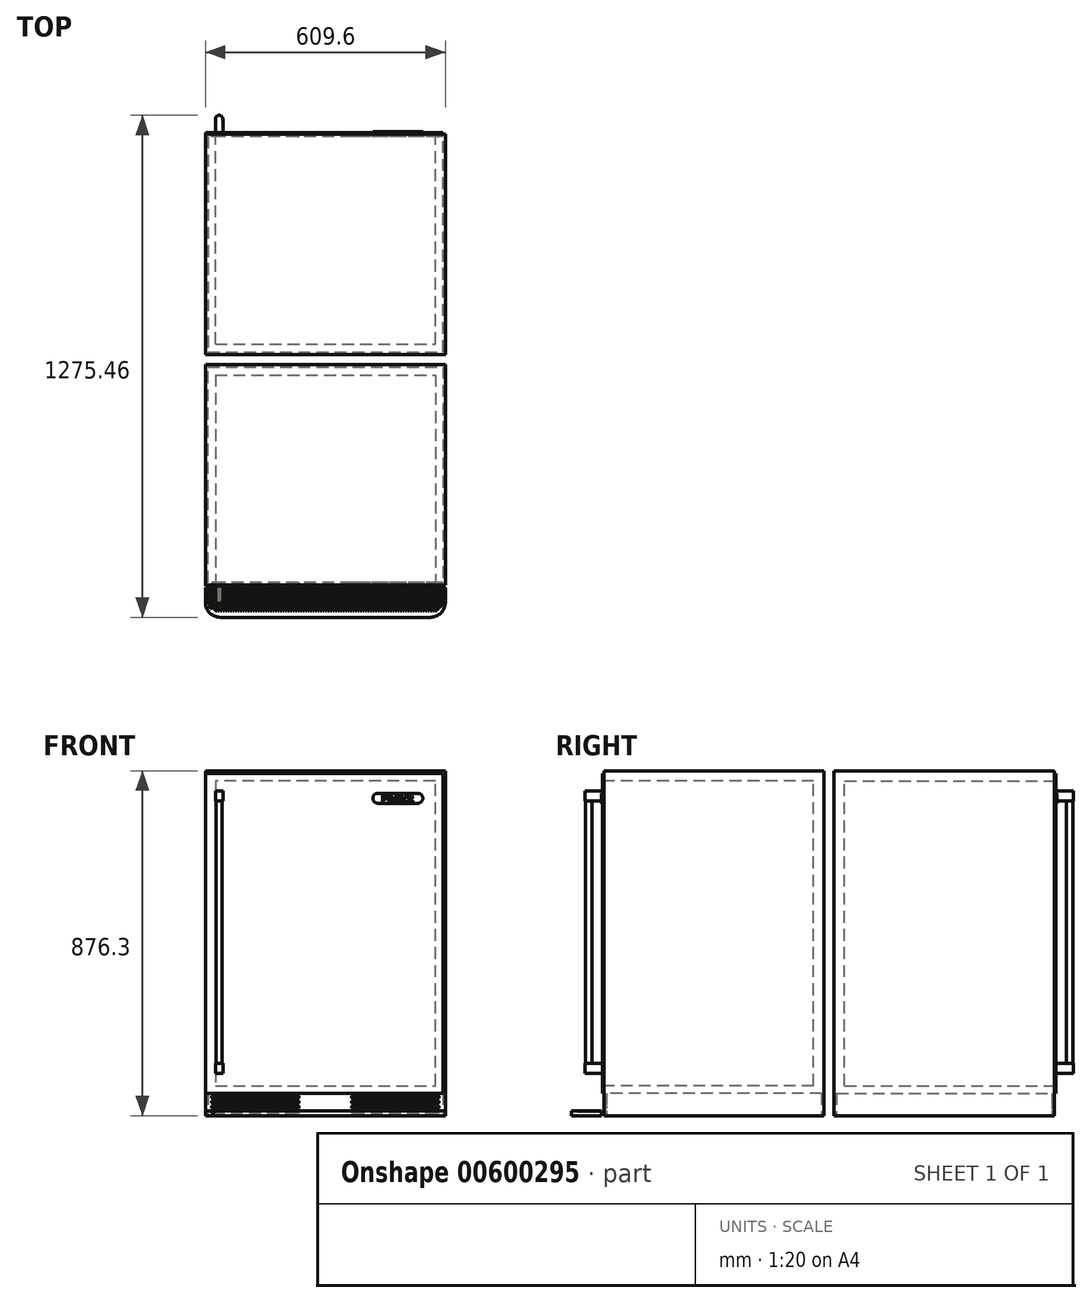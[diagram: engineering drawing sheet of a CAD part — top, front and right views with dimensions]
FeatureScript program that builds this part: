
annotation { "Feature Type Name" : "Feature", "Feature Type Description" : "" }
export const myFeature = defineFeature(function(context is Context, id is Id, definition is map)
    precondition{}
    {
        {
            var Q0;
            Q0=qCreatedBy(makeId("Front.planeOp"),FACE);
            var sketch = newSketch(context, id + "F0", { "sketchPlane" : qUnion([Q0])});
            skLineSegment(sketch, "E0.bottom", {"start": v(304.8, 438.15) * mm, "end": v(-304.8, 438.15) * mm});
            skLineSegment(sketch, "E0.top", {"start": v(304.8, -438.15) * mm, "end": v(-304.8, -438.15) * mm});
            skLineSegment(sketch, "E0.left", {"start": v(304.8, 438.15) * mm, "end": v(304.8, -438.15) * mm});
            skLineSegment(sketch, "E0.right", {"start": v(-304.8, 438.15) * mm, "end": v(-304.8, -438.15) * mm});
            skPoint(sketch, "E0.middle", {"position": v(0, 0) * mm});
            skSolve(sketch);
        }
        {
            var Q0;
            Q0 = qSketchRegion(id + "F0", true);
            extrude(context, id + "F1", {"entities" : qUnion([Q0]), "oppositeDirection" : true, "depth" : 559.94 * mm, "offsetDistance" : 25.4 * mm});
        }
        {
            var Q0;
            Q0=makeQuery(id+"F1.opExtrude","CAP_FACE",FACE,{"disambiguationData":[OSD([sQuery(id+"F0.wireOp",EDGE,"E0.bottom"),sQuery(id+"F0.wireOp",EDGE,"E0.top"),sQuery(id+"F0.wireOp",EDGE,"E0.left"),sQuery(id+"F0.wireOp",EDGE,"E0.right")])],"isStart":true});
            var sketch = newSketch(context, id + "F2", { "sketchPlane" : qUnion([Q0])});
            skLineSegment(sketch, "E1.0", {"start": v(-279.4, -412.75) * mm, "end": v(279.4, -412.75) * mm, "construction": true});
            skLineSegment(sketch, "E1.1", {"start": v(-279.4, 412.75) * mm, "end": v(-279.4, -412.75) * mm});
            skLineSegment(sketch, "E1.2", {"start": v(279.4, 412.75) * mm, "end": v(-279.4, 412.75) * mm});
            skLineSegment(sketch, "E1.3", {"start": v(279.4, -412.75) * mm, "end": v(279.4, 412.75) * mm});
            skLineSegment(sketch, "E2", {"start": v(-279.4, -361.95) * mm, "end": v(279.4, -361.95) * mm});
            skSolve(sketch);
        }
        {
            var Q0;
            Q0 = qSketchRegion(id + "F2", true);
            extrude(context, id + "F3", {"entities" : qUnion([Q0]), "operationType" : NewBodyOperationType.REMOVE, "oppositeDirection" : true, "depth" : 533.4 * mm, "offsetDistance" : 25.4 * mm});
        }
        {
            var Q0;
            Q0=makeQuery(id+"F1.opExtrude","CAP_FACE",FACE,{"disambiguationData":[OSD([sQuery(id+"F0.wireOp",EDGE,"E0.bottom"),sQuery(id+"F0.wireOp",EDGE,"E0.top"),sQuery(id+"F0.wireOp",EDGE,"E0.left"),sQuery(id+"F0.wireOp",EDGE,"E0.right")])],"isStart":true});
            var sketch = newSketch(context, id + "F4", { "sketchPlane" : qUnion([Q0])});
            skLineSegment(sketch, "E3.1", {"start": v(-304.8, 438.15) * mm, "end": v(-304.8, -438.15) * mm});
            skLineSegment(sketch, "E4.0", {"start": v(298.45, -431.8) * mm, "end": v(-304.8, -431.8) * mm, "construction": true});
            skLineSegment(sketch, "E4.1", {"start": v(298.45, 431.8) * mm, "end": v(298.45, -431.8) * mm});
            skLineSegment(sketch, "E4.2", {"start": v(298.45, 431.8) * mm, "end": v(-304.8, 431.8) * mm});
            skLineSegment(sketch, "E5", {"start": v(298.45, -381) * mm, "end": v(-304.8, -381) * mm});
            skSolve(sketch);
        }
        {
            var Q0;
            Q0 = qSketchRegion(id + "F4", true);
            extrude(context, id + "F5", {"entities" : qUnion([Q0]), "depth" : 3.17 * mm, "offsetDistance" : 25.4 * mm});
        }
        {
            var Q0;
            Q0=makeQuery(id+"F1.opExtrude","CAP_FACE",FACE,{"disambiguationData":[OSD([sQuery(id+"F0.wireOp",EDGE,"E0.bottom"),sQuery(id+"F0.wireOp",EDGE,"E0.top"),sQuery(id+"F0.wireOp",EDGE,"E0.left"),sQuery(id+"F0.wireOp",EDGE,"E0.right")])],"isStart":false});
            cPlane(context, id + "F6", {"entities" : qUnion([Q0]), "cplaneType" : CPlaneType.OFFSET, "offset" : 12.7 * mm, "width" : 152.4 * mm, "height" : 152.4 * mm});
        }
        {
            var Q0;
            Q0=makeQuery(id+"F1.opExtrude","CAP_FACE",FACE,{"disambiguationData":[OSD([sQuery(id+"F0.wireOp",EDGE,"E0.bottom"),sQuery(id+"F0.wireOp",EDGE,"E0.top"),sQuery(id+"F0.wireOp",EDGE,"E0.left"),sQuery(id+"F0.wireOp",EDGE,"E0.right")])],"isStart":true});
            var sketch = newSketch(context, id + "F7", { "sketchPlane" : qUnion([Q0])});
            skLineSegment(sketch, "E6", {"start": v(-285.75, -390.53) * mm, "end": v(-69.85, -390.53) * mm});
            skLineSegment(sketch, "E7", {"start": v(69.85, -390.53) * mm, "end": v(285.75, -390.53) * mm});
            skLineSegment(sketch, "E8", {"start": v(0, -484.65) * mm, "end": v(0, -438.15) * mm, "construction": true});
            skPoint(sketch, "E8.endSnap0", {"position": v(0, -438.15) * mm});
            skLineSegment(sketch, "E9.0.1.0", {"start": v(-285.75, -403.23) * mm, "end": v(-69.85, -403.23) * mm});
            skLineSegment(sketch, "E9.0.1.1", {"start": v(69.85, -403.22) * mm, "end": v(285.75, -403.22) * mm});
            skLineSegment(sketch, "E9.0.2.0", {"start": v(-285.75, -415.93) * mm, "end": v(-69.85, -415.93) * mm});
            skLineSegment(sketch, "E9.0.2.1", {"start": v(69.85, -415.93) * mm, "end": v(285.75, -415.93) * mm});
            skLineSegment(sketch, "E9.0.3.0", {"start": v(-285.75, -428.63) * mm, "end": v(-69.85, -428.63) * mm});
            skLineSegment(sketch, "E9.0.3.1", {"start": v(69.85, -428.62) * mm, "end": v(285.75, -428.62) * mm});
            skLineSegment(sketch, "E9.direction1", {"start": v(-285.75, -390.53) * mm, "end": v(-266.7, -390.53) * mm, "construction": true});
            skLineSegment(sketch, "E9.direction2", {"start": v(-285.75, -390.53) * mm, "end": v(-285.75, -403.23) * mm, "construction": true});
            skArc(sketch, "E10.0.startCap", {"start": v(-285.75, -393.7) * mm, "mid": v(-288.92, -390.53) * mm, "end": v(-285.75, -387.35) * mm});
            skArc(sketch, "E10.0.endCap", {"start": v(-69.85, -387.35) * mm, "mid": v(-66.67, -390.53) * mm, "end": v(-69.85, -393.7) * mm});
            skLineSegment(sketch, "E10.0.left", {"start": v(-285.75, -387.35) * mm, "end": v(-69.85, -387.35) * mm});
            skLineSegment(sketch, "E10.0.right", {"start": v(-285.75, -393.7) * mm, "end": v(-69.85, -393.7) * mm});
            skArc(sketch, "E10.1.startCap", {"start": v(-285.75, -406.4) * mm, "mid": v(-288.92, -403.23) * mm, "end": v(-285.75, -400.05) * mm});
            skArc(sketch, "E10.1.endCap", {"start": v(-69.85, -400.05) * mm, "mid": v(-66.67, -403.23) * mm, "end": v(-69.85, -406.4) * mm});
            skLineSegment(sketch, "E10.1.left", {"start": v(-285.75, -400.05) * mm, "end": v(-69.85, -400.05) * mm});
            skLineSegment(sketch, "E10.1.right", {"start": v(-285.75, -406.4) * mm, "end": v(-69.85, -406.4) * mm});
            skArc(sketch, "E10.2.startCap", {"start": v(-285.75, -419.1) * mm, "mid": v(-288.92, -415.93) * mm, "end": v(-285.75, -412.75) * mm});
            skArc(sketch, "E10.2.endCap", {"start": v(-69.85, -412.75) * mm, "mid": v(-66.67, -415.93) * mm, "end": v(-69.85, -419.1) * mm});
            skLineSegment(sketch, "E10.2.left", {"start": v(-285.75, -412.75) * mm, "end": v(-69.85, -412.75) * mm});
            skLineSegment(sketch, "E10.2.right", {"start": v(-285.75, -419.1) * mm, "end": v(-69.85, -419.1) * mm});
            skArc(sketch, "E10.3.startCap", {"start": v(-285.75, -431.8) * mm, "mid": v(-288.92, -428.63) * mm, "end": v(-285.75, -425.45) * mm});
            skArc(sketch, "E10.3.endCap", {"start": v(-69.85, -425.45) * mm, "mid": v(-66.67, -428.63) * mm, "end": v(-69.85, -431.8) * mm});
            skLineSegment(sketch, "E10.3.left", {"start": v(-285.75, -425.45) * mm, "end": v(-69.85, -425.45) * mm});
            skLineSegment(sketch, "E10.3.right", {"start": v(-285.75, -431.8) * mm, "end": v(-69.85, -431.8) * mm});
            skArc(sketch, "E10.4.startCap", {"start": v(69.85, -431.8) * mm, "mid": v(66.67, -428.63) * mm, "end": v(69.85, -425.45) * mm});
            skArc(sketch, "E10.4.endCap", {"start": v(285.75, -425.45) * mm, "mid": v(288.92, -428.63) * mm, "end": v(285.75, -431.8) * mm});
            skLineSegment(sketch, "E10.4.left", {"start": v(69.85, -425.45) * mm, "end": v(285.75, -425.45) * mm});
            skLineSegment(sketch, "E10.4.right", {"start": v(69.85, -431.8) * mm, "end": v(285.75, -431.8) * mm});
            skArc(sketch, "E10.5.startCap", {"start": v(69.85, -419.1) * mm, "mid": v(66.67, -415.93) * mm, "end": v(69.85, -412.75) * mm});
            skArc(sketch, "E10.5.endCap", {"start": v(285.75, -412.75) * mm, "mid": v(288.92, -415.93) * mm, "end": v(285.75, -419.1) * mm});
            skLineSegment(sketch, "E10.5.left", {"start": v(69.85, -412.75) * mm, "end": v(285.75, -412.75) * mm});
            skLineSegment(sketch, "E10.5.right", {"start": v(69.85, -419.1) * mm, "end": v(285.75, -419.1) * mm});
            skArc(sketch, "E10.6.startCap", {"start": v(69.85, -406.4) * mm, "mid": v(66.67, -403.23) * mm, "end": v(69.85, -400.05) * mm});
            skArc(sketch, "E10.6.endCap", {"start": v(285.75, -400.05) * mm, "mid": v(288.92, -403.23) * mm, "end": v(285.75, -406.4) * mm});
            skLineSegment(sketch, "E10.6.left", {"start": v(69.85, -400.05) * mm, "end": v(285.75, -400.05) * mm});
            skLineSegment(sketch, "E10.6.right", {"start": v(69.85, -406.4) * mm, "end": v(285.75, -406.4) * mm});
            skArc(sketch, "E10.7.startCap", {"start": v(69.85, -393.7) * mm, "mid": v(66.67, -390.53) * mm, "end": v(69.85, -387.35) * mm});
            skArc(sketch, "E10.7.endCap", {"start": v(285.75, -387.35) * mm, "mid": v(288.92, -390.53) * mm, "end": v(285.75, -393.7) * mm});
            skLineSegment(sketch, "E10.7.left", {"start": v(69.85, -387.35) * mm, "end": v(285.75, -387.35) * mm});
            skLineSegment(sketch, "E10.7.right", {"start": v(69.85, -393.7) * mm, "end": v(285.75, -393.7) * mm});
            skSolve(sketch);
        }
        {
            var Q0;
            Q0 = qSketchRegion(id + "F7", true);
            extrude(context, id + "F8", {"entities" : qUnion([Q0]), "operationType" : NewBodyOperationType.REMOVE, "oppositeDirection" : true, "depth" : 25.4 * mm, "offsetDistance" : 25.4 * mm});
        }
        {
            var Q0;
            Q0=makeQuery(id+"F1.opExtrude","SWEPT_FACE",FACE,{"disambiguationData":[OSD([sQuery(id+"F0.wireOp",EDGE,"E0.top")])]});
            var sketch = newSketch(context, id + "F9", { "sketchPlane" : qUnion([Q0])});
            skLineSegment(sketch, "E11.0", {"start": v(298.45, -6.35) * mm, "end": v(-298.45, -6.35) * mm});
            skLineSegment(sketch, "E11.1", {"start": v(298.45, -553.6) * mm, "end": v(298.45, -6.35) * mm});
            skLineSegment(sketch, "E11.2", {"start": v(-298.45, -553.6) * mm, "end": v(298.45, -553.6) * mm});
            skLineSegment(sketch, "E11.3", {"start": v(-298.45, -6.35) * mm, "end": v(-298.45, -553.6) * mm});
            skSolve(sketch);
        }
        {
            var Q0;
            Q0=makeQuery(id+"F9.imprint","IMPRINT",FACE,{"disambiguationData":[TD([[makeQuery(id+"F9.imprint","IMPRINT",EDGE,{"derivedFrom":sQuery(id+"F9.wireOp",EDGE,"E11.0")}),1.0]])]});
            extrude(context, id + "F10", {"entities" : qUnion([Q0]), "operationType" : NewBodyOperationType.REMOVE, "oppositeDirection" : true, "depth" : 57.15 * mm, "offsetDistance" : 25.4 * mm});
        }
        {
            var Q0;
            Q0=makeQuery(id+"F1.opExtrude","SWEPT_FACE",FACE,{"disambiguationData":[OSD([sQuery(id+"F0.wireOp",EDGE,"E0.bottom")])]});
            cPlane(context, id + "F11", {"entities" : qUnion([Q0]), "cplaneType" : CPlaneType.OFFSET, "offset" : 50.8 * mm, "oppositeDirection" : true, "width" : 152.4 * mm, "height" : 152.4 * mm});
        }
        {
            var Q0;
            Q0=qCreatedBy(id+"F11.planeOp",FACE);
            var sketch = newSketch(context, id + "F12", { "sketchPlane" : qUnion([Q0])});
            skCircle(sketch, "E12", {"center": v(-269.88, -38.1) * mm, "radius": 9.53 * mm});
            skLineSegment(sketch, "E13.0", {"start": v(298.45, -3.18) * mm, "end": v(-304.8, -3.18) * mm});
            skLineSegment(sketch, "E14", {"start": v(-279.4, -38.1) * mm, "end": v(-279.4, -3.18) * mm});
            skLineSegment(sketch, "E15", {"start": v(-279.4, -3.18) * mm, "end": v(-260.35, -3.18) * mm});
            skLineSegment(sketch, "E16", {"start": v(-260.35, -3.18) * mm, "end": v(-260.35, -38.1) * mm});
            skSolve(sketch);
        }
        {
            var Q0;
            Q0 = qSketchRegion(id + "F12", true);
            extrude(context, id + "F13", {"entities" : qUnion([Q0]), "operationType" : NewBodyOperationType.ADD, "oppositeDirection" : true, "depth" : 25.4 * mm, "offsetDistance" : 25.4 * mm});
        }
        {
            var Q0;
            Q0=makeQuery(id+"F5.opExtrude","SWEPT_FACE",FACE,{"disambiguationData":[OSD([sQuery(id+"F4.wireOp",EDGE,"E5")])]});
            cPlane(context, id + "F14", {"entities" : qUnion([Q0]), "cplaneType" : CPlaneType.OFFSET, "offset" : 50.8 * mm, "oppositeDirection" : true, "width" : 152.4 * mm, "height" : 152.4 * mm});
        }
        {
            var Q0;
            Q0=qCreatedBy(id+"F14.planeOp",FACE);
            var sketch = newSketch(context, id + "F15", { "sketchPlane" : qUnion([Q0])});
            skArc(sketch, "E17.0.0", {"start": v(-279.4, 38.1) * mm, "mid": v(-269.88, 47.62) * mm, "end": v(-260.35, 38.1) * mm});
            skLineSegment(sketch, "E17.0.1", {"start": v(-260.35, 38.1) * mm, "end": v(-260.35, 3.18) * mm});
            skLineSegment(sketch, "E17.0.2", {"start": v(-260.35, 3.18) * mm, "end": v(-279.4, 3.18) * mm});
            skLineSegment(sketch, "E17.0.3", {"start": v(-279.4, 3.18) * mm, "end": v(-279.4, 38.1) * mm});
            skSolve(sketch);
        }
        {
            var Q0;
            Q0 = qSketchRegion(id + "F15", true);
            extrude(context, id + "F16", {"entities" : qUnion([Q0]), "operationType" : NewBodyOperationType.ADD, "oppositeDirection" : true, "depth" : 25.4 * mm, "offsetDistance" : 25.4 * mm});
        }
        {
            var Q0;
            Q0=makeQuery(id+"F16.opExtrude","CAP_FACE",FACE,{"disambiguationData":[OSD([sQuery(id+"F15.wireOp",EDGE,"E17.0.0"),sQuery(id+"F15.wireOp",EDGE,"E17.0.1"),sQuery(id+"F15.wireOp",EDGE,"E17.0.2"),sQuery(id+"F15.wireOp",EDGE,"E17.0.3")])],"isStart":false});
            var sketch = newSketch(context, id + "F17", { "sketchPlane" : qUnion([Q0])});
            skCircle(sketch, "E18", {"center": v(-269.88, -38.1) * mm, "radius": 7.94 * mm});
            skSolve(sketch);
        }
        {
            var Q0;
            Q0 = qSketchRegion(id + "F17", true);
            extrude(context, id + "F18", {"entities" : qUnion([Q0]), "endBound" : BoundingType.UP_TO_NEXT, "depth" : 25.4 * mm, "offsetDistance" : 25.4 * mm});
        }
        {
            var Q0;
            Q0=makeQuery(id+"F5.opExtrude","CAP_FACE",FACE,{"disambiguationData":[OSD([sQuery(id+"F4.wireOp",EDGE,"E3.1"),sQuery(id+"F4.wireOp",EDGE,"E4.1"),sQuery(id+"F4.wireOp",EDGE,"E4.2"),sQuery(id+"F4.wireOp",EDGE,"E5")])],"isStart":false});
            var sketch = newSketch(context, id + "F19", { "sketchPlane" : qUnion([Q0])});
            skLineSegment(sketch, "E19", {"start": v(133.35, 368.3) * mm, "end": v(234.95, 368.3) * mm});
            skArc(sketch, "E20.0.startCap", {"start": v(133.35, 355.6) * mm, "mid": v(120.65, 368.3) * mm, "end": v(133.35, 381) * mm});
            skArc(sketch, "E20.0.endCap", {"start": v(234.95, 381) * mm, "mid": v(247.65, 368.3) * mm, "end": v(234.95, 355.6) * mm});
            skLineSegment(sketch, "E20.0.left", {"start": v(133.35, 381) * mm, "end": v(234.95, 381) * mm});
            skLineSegment(sketch, "E20.0.right", {"start": v(133.35, 355.6) * mm, "end": v(234.95, 355.6) * mm});
            skText(sketch, "E21", { "text": "Perlick", "fontName": "OpenSans-Regular.ttf"});
            skPoint(sketch, "E22", {"position": v(184.15, 381) * mm});
            skPoint(sketch, "E23", {"position": v(184.15, 368.3) * mm});
            const initialGuessF19  = {"E21": [0.1427, 0.35878, 1, 0, 0.01905]};
            skSetInitialGuess(sketch, initialGuessF19);
            skSolve(sketch);
        }
        {
            var Q0;
            Q0 = qSketchRegion(id + "F19", true);
            var Q1;
            {var subQ0=sQuery(id+"F19.wireOp",EDGE,"E21.sketch_text.stroke-10");Q1=makeQuery(id+"F19.imprint","IMPRINT",FACE,{"disambiguationData":[TD([[makeQuery(id+"F19.imprint","IMPRINT",EDGE,{"derivedFrom":subQ0}),1.0]])]});}
            var Q2;
            {var subQ1=sQuery(id+"F19.wireOp",EDGE,"E21.sketch_text.stroke-29");Q2=makeQuery(id+"F19.imprint","IMPRINT",FACE,{"disambiguationData":[TD([[makeQuery(id+"F19.imprint","IMPRINT",EDGE,{"derivedFrom":subQ1}),1.0]])]});}
            extrude(context, id + "F20", {"entities" : qUnion([Q0, Q1, Q2]), "depth" : 3.17 * mm, "offsetDistance" : 25.4 * mm});
        }
        {
            var Q0;
            Q0=makeQuery(id+"F1.opExtrude","SWEPT_BODY",BODY,{"disambiguationData":[OSD([sQuery(id+"F0.wireOp",EDGE,"E0.bottom"),sQuery(id+"F0.wireOp",EDGE,"E0.top"),sQuery(id+"F0.wireOp",EDGE,"E0.left"),sQuery(id+"F0.wireOp",EDGE,"E0.right")])]});
            var Q1;
            Q1=makeQuery(id+"F18.opExtrude","SWEPT_BODY",BODY,{"disambiguationData":[OSD([sQuery(id+"F17.wireOp",EDGE,"E18")])]});
            var Q2;
            Q2=makeQuery(id+"F5.opExtrude","SWEPT_BODY",BODY,{"disambiguationData":[OSD([sQuery(id+"F4.wireOp",EDGE,"E3.1"),sQuery(id+"F4.wireOp",EDGE,"E4.1"),sQuery(id+"F4.wireOp",EDGE,"E4.2"),sQuery(id+"F4.wireOp",EDGE,"E5")])]});
            var Q3;
            Q3=makeQuery(id+"F20.opExtrude","SWEPT_BODY",BODY,{"disambiguationData":[OSD([sQuery(id+"F19.wireOp",EDGE,"E19"),sQuery(id+"F19.wireOp",EDGE,"E20.0.startCap"),sQuery(id+"F19.wireOp",EDGE,"E20.0.endCap"),sQuery(id+"F19.wireOp",EDGE,"E20.0.left"),sQuery(id+"F19.wireOp",EDGE,"E20.0.right"),sQuery(id+"F19.wireOp",EDGE,"E21.sketch_text.stroke-0"),sQuery(id+"F19.wireOp",EDGE,"E21.sketch_text.stroke-1"),sQuery(id+"F19.wireOp",EDGE,"E21.sketch_text.stroke-2"),sQuery(id+"F19.wireOp",EDGE,"E21.sketch_text.stroke-3"),sQuery(id+"F19.wireOp",EDGE,"E21.sketch_text.stroke-4"),sQuery(id+"F19.wireOp",EDGE,"E21.sketch_text.stroke-5"),sQuery(id+"F19.wireOp",EDGE,"E21.sketch_text.stroke-6"),sQuery(id+"F19.wireOp",EDGE,"E21.sketch_text.stroke-7"),sQuery(id+"F19.wireOp",EDGE,"E21.sketch_text.stroke-15"),sQuery(id+"F19.wireOp",EDGE,"E21.sketch_text.stroke-16"),sQuery(id+"F19.wireOp",EDGE,"E21.sketch_text.stroke-17"),sQuery(id+"F19.wireOp",EDGE,"E21.sketch_text.stroke-18"),sQuery(id+"F19.wireOp",EDGE,"E21.sketch_text.stroke-19"),sQuery(id+"F19.wireOp",EDGE,"E21.sketch_text.stroke-20"),sQuery(id+"F19.wireOp",EDGE,"E21.sketch_text.stroke-21"),sQuery(id+"F19.wireOp",EDGE,"E21.sketch_text.stroke-22"),sQuery(id+"F19.wireOp",EDGE,"E21.sketch_text.stroke-23"),sQuery(id+"F19.wireOp",EDGE,"E21.sketch_text.stroke-24"),sQuery(id+"F19.wireOp",EDGE,"E21.sketch_text.stroke-25"),sQuery(id+"F19.wireOp",EDGE,"E21.sketch_text.stroke-26"),sQuery(id+"F19.wireOp",EDGE,"E21.sketch_text.stroke-27"),sQuery(id+"F19.wireOp",EDGE,"E21.sketch_text.stroke-28"),sQuery(id+"F19.wireOp",EDGE,"E21.sketch_text.stroke-34"),sQuery(id+"F19.wireOp",EDGE,"E21.sketch_text.stroke-35"),sQuery(id+"F19.wireOp",EDGE,"E21.sketch_text.stroke-36"),sQuery(id+"F19.wireOp",EDGE,"E21.sketch_text.stroke-37"),sQuery(id+"F19.wireOp",EDGE,"E21.sketch_text.stroke-38"),sQuery(id+"F19.wireOp",EDGE,"E21.sketch_text.stroke-39"),sQuery(id+"F19.wireOp",EDGE,"E21.sketch_text.stroke-40"),sQuery(id+"F19.wireOp",EDGE,"E21.sketch_text.stroke-41"),sQuery(id+"F19.wireOp",EDGE,"E21.sketch_text.stroke-42"),sQuery(id+"F19.wireOp",EDGE,"E21.sketch_text.stroke-43"),sQuery(id+"F19.wireOp",EDGE,"E21.sketch_text.stroke-44"),sQuery(id+"F19.wireOp",EDGE,"E21.sketch_text.stroke-45"),sQuery(id+"F19.wireOp",EDGE,"E21.sketch_text.stroke-46"),sQuery(id+"F19.wireOp",EDGE,"E21.sketch_text.stroke-47"),sQuery(id+"F19.wireOp",EDGE,"E21.sketch_text.stroke-48"),sQuery(id+"F19.wireOp",EDGE,"E21.sketch_text.stroke-49"),sQuery(id+"F19.wireOp",EDGE,"E21.sketch_text.stroke-50"),sQuery(id+"F19.wireOp",EDGE,"E21.sketch_text.stroke-51"),sQuery(id+"F19.wireOp",EDGE,"E21.sketch_text.stroke-52"),sQuery(id+"F19.wireOp",EDGE,"E21.sketch_text.stroke-53"),sQuery(id+"F19.wireOp",EDGE,"E21.sketch_text.stroke-54"),sQuery(id+"F19.wireOp",EDGE,"E21.sketch_text.stroke-55"),sQuery(id+"F19.wireOp",EDGE,"E21.sketch_text.stroke-56"),sQuery(id+"F19.wireOp",EDGE,"E21.sketch_text.stroke-57"),sQuery(id+"F19.wireOp",EDGE,"E21.sketch_text.stroke-58"),sQuery(id+"F19.wireOp",EDGE,"E21.sketch_text.stroke-59"),sQuery(id+"F19.wireOp",EDGE,"E21.sketch_text.stroke-60"),sQuery(id+"F19.wireOp",EDGE,"E21.sketch_text.stroke-61"),sQuery(id+"F19.wireOp",EDGE,"E21.sketch_text.stroke-62"),sQuery(id+"F19.wireOp",EDGE,"E21.sketch_text.stroke-63"),sQuery(id+"F19.wireOp",EDGE,"E21.sketch_text.stroke-64"),sQuery(id+"F19.wireOp",EDGE,"E21.sketch_text.stroke-65"),sQuery(id+"F19.wireOp",EDGE,"E21.sketch_text.stroke-66"),sQuery(id+"F19.wireOp",EDGE,"E21.sketch_text.stroke-67"),sQuery(id+"F19.wireOp",EDGE,"E21.sketch_text.stroke-68"),sQuery(id+"F19.wireOp",EDGE,"E21.sketch_text.stroke-69"),sQuery(id+"F19.wireOp",EDGE,"E21.sketch_text.stroke-70"),sQuery(id+"F19.wireOp",EDGE,"E21.sketch_text.stroke-71"),sQuery(id+"F19.wireOp",EDGE,"E21.sketch_text.stroke-72"),sQuery(id+"F19.wireOp",EDGE,"E21.sketch_text.stroke-73"),sQuery(id+"F19.wireOp",EDGE,"E21.sketch_text.stroke-74"),sQuery(id+"F19.wireOp",EDGE,"E21.sketch_text.stroke-75"),sQuery(id+"F19.wireOp",EDGE,"E21.sketch_text.stroke-76"),sQuery(id+"F19.wireOp",EDGE,"E21.sketch_text.stroke-77"),sQuery(id+"F19.wireOp",EDGE,"E21.sketch_text.stroke-79"),sQuery(id+"F19.wireOp",EDGE,"E21.sketch_text.stroke-80"),sQuery(id+"F19.wireOp",EDGE,"E21.sketch_text.stroke-81"),sQuery(id+"F19.wireOp",EDGE,"E21.sketch_text.stroke-82"),sQuery(id+"F19.wireOp",EDGE,"E21.sketch_text.stroke-83"),sQuery(id+"F19.wireOp",EDGE,"E21.sketch_text.stroke-84"),sQuery(id+"F19.wireOp",EDGE,"E21.sketch_text.stroke-85"),sQuery(id+"F19.wireOp",EDGE,"E21.sketch_text.stroke-86"),sQuery(id+"F19.wireOp",EDGE,"E21.sketch_text.stroke-87"),sQuery(id+"F19.wireOp",EDGE,"E21.sketch_text.stroke-88"),sQuery(id+"F19.wireOp",EDGE,"E21.sketch_text.stroke-89"),sQuery(id+"F19.wireOp",EDGE,"E21.sketch_text.stroke-90")])]});
            var Q4;
            Q4=qCreatedBy(id+"F6.planeOp",FACE);
            mirror(context, id + "F21", {"entities" : qUnion([Q0, Q1, Q2, Q3]), "mirrorPlane" : qUnion([Q4])});
        }
        {
            var Q0;
            Q0=makeQuery(id+"F21.opPattern","COPY",FACE,{"derivedFrom":makeQuery(id+"F1.opExtrude","SWEPT_FACE",FACE,{"disambiguationData":[OSD([sQuery(id+"F0.wireOp",EDGE,"E0.top")])]}),"instanceName":"1"});
            var sketch = newSketch(context, id + "F22", { "sketchPlane" : qUnion([Q0])});
            skLineSegment(sketch, "E24.bottom", {"start": v(-266.7, 82.55) * mm, "end": v(266.7, 82.55) * mm});
            skLineSegment(sketch, "E24.top", {"start": v(-304.8, 6.35) * mm, "end": v(304.8, 6.35) * mm});
            skLineSegment(sketch, "E24.left", {"start": v(-304.8, 44.45) * mm, "end": v(-304.8, 6.35) * mm});
            skLineSegment(sketch, "E24.right", {"start": v(304.8, 44.45) * mm, "end": v(304.8, 6.35) * mm});
            skPoint(sketch, "E25.visualSharp", {"position": v(-304.8, 82.55) * mm});
            skArc(sketch, "E25.filletArc", {"start": v(-266.7, 82.55) * mm, "mid": v(-293.64, 71.4) * mm, "end": v(-304.8, 44.45) * mm});
            skPoint(sketch, "E26.visualSharp", {"position": v(304.8, 82.55) * mm});
            skArc(sketch, "E26.filletArc", {"start": v(304.8, 44.45) * mm, "mid": v(293.64, 71.4) * mm, "end": v(266.7, 82.55) * mm});
            skSolve(sketch);
        }
        {
            var Q0;
            Q0 = qSketchRegion(id + "F22", true);
            extrude(context, id + "F23", {"entities" : qUnion([Q0]), "oppositeDirection" : true, "depth" : 12.7 * mm, "offsetDistance" : 25.4 * mm});
        }
        {
            var Q0;
            Q0=makeQuery(id+"F23.opExtrude","CAP_FACE",FACE,{"disambiguationData":[OSD([sQuery(id+"F22.wireOp",EDGE,"E24.bottom"),sQuery(id+"F22.wireOp",EDGE,"E24.top"),sQuery(id+"F22.wireOp",EDGE,"E24.left"),sQuery(id+"F22.wireOp",EDGE,"E24.right"),sQuery(id+"F22.wireOp",EDGE,"E25.filletArc"),sQuery(id+"F22.wireOp",EDGE,"E26.filletArc")])],"isStart":false});
            var sketch = newSketch(context, id + "F24", { "sketchPlane" : qUnion([Q0])});
            skCircle(sketch, "E27", {"center": v(-300.02, -11.11) * mm, "radius": 1.59 * mm});
            skCircle(sketch, "E28", {"center": v(-296.85, -14.29) * mm, "radius": 1.59 * mm});
            skCircle(sketch, "E29", {"center": v(-293.67, -11.11) * mm, "radius": 1.59 * mm});
            skLineSegment(sketch, "E30", {"start": v(-300.02, -11.11) * mm, "end": v(-293.67, -11.11) * mm, "construction": true});
            skLineSegment(sketch, "E31", {"start": v(-296.85, -11.11) * mm, "end": v(-296.85, -14.29) * mm, "construction": true});
            skCircle(sketch, "E32", {"center": v(-290.5, -14.29) * mm, "radius": 1.59 * mm});
            skLineSegment(sketch, "E33", {"start": v(-296.85, -14.29) * mm, "end": v(-290.5, -14.29) * mm, "construction": true});
            skCircle(sketch, "E34.1.0.0", {"center": v(-280.97, -11.11) * mm, "radius": 1.59 * mm});
            skCircle(sketch, "E34.1.0.1", {"center": v(-287.32, -11.11) * mm, "radius": 1.59 * mm});
            skCircle(sketch, "E34.1.0.2", {"center": v(-284.15, -14.29) * mm, "radius": 1.59 * mm});
            skCircle(sketch, "E34.1.0.3", {"center": v(-277.8, -14.29) * mm, "radius": 1.59 * mm});
            skCircle(sketch, "E34.2.0.0", {"center": v(-268.27, -11.11) * mm, "radius": 1.59 * mm});
            skCircle(sketch, "E34.2.0.1", {"center": v(-274.62, -11.11) * mm, "radius": 1.59 * mm});
            skCircle(sketch, "E34.2.0.2", {"center": v(-271.45, -14.29) * mm, "radius": 1.59 * mm});
            skCircle(sketch, "E34.2.0.3", {"center": v(-265.1, -14.29) * mm, "radius": 1.59 * mm});
            skCircle(sketch, "E34.3.0.0", {"center": v(-255.57, -11.11) * mm, "radius": 1.59 * mm});
            skCircle(sketch, "E34.3.0.1", {"center": v(-261.92, -11.11) * mm, "radius": 1.59 * mm});
            skCircle(sketch, "E34.3.0.2", {"center": v(-258.75, -14.29) * mm, "radius": 1.59 * mm});
            skCircle(sketch, "E34.3.0.3", {"center": v(-252.4, -14.29) * mm, "radius": 1.59 * mm});
            skCircle(sketch, "E34.4.0.0", {"center": v(-242.87, -11.11) * mm, "radius": 1.59 * mm});
            skCircle(sketch, "E34.4.0.1", {"center": v(-249.22, -11.11) * mm, "radius": 1.59 * mm});
            skCircle(sketch, "E34.4.0.2", {"center": v(-246.05, -14.29) * mm, "radius": 1.59 * mm});
            skCircle(sketch, "E34.4.0.3", {"center": v(-239.7, -14.29) * mm, "radius": 1.59 * mm});
            skCircle(sketch, "E34.5.0.0", {"center": v(-230.17, -11.11) * mm, "radius": 1.59 * mm});
            skCircle(sketch, "E34.5.0.1", {"center": v(-236.52, -11.11) * mm, "radius": 1.59 * mm});
            skCircle(sketch, "E34.5.0.2", {"center": v(-233.35, -14.29) * mm, "radius": 1.59 * mm});
            skCircle(sketch, "E34.5.0.3", {"center": v(-227, -14.29) * mm, "radius": 1.59 * mm});
            skCircle(sketch, "E34.6.0.0", {"center": v(-217.47, -11.11) * mm, "radius": 1.59 * mm});
            skCircle(sketch, "E34.6.0.1", {"center": v(-223.82, -11.11) * mm, "radius": 1.59 * mm});
            skCircle(sketch, "E34.6.0.2", {"center": v(-220.65, -14.29) * mm, "radius": 1.59 * mm});
            skCircle(sketch, "E34.6.0.3", {"center": v(-214.3, -14.29) * mm, "radius": 1.59 * mm});
            skCircle(sketch, "E34.7.0.0", {"center": v(-204.77, -11.11) * mm, "radius": 1.59 * mm});
            skCircle(sketch, "E34.7.0.1", {"center": v(-211.12, -11.11) * mm, "radius": 1.59 * mm});
            skCircle(sketch, "E34.7.0.2", {"center": v(-207.95, -14.29) * mm, "radius": 1.59 * mm});
            skCircle(sketch, "E34.7.0.3", {"center": v(-201.6, -14.29) * mm, "radius": 1.59 * mm});
            skCircle(sketch, "E34.8.0.0", {"center": v(-192.07, -11.11) * mm, "radius": 1.59 * mm});
            skCircle(sketch, "E34.8.0.1", {"center": v(-198.42, -11.11) * mm, "radius": 1.59 * mm});
            skCircle(sketch, "E34.8.0.2", {"center": v(-195.25, -14.29) * mm, "radius": 1.59 * mm});
            skCircle(sketch, "E34.8.0.3", {"center": v(-188.9, -14.29) * mm, "radius": 1.59 * mm});
            skCircle(sketch, "E34.9.0.0", {"center": v(-179.37, -11.11) * mm, "radius": 1.59 * mm});
            skCircle(sketch, "E34.9.0.1", {"center": v(-185.72, -11.11) * mm, "radius": 1.59 * mm});
            skCircle(sketch, "E34.9.0.2", {"center": v(-182.55, -14.29) * mm, "radius": 1.59 * mm});
            skCircle(sketch, "E34.9.0.3", {"center": v(-176.2, -14.29) * mm, "radius": 1.59 * mm});
            skCircle(sketch, "E34.10.0.0", {"center": v(-166.67, -11.11) * mm, "radius": 1.59 * mm});
            skCircle(sketch, "E34.10.0.1", {"center": v(-173.02, -11.11) * mm, "radius": 1.59 * mm});
            skCircle(sketch, "E34.10.0.2", {"center": v(-169.85, -14.29) * mm, "radius": 1.59 * mm});
            skCircle(sketch, "E34.10.0.3", {"center": v(-163.5, -14.29) * mm, "radius": 1.59 * mm});
            skCircle(sketch, "E34.11.0.0", {"center": v(-153.97, -11.11) * mm, "radius": 1.59 * mm});
            skCircle(sketch, "E34.11.0.1", {"center": v(-160.32, -11.11) * mm, "radius": 1.59 * mm});
            skCircle(sketch, "E34.11.0.2", {"center": v(-157.15, -14.29) * mm, "radius": 1.59 * mm});
            skCircle(sketch, "E34.11.0.3", {"center": v(-150.8, -14.29) * mm, "radius": 1.59 * mm});
            skCircle(sketch, "E34.12.0.0", {"center": v(-141.27, -11.11) * mm, "radius": 1.59 * mm});
            skCircle(sketch, "E34.12.0.1", {"center": v(-147.62, -11.11) * mm, "radius": 1.59 * mm});
            skCircle(sketch, "E34.12.0.2", {"center": v(-144.45, -14.29) * mm, "radius": 1.59 * mm});
            skCircle(sketch, "E34.12.0.3", {"center": v(-138.1, -14.29) * mm, "radius": 1.59 * mm});
            skCircle(sketch, "E34.13.0.0", {"center": v(-128.57, -11.11) * mm, "radius": 1.59 * mm});
            skCircle(sketch, "E34.13.0.1", {"center": v(-134.92, -11.11) * mm, "radius": 1.59 * mm});
            skCircle(sketch, "E34.13.0.2", {"center": v(-131.75, -14.29) * mm, "radius": 1.59 * mm});
            skCircle(sketch, "E34.13.0.3", {"center": v(-125.4, -14.29) * mm, "radius": 1.59 * mm});
            skCircle(sketch, "E34.14.0.0", {"center": v(-115.87, -11.11) * mm, "radius": 1.59 * mm});
            skCircle(sketch, "E34.14.0.1", {"center": v(-122.22, -11.11) * mm, "radius": 1.59 * mm});
            skCircle(sketch, "E34.14.0.2", {"center": v(-119.05, -14.29) * mm, "radius": 1.59 * mm});
            skCircle(sketch, "E34.14.0.3", {"center": v(-112.7, -14.29) * mm, "radius": 1.59 * mm});
            skCircle(sketch, "E34.15.0.0", {"center": v(-103.17, -11.11) * mm, "radius": 1.59 * mm});
            skCircle(sketch, "E34.15.0.1", {"center": v(-109.52, -11.11) * mm, "radius": 1.59 * mm});
            skCircle(sketch, "E34.15.0.2", {"center": v(-106.35, -14.29) * mm, "radius": 1.59 * mm});
            skCircle(sketch, "E34.15.0.3", {"center": v(-100, -14.29) * mm, "radius": 1.59 * mm});
            skCircle(sketch, "E34.16.0.0", {"center": v(-90.47, -11.11) * mm, "radius": 1.59 * mm});
            skCircle(sketch, "E34.16.0.1", {"center": v(-96.82, -11.11) * mm, "radius": 1.59 * mm});
            skCircle(sketch, "E34.16.0.2", {"center": v(-93.65, -14.29) * mm, "radius": 1.59 * mm});
            skCircle(sketch, "E34.16.0.3", {"center": v(-87.3, -14.29) * mm, "radius": 1.59 * mm});
            skCircle(sketch, "E34.17.0.0", {"center": v(-77.77, -11.11) * mm, "radius": 1.59 * mm});
            skCircle(sketch, "E34.17.0.1", {"center": v(-84.12, -11.11) * mm, "radius": 1.59 * mm});
            skCircle(sketch, "E34.17.0.2", {"center": v(-80.95, -14.29) * mm, "radius": 1.59 * mm});
            skCircle(sketch, "E34.17.0.3", {"center": v(-74.6, -14.29) * mm, "radius": 1.59 * mm});
            skCircle(sketch, "E34.18.0.0", {"center": v(-65.07, -11.11) * mm, "radius": 1.59 * mm});
            skCircle(sketch, "E34.18.0.1", {"center": v(-71.42, -11.11) * mm, "radius": 1.59 * mm});
            skCircle(sketch, "E34.18.0.2", {"center": v(-68.25, -14.29) * mm, "radius": 1.59 * mm});
            skCircle(sketch, "E34.18.0.3", {"center": v(-61.9, -14.29) * mm, "radius": 1.59 * mm});
            skCircle(sketch, "E34.19.0.0", {"center": v(-52.37, -11.11) * mm, "radius": 1.59 * mm});
            skCircle(sketch, "E34.19.0.1", {"center": v(-58.72, -11.11) * mm, "radius": 1.59 * mm});
            skCircle(sketch, "E34.19.0.2", {"center": v(-55.55, -14.29) * mm, "radius": 1.59 * mm});
            skCircle(sketch, "E34.19.0.3", {"center": v(-49.2, -14.29) * mm, "radius": 1.59 * mm});
            skCircle(sketch, "E34.20.0.0", {"center": v(-39.67, -11.11) * mm, "radius": 1.59 * mm});
            skCircle(sketch, "E34.20.0.1", {"center": v(-46.02, -11.11) * mm, "radius": 1.59 * mm});
            skCircle(sketch, "E34.20.0.2", {"center": v(-42.85, -14.29) * mm, "radius": 1.59 * mm});
            skCircle(sketch, "E34.20.0.3", {"center": v(-36.5, -14.29) * mm, "radius": 1.59 * mm});
            skCircle(sketch, "E34.21.0.0", {"center": v(-26.97, -11.11) * mm, "radius": 1.59 * mm});
            skCircle(sketch, "E34.21.0.1", {"center": v(-33.32, -11.11) * mm, "radius": 1.59 * mm});
            skCircle(sketch, "E34.21.0.2", {"center": v(-30.15, -14.29) * mm, "radius": 1.59 * mm});
            skCircle(sketch, "E34.21.0.3", {"center": v(-23.8, -14.29) * mm, "radius": 1.59 * mm});
            skCircle(sketch, "E34.22.0.0", {"center": v(-14.27, -11.11) * mm, "radius": 1.59 * mm});
            skCircle(sketch, "E34.22.0.1", {"center": v(-20.62, -11.11) * mm, "radius": 1.59 * mm});
            skCircle(sketch, "E34.22.0.2", {"center": v(-17.45, -14.29) * mm, "radius": 1.59 * mm});
            skCircle(sketch, "E34.22.0.3", {"center": v(-11.1, -14.29) * mm, "radius": 1.59 * mm});
            skCircle(sketch, "E34.23.0.0", {"center": v(-1.57, -11.11) * mm, "radius": 1.59 * mm});
            skCircle(sketch, "E34.23.0.1", {"center": v(-7.92, -11.11) * mm, "radius": 1.59 * mm});
            skCircle(sketch, "E34.23.0.2", {"center": v(-4.75, -14.29) * mm, "radius": 1.59 * mm});
            skCircle(sketch, "E34.23.0.3", {"center": v(1.6, -14.29) * mm, "radius": 1.59 * mm});
            skCircle(sketch, "E34.24.0.0", {"center": v(11.13, -11.11) * mm, "radius": 1.59 * mm});
            skCircle(sketch, "E34.24.0.1", {"center": v(4.78, -11.11) * mm, "radius": 1.59 * mm});
            skCircle(sketch, "E34.24.0.2", {"center": v(7.95, -14.29) * mm, "radius": 1.59 * mm});
            skCircle(sketch, "E34.24.0.3", {"center": v(14.3, -14.29) * mm, "radius": 1.59 * mm});
            skCircle(sketch, "E34.25.0.0", {"center": v(23.83, -11.11) * mm, "radius": 1.59 * mm});
            skCircle(sketch, "E34.25.0.1", {"center": v(17.48, -11.11) * mm, "radius": 1.59 * mm});
            skCircle(sketch, "E34.25.0.2", {"center": v(20.65, -14.29) * mm, "radius": 1.59 * mm});
            skCircle(sketch, "E34.25.0.3", {"center": v(27, -14.29) * mm, "radius": 1.59 * mm});
            skCircle(sketch, "E34.26.0.0", {"center": v(36.53, -11.11) * mm, "radius": 1.59 * mm});
            skCircle(sketch, "E34.26.0.1", {"center": v(30.18, -11.11) * mm, "radius": 1.59 * mm});
            skCircle(sketch, "E34.26.0.2", {"center": v(33.35, -14.29) * mm, "radius": 1.59 * mm});
            skCircle(sketch, "E34.26.0.3", {"center": v(39.7, -14.29) * mm, "radius": 1.59 * mm});
            skCircle(sketch, "E34.27.0.0", {"center": v(49.23, -11.11) * mm, "radius": 1.59 * mm});
            skCircle(sketch, "E34.27.0.1", {"center": v(42.88, -11.11) * mm, "radius": 1.59 * mm});
            skCircle(sketch, "E34.27.0.2", {"center": v(46.05, -14.29) * mm, "radius": 1.59 * mm});
            skCircle(sketch, "E34.27.0.3", {"center": v(52.4, -14.29) * mm, "radius": 1.59 * mm});
            skCircle(sketch, "E34.28.0.0", {"center": v(61.93, -11.11) * mm, "radius": 1.59 * mm});
            skCircle(sketch, "E34.28.0.1", {"center": v(55.58, -11.11) * mm, "radius": 1.59 * mm});
            skCircle(sketch, "E34.28.0.2", {"center": v(58.75, -14.29) * mm, "radius": 1.59 * mm});
            skCircle(sketch, "E34.28.0.3", {"center": v(65.1, -14.29) * mm, "radius": 1.59 * mm});
            skCircle(sketch, "E34.29.0.0", {"center": v(74.63, -11.11) * mm, "radius": 1.59 * mm});
            skCircle(sketch, "E34.29.0.1", {"center": v(68.28, -11.11) * mm, "radius": 1.59 * mm});
            skCircle(sketch, "E34.29.0.2", {"center": v(71.45, -14.29) * mm, "radius": 1.59 * mm});
            skCircle(sketch, "E34.29.0.3", {"center": v(77.8, -14.29) * mm, "radius": 1.59 * mm});
            skCircle(sketch, "E34.30.0.0", {"center": v(87.33, -11.11) * mm, "radius": 1.59 * mm});
            skCircle(sketch, "E34.30.0.1", {"center": v(80.98, -11.11) * mm, "radius": 1.59 * mm});
            skCircle(sketch, "E34.30.0.2", {"center": v(84.15, -14.29) * mm, "radius": 1.59 * mm});
            skCircle(sketch, "E34.30.0.3", {"center": v(90.5, -14.29) * mm, "radius": 1.59 * mm});
            skCircle(sketch, "E34.31.0.0", {"center": v(100.03, -11.11) * mm, "radius": 1.59 * mm});
            skCircle(sketch, "E34.31.0.1", {"center": v(93.68, -11.11) * mm, "radius": 1.59 * mm});
            skCircle(sketch, "E34.31.0.2", {"center": v(96.85, -14.29) * mm, "radius": 1.59 * mm});
            skCircle(sketch, "E34.31.0.3", {"center": v(103.2, -14.29) * mm, "radius": 1.59 * mm});
            skCircle(sketch, "E34.32.0.0", {"center": v(112.73, -11.11) * mm, "radius": 1.59 * mm});
            skCircle(sketch, "E34.32.0.1", {"center": v(106.38, -11.11) * mm, "radius": 1.59 * mm});
            skCircle(sketch, "E34.32.0.2", {"center": v(109.55, -14.29) * mm, "radius": 1.59 * mm});
            skCircle(sketch, "E34.32.0.3", {"center": v(115.9, -14.29) * mm, "radius": 1.59 * mm});
            skCircle(sketch, "E34.33.0.0", {"center": v(125.43, -11.11) * mm, "radius": 1.59 * mm});
            skCircle(sketch, "E34.33.0.1", {"center": v(119.08, -11.11) * mm, "radius": 1.59 * mm});
            skCircle(sketch, "E34.33.0.2", {"center": v(122.25, -14.29) * mm, "radius": 1.59 * mm});
            skCircle(sketch, "E34.33.0.3", {"center": v(128.6, -14.29) * mm, "radius": 1.59 * mm});
            skCircle(sketch, "E34.34.0.0", {"center": v(138.13, -11.11) * mm, "radius": 1.59 * mm});
            skCircle(sketch, "E34.34.0.1", {"center": v(131.78, -11.11) * mm, "radius": 1.59 * mm});
            skCircle(sketch, "E34.34.0.2", {"center": v(134.95, -14.29) * mm, "radius": 1.59 * mm});
            skCircle(sketch, "E34.34.0.3", {"center": v(141.3, -14.29) * mm, "radius": 1.59 * mm});
            skCircle(sketch, "E34.35.0.0", {"center": v(150.83, -11.11) * mm, "radius": 1.59 * mm});
            skCircle(sketch, "E34.35.0.1", {"center": v(144.48, -11.11) * mm, "radius": 1.59 * mm});
            skCircle(sketch, "E34.35.0.2", {"center": v(147.65, -14.29) * mm, "radius": 1.59 * mm});
            skCircle(sketch, "E34.35.0.3", {"center": v(154, -14.29) * mm, "radius": 1.59 * mm});
            skCircle(sketch, "E34.36.0.0", {"center": v(163.53, -11.11) * mm, "radius": 1.59 * mm});
            skCircle(sketch, "E34.36.0.1", {"center": v(157.18, -11.11) * mm, "radius": 1.59 * mm});
            skCircle(sketch, "E34.36.0.2", {"center": v(160.35, -14.29) * mm, "radius": 1.59 * mm});
            skCircle(sketch, "E34.36.0.3", {"center": v(166.7, -14.29) * mm, "radius": 1.59 * mm});
            skCircle(sketch, "E34.37.0.0", {"center": v(176.23, -11.11) * mm, "radius": 1.59 * mm});
            skCircle(sketch, "E34.37.0.1", {"center": v(169.88, -11.11) * mm, "radius": 1.59 * mm});
            skCircle(sketch, "E34.37.0.2", {"center": v(173.05, -14.29) * mm, "radius": 1.59 * mm});
            skCircle(sketch, "E34.37.0.3", {"center": v(179.4, -14.29) * mm, "radius": 1.59 * mm});
            skCircle(sketch, "E34.38.0.0", {"center": v(188.93, -11.11) * mm, "radius": 1.59 * mm});
            skCircle(sketch, "E34.38.0.1", {"center": v(182.58, -11.11) * mm, "radius": 1.59 * mm});
            skCircle(sketch, "E34.38.0.2", {"center": v(185.75, -14.29) * mm, "radius": 1.59 * mm});
            skCircle(sketch, "E34.38.0.3", {"center": v(192.1, -14.29) * mm, "radius": 1.59 * mm});
            skCircle(sketch, "E34.39.0.0", {"center": v(201.63, -11.11) * mm, "radius": 1.59 * mm});
            skCircle(sketch, "E34.39.0.1", {"center": v(195.28, -11.11) * mm, "radius": 1.59 * mm});
            skCircle(sketch, "E34.39.0.2", {"center": v(198.45, -14.29) * mm, "radius": 1.59 * mm});
            skCircle(sketch, "E34.39.0.3", {"center": v(204.8, -14.29) * mm, "radius": 1.59 * mm});
            skCircle(sketch, "E34.40.0.0", {"center": v(214.33, -11.11) * mm, "radius": 1.59 * mm});
            skCircle(sketch, "E34.40.0.1", {"center": v(207.98, -11.11) * mm, "radius": 1.59 * mm});
            skCircle(sketch, "E34.40.0.2", {"center": v(211.15, -14.29) * mm, "radius": 1.59 * mm});
            skCircle(sketch, "E34.40.0.3", {"center": v(217.5, -14.29) * mm, "radius": 1.59 * mm});
            skCircle(sketch, "E34.41.0.0", {"center": v(227.03, -11.11) * mm, "radius": 1.59 * mm});
            skCircle(sketch, "E34.41.0.1", {"center": v(220.68, -11.11) * mm, "radius": 1.59 * mm});
            skCircle(sketch, "E34.41.0.2", {"center": v(223.85, -14.29) * mm, "radius": 1.59 * mm});
            skCircle(sketch, "E34.41.0.3", {"center": v(230.2, -14.29) * mm, "radius": 1.59 * mm});
            skCircle(sketch, "E34.42.0.0", {"center": v(239.73, -11.11) * mm, "radius": 1.59 * mm});
            skCircle(sketch, "E34.42.0.1", {"center": v(233.38, -11.11) * mm, "radius": 1.59 * mm});
            skCircle(sketch, "E34.42.0.2", {"center": v(236.55, -14.29) * mm, "radius": 1.59 * mm});
            skCircle(sketch, "E34.42.0.3", {"center": v(242.9, -14.29) * mm, "radius": 1.59 * mm});
            skCircle(sketch, "E34.43.0.0", {"center": v(252.43, -11.11) * mm, "radius": 1.59 * mm});
            skCircle(sketch, "E34.43.0.1", {"center": v(246.08, -11.11) * mm, "radius": 1.59 * mm});
            skCircle(sketch, "E34.43.0.2", {"center": v(249.25, -14.29) * mm, "radius": 1.59 * mm});
            skCircle(sketch, "E34.43.0.3", {"center": v(255.6, -14.29) * mm, "radius": 1.59 * mm});
            skCircle(sketch, "E34.44.0.0", {"center": v(265.13, -11.11) * mm, "radius": 1.59 * mm});
            skCircle(sketch, "E34.44.0.1", {"center": v(258.78, -11.11) * mm, "radius": 1.59 * mm});
            skCircle(sketch, "E34.44.0.2", {"center": v(261.95, -14.29) * mm, "radius": 1.59 * mm});
            skCircle(sketch, "E34.44.0.3", {"center": v(268.3, -14.29) * mm, "radius": 1.59 * mm});
            skCircle(sketch, "E34.45.0.0", {"center": v(277.83, -11.11) * mm, "radius": 1.59 * mm});
            skCircle(sketch, "E34.45.0.1", {"center": v(271.48, -11.11) * mm, "radius": 1.59 * mm});
            skCircle(sketch, "E34.45.0.2", {"center": v(274.65, -14.29) * mm, "radius": 1.59 * mm});
            skCircle(sketch, "E34.45.0.3", {"center": v(281, -14.29) * mm, "radius": 1.59 * mm});
            skCircle(sketch, "E34.46.0.0", {"center": v(290.53, -11.11) * mm, "radius": 1.59 * mm});
            skCircle(sketch, "E34.46.0.1", {"center": v(284.18, -11.11) * mm, "radius": 1.59 * mm});
            skCircle(sketch, "E34.46.0.2", {"center": v(287.35, -14.29) * mm, "radius": 1.59 * mm});
            skCircle(sketch, "E34.46.0.3", {"center": v(293.7, -14.29) * mm, "radius": 1.59 * mm});
            skLineSegment(sketch, "E34.direction1", {"start": v(-293.67, -11.11) * mm, "end": v(-280.97, -11.11) * mm, "construction": true});
            skCircle(sketch, "E35.1.0.0", {"center": v(296.88, -11.11) * mm, "radius": 1.59 * mm});
            skCircle(sketch, "E35.1.0.1", {"center": v(300.05, -14.29) * mm, "radius": 1.59 * mm});
            skLineSegment(sketch, "E35.direction1", {"start": v(290.53, -11.11) * mm, "end": v(296.88, -11.11) * mm, "construction": true});
            skCircle(sketch, "E36.0.1.0", {"center": v(-227, -20.64) * mm, "radius": 1.59 * mm});
            skCircle(sketch, "E36.0.1.1", {"center": v(-176.2, -20.64) * mm, "radius": 1.59 * mm});
            skCircle(sketch, "E36.0.1.2", {"center": v(-125.4, -20.64) * mm, "radius": 1.59 * mm});
            skCircle(sketch, "E36.0.1.3", {"center": v(-230.17, -17.46) * mm, "radius": 1.59 * mm});
            skCircle(sketch, "E36.0.1.4", {"center": v(-179.37, -17.46) * mm, "radius": 1.59 * mm});
            skCircle(sketch, "E36.0.1.5", {"center": v(-128.57, -17.46) * mm, "radius": 1.59 * mm});
            skCircle(sketch, "E36.0.1.6", {"center": v(-157.15, -20.64) * mm, "radius": 1.59 * mm});
            skCircle(sketch, "E36.0.1.7", {"center": v(-106.35, -20.64) * mm, "radius": 1.59 * mm});
            skCircle(sketch, "E36.0.1.8", {"center": v(-55.55, -20.64) * mm, "radius": 1.59 * mm});
            skCircle(sketch, "E36.0.1.9", {"center": v(-4.75, -20.64) * mm, "radius": 1.59 * mm});
            skCircle(sketch, "E36.0.1.10", {"center": v(-207.95, -20.64) * mm, "radius": 1.59 * mm});
            skCircle(sketch, "E36.0.1.11", {"center": v(-258.75, -20.64) * mm, "radius": 1.59 * mm});
            skCircle(sketch, "E36.0.1.12", {"center": v(246.08, -17.46) * mm, "radius": 1.59 * mm});
            skCircle(sketch, "E36.0.1.13", {"center": v(144.48, -17.46) * mm, "radius": 1.59 * mm});
            skCircle(sketch, "E36.0.1.14", {"center": v(195.28, -17.46) * mm, "radius": 1.59 * mm});
            skCircle(sketch, "E36.0.1.15", {"center": v(-160.32, -17.46) * mm, "radius": 1.59 * mm});
            skCircle(sketch, "E36.0.1.16", {"center": v(-109.52, -17.46) * mm, "radius": 1.59 * mm});
            skCircle(sketch, "E36.0.1.17", {"center": v(-261.92, -17.46) * mm, "radius": 1.59 * mm});
            skCircle(sketch, "E36.0.1.18", {"center": v(-211.12, -17.46) * mm, "radius": 1.59 * mm});
            skCircle(sketch, "E36.0.1.19", {"center": v(252.43, -17.46) * mm, "radius": 1.59 * mm});
            skLineSegment(sketch, "E36.0.1.20", {"start": v(-293.67, -17.46) * mm, "end": v(-280.97, -17.46) * mm, "construction": true});
            skCircle(sketch, "E36.0.1.21", {"center": v(49.23, -17.46) * mm, "radius": 1.59 * mm});
            skCircle(sketch, "E36.0.1.22", {"center": v(100.03, -17.46) * mm, "radius": 1.59 * mm});
            skCircle(sketch, "E36.0.1.23", {"center": v(150.83, -17.46) * mm, "radius": 1.59 * mm});
            skCircle(sketch, "E36.0.1.24", {"center": v(201.63, -17.46) * mm, "radius": 1.59 * mm});
            skCircle(sketch, "E36.0.1.25", {"center": v(-153.97, -17.46) * mm, "radius": 1.59 * mm});
            skCircle(sketch, "E36.0.1.26", {"center": v(-103.17, -17.46) * mm, "radius": 1.59 * mm});
            skCircle(sketch, "E36.0.1.27", {"center": v(-52.37, -17.46) * mm, "radius": 1.59 * mm});
            skCircle(sketch, "E36.0.1.28", {"center": v(-1.57, -17.46) * mm, "radius": 1.59 * mm});
            skCircle(sketch, "E36.0.1.29", {"center": v(-204.77, -17.46) * mm, "radius": 1.59 * mm});
            skCircle(sketch, "E36.0.1.30", {"center": v(182.58, -17.46) * mm, "radius": 1.59 * mm});
            skCircle(sketch, "E36.0.1.31", {"center": v(233.38, -17.46) * mm, "radius": 1.59 * mm});
            skCircle(sketch, "E36.0.1.32", {"center": v(284.18, -17.46) * mm, "radius": 1.59 * mm});
            skCircle(sketch, "E36.0.1.33", {"center": v(131.78, -17.46) * mm, "radius": 1.59 * mm});
            skCircle(sketch, "E36.0.1.34", {"center": v(-223.82, -17.46) * mm, "radius": 1.59 * mm});
            skCircle(sketch, "E36.0.1.35", {"center": v(-173.02, -17.46) * mm, "radius": 1.59 * mm});
            skCircle(sketch, "E36.0.1.36", {"center": v(-122.22, -17.46) * mm, "radius": 1.59 * mm});
            skCircle(sketch, "E36.0.1.37", {"center": v(242.9, -20.64) * mm, "radius": 1.59 * mm});
            skCircle(sketch, "E36.0.1.38", {"center": v(141.3, -20.64) * mm, "radius": 1.59 * mm});
            skCircle(sketch, "E36.0.1.39", {"center": v(192.1, -20.64) * mm, "radius": 1.59 * mm});
            skCircle(sketch, "E36.0.1.40", {"center": v(-163.5, -20.64) * mm, "radius": 1.59 * mm});
            skCircle(sketch, "E36.0.1.41", {"center": v(-112.7, -20.64) * mm, "radius": 1.59 * mm});
            skCircle(sketch, "E36.0.1.42", {"center": v(-214.3, -20.64) * mm, "radius": 1.59 * mm});
            skCircle(sketch, "E36.0.1.43", {"center": v(138.13, -17.46) * mm, "radius": 1.59 * mm});
            skCircle(sketch, "E36.0.1.44", {"center": v(-217.47, -17.46) * mm, "radius": 1.59 * mm});
            skCircle(sketch, "E36.0.1.45", {"center": v(-166.67, -17.46) * mm, "radius": 1.59 * mm});
            skCircle(sketch, "E36.0.1.46", {"center": v(-115.87, -17.46) * mm, "radius": 1.59 * mm});
            skCircle(sketch, "E36.0.1.47", {"center": v(236.55, -20.64) * mm, "radius": 1.59 * mm});
            skCircle(sketch, "E36.0.1.48", {"center": v(134.95, -20.64) * mm, "radius": 1.59 * mm});
            skCircle(sketch, "E36.0.1.49", {"center": v(185.75, -20.64) * mm, "radius": 1.59 * mm});
            skCircle(sketch, "E36.0.1.50", {"center": v(188.93, -17.46) * mm, "radius": 1.59 * mm});
            skCircle(sketch, "E36.0.1.51", {"center": v(239.73, -17.46) * mm, "radius": 1.59 * mm});
            skCircle(sketch, "E36.0.1.52", {"center": v(-169.85, -20.64) * mm, "radius": 1.59 * mm});
            skCircle(sketch, "E36.0.1.53", {"center": v(-119.05, -20.64) * mm, "radius": 1.59 * mm});
            skCircle(sketch, "E36.0.1.54", {"center": v(-220.65, -20.64) * mm, "radius": 1.59 * mm});
            skCircle(sketch, "E36.0.1.55", {"center": v(-74.6, -20.64) * mm, "radius": 1.59 * mm});
            skCircle(sketch, "E36.0.1.56", {"center": v(179.4, -20.64) * mm, "radius": 1.59 * mm});
            skCircle(sketch, "E36.0.1.57", {"center": v(230.2, -20.64) * mm, "radius": 1.59 * mm});
            skCircle(sketch, "E36.0.1.58", {"center": v(281, -20.64) * mm, "radius": 1.59 * mm});
            skCircle(sketch, "E36.0.1.59", {"center": v(-23.8, -20.64) * mm, "radius": 1.59 * mm});
            skCircle(sketch, "E36.0.1.60", {"center": v(27, -20.64) * mm, "radius": 1.59 * mm});
            skCircle(sketch, "E36.0.1.61", {"center": v(77.8, -20.64) * mm, "radius": 1.59 * mm});
            skCircle(sketch, "E36.0.1.62", {"center": v(128.6, -20.64) * mm, "radius": 1.59 * mm});
            skCircle(sketch, "E36.0.1.63", {"center": v(-274.62, -17.46) * mm, "radius": 1.59 * mm});
            skCircle(sketch, "E36.0.1.64", {"center": v(-268.27, -17.46) * mm, "radius": 1.59 * mm});
            skCircle(sketch, "E36.0.1.65", {"center": v(-277.8, -20.64) * mm, "radius": 1.59 * mm});
            skCircle(sketch, "E36.0.1.66", {"center": v(173.05, -20.64) * mm, "radius": 1.59 * mm});
            skCircle(sketch, "E36.0.1.67", {"center": v(223.85, -20.64) * mm, "radius": 1.59 * mm});
            skCircle(sketch, "E36.0.1.68", {"center": v(274.65, -20.64) * mm, "radius": 1.59 * mm});
            skCircle(sketch, "E36.0.1.69", {"center": v(-30.15, -20.64) * mm, "radius": 1.59 * mm});
            skCircle(sketch, "E36.0.1.70", {"center": v(20.65, -20.64) * mm, "radius": 1.59 * mm});
            skCircle(sketch, "E36.0.1.71", {"center": v(71.45, -20.64) * mm, "radius": 1.59 * mm});
            skCircle(sketch, "E36.0.1.72", {"center": v(122.25, -20.64) * mm, "radius": 1.59 * mm});
            skCircle(sketch, "E36.0.1.73", {"center": v(-233.35, -20.64) * mm, "radius": 1.59 * mm});
            skCircle(sketch, "E36.0.1.74", {"center": v(-182.55, -20.64) * mm, "radius": 1.59 * mm});
            skCircle(sketch, "E36.0.1.75", {"center": v(-131.75, -20.64) * mm, "radius": 1.59 * mm});
            skCircle(sketch, "E36.0.1.76", {"center": v(-80.95, -20.64) * mm, "radius": 1.59 * mm});
            skCircle(sketch, "E36.0.1.77", {"center": v(-255.57, -17.46) * mm, "radius": 1.59 * mm});
            skCircle(sketch, "E36.0.1.78", {"center": v(-265.1, -20.64) * mm, "radius": 1.59 * mm});
            skCircle(sketch, "E36.0.1.79", {"center": v(-271.45, -20.64) * mm, "radius": 1.59 * mm});
            skCircle(sketch, "E36.0.1.80", {"center": v(169.88, -17.46) * mm, "radius": 1.59 * mm});
            skCircle(sketch, "E36.0.1.81", {"center": v(220.68, -17.46) * mm, "radius": 1.59 * mm});
            skCircle(sketch, "E36.0.1.82", {"center": v(271.48, -17.46) * mm, "radius": 1.59 * mm});
            skCircle(sketch, "E36.0.1.83", {"center": v(-33.32, -17.46) * mm, "radius": 1.59 * mm});
            skCircle(sketch, "E36.0.1.84", {"center": v(17.48, -17.46) * mm, "radius": 1.59 * mm});
            skCircle(sketch, "E36.0.1.85", {"center": v(68.28, -17.46) * mm, "radius": 1.59 * mm});
            skCircle(sketch, "E36.0.1.86", {"center": v(-236.52, -17.46) * mm, "radius": 1.59 * mm});
            skCircle(sketch, "E36.0.1.87", {"center": v(119.08, -17.46) * mm, "radius": 1.59 * mm});
            skCircle(sketch, "E36.0.1.88", {"center": v(-185.72, -17.46) * mm, "radius": 1.59 * mm});
            skCircle(sketch, "E36.0.1.89", {"center": v(-134.92, -17.46) * mm, "radius": 1.59 * mm});
            skCircle(sketch, "E36.0.1.90", {"center": v(-84.12, -17.46) * mm, "radius": 1.59 * mm});
            skCircle(sketch, "E36.0.1.91", {"center": v(176.23, -17.46) * mm, "radius": 1.59 * mm});
            skCircle(sketch, "E36.0.1.92", {"center": v(227.03, -17.46) * mm, "radius": 1.59 * mm});
            skCircle(sketch, "E36.0.1.93", {"center": v(277.83, -17.46) * mm, "radius": 1.59 * mm});
            skCircle(sketch, "E36.0.1.94", {"center": v(-26.97, -17.46) * mm, "radius": 1.59 * mm});
            skCircle(sketch, "E36.0.1.95", {"center": v(23.83, -17.46) * mm, "radius": 1.59 * mm});
            skCircle(sketch, "E36.0.1.96", {"center": v(74.63, -17.46) * mm, "radius": 1.59 * mm});
            skCircle(sketch, "E36.0.1.97", {"center": v(125.43, -17.46) * mm, "radius": 1.59 * mm});
            skCircle(sketch, "E36.0.1.98", {"center": v(-77.77, -17.46) * mm, "radius": 1.59 * mm});
            skCircle(sketch, "E36.0.1.99", {"center": v(268.3, -20.64) * mm, "radius": 1.59 * mm});
            skCircle(sketch, "E36.0.1.100", {"center": v(65.1, -20.64) * mm, "radius": 1.59 * mm});
            skCircle(sketch, "E36.0.1.101", {"center": v(115.9, -20.64) * mm, "radius": 1.59 * mm});
            skCircle(sketch, "E36.0.1.102", {"center": v(166.7, -20.64) * mm, "radius": 1.59 * mm});
            skCircle(sketch, "E36.0.1.103", {"center": v(217.5, -20.64) * mm, "radius": 1.59 * mm});
            skCircle(sketch, "E36.0.1.104", {"center": v(-138.1, -20.64) * mm, "radius": 1.59 * mm});
            skCircle(sketch, "E36.0.1.105", {"center": v(-87.3, -20.64) * mm, "radius": 1.59 * mm});
            skCircle(sketch, "E36.0.1.106", {"center": v(-36.5, -20.64) * mm, "radius": 1.59 * mm});
            skCircle(sketch, "E36.0.1.107", {"center": v(14.3, -20.64) * mm, "radius": 1.59 * mm});
            skCircle(sketch, "E36.0.1.108", {"center": v(-239.7, -20.64) * mm, "radius": 1.59 * mm});
            skCircle(sketch, "E36.0.1.109", {"center": v(-188.9, -20.64) * mm, "radius": 1.59 * mm});
            skCircle(sketch, "E36.0.1.110", {"center": v(261.95, -20.64) * mm, "radius": 1.59 * mm});
            skCircle(sketch, "E36.0.1.111", {"center": v(58.75, -20.64) * mm, "radius": 1.59 * mm});
            skCircle(sketch, "E36.0.1.112", {"center": v(109.55, -20.64) * mm, "radius": 1.59 * mm});
            skCircle(sketch, "E36.0.1.113", {"center": v(160.35, -20.64) * mm, "radius": 1.59 * mm});
            skCircle(sketch, "E36.0.1.114", {"center": v(211.15, -20.64) * mm, "radius": 1.59 * mm});
            skCircle(sketch, "E36.0.1.115", {"center": v(-144.45, -20.64) * mm, "radius": 1.59 * mm});
            skCircle(sketch, "E36.0.1.116", {"center": v(-93.65, -20.64) * mm, "radius": 1.59 * mm});
            skCircle(sketch, "E36.0.1.117", {"center": v(-42.85, -20.64) * mm, "radius": 1.59 * mm});
            skCircle(sketch, "E36.0.1.118", {"center": v(7.95, -20.64) * mm, "radius": 1.59 * mm});
            skCircle(sketch, "E36.0.1.119", {"center": v(-246.05, -20.64) * mm, "radius": 1.59 * mm});
            skCircle(sketch, "E36.0.1.120", {"center": v(-195.25, -20.64) * mm, "radius": 1.59 * mm});
            skCircle(sketch, "E36.0.1.121", {"center": v(258.78, -17.46) * mm, "radius": 1.59 * mm});
            skCircle(sketch, "E36.0.1.122", {"center": v(55.58, -17.46) * mm, "radius": 1.59 * mm});
            skCircle(sketch, "E36.0.1.123", {"center": v(106.38, -17.46) * mm, "radius": 1.59 * mm});
            skCircle(sketch, "E36.0.1.124", {"center": v(157.18, -17.46) * mm, "radius": 1.59 * mm});
            skCircle(sketch, "E36.0.1.125", {"center": v(207.98, -17.46) * mm, "radius": 1.59 * mm});
            skCircle(sketch, "E36.0.1.126", {"center": v(-147.62, -17.46) * mm, "radius": 1.59 * mm});
            skCircle(sketch, "E36.0.1.127", {"center": v(-96.82, -17.46) * mm, "radius": 1.59 * mm});
            skCircle(sketch, "E36.0.1.128", {"center": v(-46.02, -17.46) * mm, "radius": 1.59 * mm});
            skCircle(sketch, "E36.0.1.129", {"center": v(4.78, -17.46) * mm, "radius": 1.59 * mm});
            skCircle(sketch, "E36.0.1.130", {"center": v(-249.22, -17.46) * mm, "radius": 1.59 * mm});
            skCircle(sketch, "E36.0.1.131", {"center": v(-198.42, -17.46) * mm, "radius": 1.59 * mm});
            skCircle(sketch, "E36.0.1.132", {"center": v(265.13, -17.46) * mm, "radius": 1.59 * mm});
            skCircle(sketch, "E36.0.1.133", {"center": v(61.93, -17.46) * mm, "radius": 1.59 * mm});
            skCircle(sketch, "E36.0.1.134", {"center": v(112.73, -17.46) * mm, "radius": 1.59 * mm});
            skCircle(sketch, "E36.0.1.135", {"center": v(163.53, -17.46) * mm, "radius": 1.59 * mm});
            skCircle(sketch, "E36.0.1.136", {"center": v(214.33, -17.46) * mm, "radius": 1.59 * mm});
            skCircle(sketch, "E36.0.1.137", {"center": v(-141.27, -17.46) * mm, "radius": 1.59 * mm});
            skCircle(sketch, "E36.0.1.138", {"center": v(-90.47, -17.46) * mm, "radius": 1.59 * mm});
            skCircle(sketch, "E36.0.1.139", {"center": v(-39.67, -17.46) * mm, "radius": 1.59 * mm});
            skCircle(sketch, "E36.0.1.140", {"center": v(11.13, -17.46) * mm, "radius": 1.59 * mm});
            skCircle(sketch, "E36.0.1.141", {"center": v(-242.87, -17.46) * mm, "radius": 1.59 * mm});
            skCircle(sketch, "E36.0.1.142", {"center": v(-192.07, -17.46) * mm, "radius": 1.59 * mm});
            skCircle(sketch, "E36.0.1.143", {"center": v(255.6, -20.64) * mm, "radius": 1.59 * mm});
            skCircle(sketch, "E36.0.1.144", {"center": v(52.4, -20.64) * mm, "radius": 1.59 * mm});
            skCircle(sketch, "E36.0.1.145", {"center": v(103.2, -20.64) * mm, "radius": 1.59 * mm});
            skCircle(sketch, "E36.0.1.146", {"center": v(154, -20.64) * mm, "radius": 1.59 * mm});
            skCircle(sketch, "E36.0.1.147", {"center": v(204.8, -20.64) * mm, "radius": 1.59 * mm});
            skCircle(sketch, "E36.0.1.148", {"center": v(-150.8, -20.64) * mm, "radius": 1.59 * mm});
            skCircle(sketch, "E36.0.1.149", {"center": v(-100, -20.64) * mm, "radius": 1.59 * mm});
            skCircle(sketch, "E36.0.1.150", {"center": v(-49.2, -20.64) * mm, "radius": 1.59 * mm});
            skCircle(sketch, "E36.0.1.151", {"center": v(1.6, -20.64) * mm, "radius": 1.59 * mm});
            skCircle(sketch, "E36.0.1.152", {"center": v(-252.4, -20.64) * mm, "radius": 1.59 * mm});
            skCircle(sketch, "E36.0.1.153", {"center": v(-201.6, -20.64) * mm, "radius": 1.59 * mm});
            skCircle(sketch, "E36.0.1.154", {"center": v(198.45, -20.64) * mm, "radius": 1.59 * mm});
            skCircle(sketch, "E36.0.1.155", {"center": v(147.65, -20.64) * mm, "radius": 1.59 * mm});
            skCircle(sketch, "E36.0.1.156", {"center": v(96.85, -20.64) * mm, "radius": 1.59 * mm});
            skCircle(sketch, "E36.0.1.157", {"center": v(46.05, -20.64) * mm, "radius": 1.59 * mm});
            skCircle(sketch, "E36.0.1.158", {"center": v(300.05, -20.64) * mm, "radius": 1.59 * mm});
            skCircle(sketch, "E36.0.1.159", {"center": v(249.25, -20.64) * mm, "radius": 1.59 * mm});
            skCircle(sketch, "E36.0.1.160", {"center": v(296.88, -17.46) * mm, "radius": 1.59 * mm});
            skCircle(sketch, "E36.0.1.161", {"center": v(42.88, -17.46) * mm, "radius": 1.59 * mm});
            skCircle(sketch, "E36.0.1.162", {"center": v(93.68, -17.46) * mm, "radius": 1.59 * mm});
            skCircle(sketch, "E36.0.1.163", {"center": v(-58.72, -17.46) * mm, "radius": 1.59 * mm});
            skCircle(sketch, "E36.0.1.164", {"center": v(-7.92, -17.46) * mm, "radius": 1.59 * mm});
            skCircle(sketch, "E36.0.1.165", {"center": v(-20.62, -17.46) * mm, "radius": 1.59 * mm});
            skCircle(sketch, "E36.0.1.166", {"center": v(30.18, -17.46) * mm, "radius": 1.59 * mm});
            skCircle(sketch, "E36.0.1.167", {"center": v(80.98, -17.46) * mm, "radius": 1.59 * mm});
            skCircle(sketch, "E36.0.1.168", {"center": v(-71.42, -17.46) * mm, "radius": 1.59 * mm});
            skCircle(sketch, "E36.0.1.169", {"center": v(293.7, -20.64) * mm, "radius": 1.59 * mm});
            skCircle(sketch, "E36.0.1.170", {"center": v(39.7, -20.64) * mm, "radius": 1.59 * mm});
            skCircle(sketch, "E36.0.1.171", {"center": v(90.5, -20.64) * mm, "radius": 1.59 * mm});
            skCircle(sketch, "E36.0.1.172", {"center": v(-61.9, -20.64) * mm, "radius": 1.59 * mm});
            skCircle(sketch, "E36.0.1.173", {"center": v(-11.1, -20.64) * mm, "radius": 1.59 * mm});
            skCircle(sketch, "E36.0.1.174", {"center": v(-14.27, -17.46) * mm, "radius": 1.59 * mm});
            skCircle(sketch, "E36.0.1.175", {"center": v(36.53, -17.46) * mm, "radius": 1.59 * mm});
            skCircle(sketch, "E36.0.1.176", {"center": v(87.33, -17.46) * mm, "radius": 1.59 * mm});
            skCircle(sketch, "E36.0.1.177", {"center": v(-65.07, -17.46) * mm, "radius": 1.59 * mm});
            skCircle(sketch, "E36.0.1.178", {"center": v(287.35, -20.64) * mm, "radius": 1.59 * mm});
            skCircle(sketch, "E36.0.1.179", {"center": v(33.35, -20.64) * mm, "radius": 1.59 * mm});
            skCircle(sketch, "E36.0.1.180", {"center": v(84.15, -20.64) * mm, "radius": 1.59 * mm});
            skCircle(sketch, "E36.0.1.181", {"center": v(290.53, -17.46) * mm, "radius": 1.59 * mm});
            skCircle(sketch, "E36.0.1.182", {"center": v(-68.25, -20.64) * mm, "radius": 1.59 * mm});
            skCircle(sketch, "E36.0.1.183", {"center": v(-17.45, -20.64) * mm, "radius": 1.59 * mm});
            skCircle(sketch, "E36.0.1.184", {"center": v(-284.15, -20.64) * mm, "radius": 1.59 * mm});
            skCircle(sketch, "E36.0.1.185", {"center": v(-280.97, -17.46) * mm, "radius": 1.59 * mm});
            skLineSegment(sketch, "E36.0.1.186", {"start": v(290.53, -17.46) * mm, "end": v(296.88, -17.46) * mm, "construction": true});
            skCircle(sketch, "E36.0.1.187", {"center": v(-287.32, -17.46) * mm, "radius": 1.59 * mm});
            skLineSegment(sketch, "E36.0.1.188", {"start": v(-296.85, -20.64) * mm, "end": v(-290.5, -20.64) * mm, "construction": true});
            skCircle(sketch, "E36.0.1.189", {"center": v(-290.5, -20.64) * mm, "radius": 1.59 * mm});
            skLineSegment(sketch, "E36.0.1.190", {"start": v(-296.85, -17.46) * mm, "end": v(-296.85, -20.64) * mm, "construction": true});
            skLineSegment(sketch, "E36.0.1.191", {"start": v(-300.02, -17.46) * mm, "end": v(-293.67, -17.46) * mm, "construction": true});
            skCircle(sketch, "E36.0.1.192", {"center": v(-293.67, -17.46) * mm, "radius": 1.59 * mm});
            skCircle(sketch, "E36.0.1.193", {"center": v(-296.85, -20.64) * mm, "radius": 1.59 * mm});
            skCircle(sketch, "E36.0.1.194", {"center": v(-300.02, -17.46) * mm, "radius": 1.59 * mm});
            skCircle(sketch, "E36.0.2.0", {"center": v(-227, -26.99) * mm, "radius": 1.59 * mm});
            skCircle(sketch, "E36.0.2.1", {"center": v(-176.2, -26.99) * mm, "radius": 1.59 * mm});
            skCircle(sketch, "E36.0.2.2", {"center": v(-125.4, -26.99) * mm, "radius": 1.59 * mm});
            skCircle(sketch, "E36.0.2.3", {"center": v(-230.17, -23.81) * mm, "radius": 1.59 * mm});
            skCircle(sketch, "E36.0.2.4", {"center": v(-179.37, -23.81) * mm, "radius": 1.59 * mm});
            skCircle(sketch, "E36.0.2.5", {"center": v(-128.57, -23.81) * mm, "radius": 1.59 * mm});
            skCircle(sketch, "E36.0.2.6", {"center": v(-157.15, -26.99) * mm, "radius": 1.59 * mm});
            skCircle(sketch, "E36.0.2.7", {"center": v(-106.35, -26.99) * mm, "radius": 1.59 * mm});
            skCircle(sketch, "E36.0.2.8", {"center": v(-55.55, -26.99) * mm, "radius": 1.59 * mm});
            skCircle(sketch, "E36.0.2.9", {"center": v(-4.75, -26.99) * mm, "radius": 1.59 * mm});
            skCircle(sketch, "E36.0.2.10", {"center": v(-207.95, -26.99) * mm, "radius": 1.59 * mm});
            skCircle(sketch, "E36.0.2.11", {"center": v(-258.75, -26.99) * mm, "radius": 1.59 * mm});
            skCircle(sketch, "E36.0.2.12", {"center": v(246.08, -23.81) * mm, "radius": 1.59 * mm});
            skCircle(sketch, "E36.0.2.13", {"center": v(144.48, -23.81) * mm, "radius": 1.59 * mm});
            skCircle(sketch, "E36.0.2.14", {"center": v(195.28, -23.81) * mm, "radius": 1.59 * mm});
            skCircle(sketch, "E36.0.2.15", {"center": v(-160.32, -23.81) * mm, "radius": 1.59 * mm});
            skCircle(sketch, "E36.0.2.16", {"center": v(-109.52, -23.81) * mm, "radius": 1.59 * mm});
            skCircle(sketch, "E36.0.2.17", {"center": v(-261.92, -23.81) * mm, "radius": 1.59 * mm});
            skCircle(sketch, "E36.0.2.18", {"center": v(-211.12, -23.81) * mm, "radius": 1.59 * mm});
            skCircle(sketch, "E36.0.2.19", {"center": v(252.43, -23.81) * mm, "radius": 1.59 * mm});
            skLineSegment(sketch, "E36.0.2.20", {"start": v(-293.67, -23.81) * mm, "end": v(-280.97, -23.81) * mm, "construction": true});
            skCircle(sketch, "E36.0.2.21", {"center": v(49.23, -23.81) * mm, "radius": 1.59 * mm});
            skCircle(sketch, "E36.0.2.22", {"center": v(100.03, -23.81) * mm, "radius": 1.59 * mm});
            skCircle(sketch, "E36.0.2.23", {"center": v(150.83, -23.81) * mm, "radius": 1.59 * mm});
            skCircle(sketch, "E36.0.2.24", {"center": v(201.63, -23.81) * mm, "radius": 1.59 * mm});
            skCircle(sketch, "E36.0.2.25", {"center": v(-153.97, -23.81) * mm, "radius": 1.59 * mm});
            skCircle(sketch, "E36.0.2.26", {"center": v(-103.17, -23.81) * mm, "radius": 1.59 * mm});
            skCircle(sketch, "E36.0.2.27", {"center": v(-52.37, -23.81) * mm, "radius": 1.59 * mm});
            skCircle(sketch, "E36.0.2.28", {"center": v(-1.57, -23.81) * mm, "radius": 1.59 * mm});
            skCircle(sketch, "E36.0.2.29", {"center": v(-204.77, -23.81) * mm, "radius": 1.59 * mm});
            skCircle(sketch, "E36.0.2.30", {"center": v(182.58, -23.81) * mm, "radius": 1.59 * mm});
            skCircle(sketch, "E36.0.2.31", {"center": v(233.38, -23.81) * mm, "radius": 1.59 * mm});
            skCircle(sketch, "E36.0.2.32", {"center": v(284.18, -23.81) * mm, "radius": 1.59 * mm});
            skCircle(sketch, "E36.0.2.33", {"center": v(131.78, -23.81) * mm, "radius": 1.59 * mm});
            skCircle(sketch, "E36.0.2.34", {"center": v(-223.82, -23.81) * mm, "radius": 1.59 * mm});
            skCircle(sketch, "E36.0.2.35", {"center": v(-173.02, -23.81) * mm, "radius": 1.59 * mm});
            skCircle(sketch, "E36.0.2.36", {"center": v(-122.22, -23.81) * mm, "radius": 1.59 * mm});
            skCircle(sketch, "E36.0.2.37", {"center": v(242.9, -26.99) * mm, "radius": 1.59 * mm});
            skCircle(sketch, "E36.0.2.38", {"center": v(141.3, -26.99) * mm, "radius": 1.59 * mm});
            skCircle(sketch, "E36.0.2.39", {"center": v(192.1, -26.99) * mm, "radius": 1.59 * mm});
            skCircle(sketch, "E36.0.2.40", {"center": v(-163.5, -26.99) * mm, "radius": 1.59 * mm});
            skCircle(sketch, "E36.0.2.41", {"center": v(-112.7, -26.99) * mm, "radius": 1.59 * mm});
            skCircle(sketch, "E36.0.2.42", {"center": v(-214.3, -26.99) * mm, "radius": 1.59 * mm});
            skCircle(sketch, "E36.0.2.43", {"center": v(138.13, -23.81) * mm, "radius": 1.59 * mm});
            skCircle(sketch, "E36.0.2.44", {"center": v(-217.47, -23.81) * mm, "radius": 1.59 * mm});
            skCircle(sketch, "E36.0.2.45", {"center": v(-166.67, -23.81) * mm, "radius": 1.59 * mm});
            skCircle(sketch, "E36.0.2.46", {"center": v(-115.87, -23.81) * mm, "radius": 1.59 * mm});
            skCircle(sketch, "E36.0.2.47", {"center": v(236.55, -26.99) * mm, "radius": 1.59 * mm});
            skCircle(sketch, "E36.0.2.48", {"center": v(134.95, -26.99) * mm, "radius": 1.59 * mm});
            skCircle(sketch, "E36.0.2.49", {"center": v(185.75, -26.99) * mm, "radius": 1.59 * mm});
            skCircle(sketch, "E36.0.2.50", {"center": v(188.93, -23.81) * mm, "radius": 1.59 * mm});
            skCircle(sketch, "E36.0.2.51", {"center": v(239.73, -23.81) * mm, "radius": 1.59 * mm});
            skCircle(sketch, "E36.0.2.52", {"center": v(-169.85, -26.99) * mm, "radius": 1.59 * mm});
            skCircle(sketch, "E36.0.2.53", {"center": v(-119.05, -26.99) * mm, "radius": 1.59 * mm});
            skCircle(sketch, "E36.0.2.54", {"center": v(-220.65, -26.99) * mm, "radius": 1.59 * mm});
            skCircle(sketch, "E36.0.2.55", {"center": v(-74.6, -26.99) * mm, "radius": 1.59 * mm});
            skCircle(sketch, "E36.0.2.56", {"center": v(179.4, -26.99) * mm, "radius": 1.59 * mm});
            skCircle(sketch, "E36.0.2.57", {"center": v(230.2, -26.99) * mm, "radius": 1.59 * mm});
            skCircle(sketch, "E36.0.2.58", {"center": v(281, -26.99) * mm, "radius": 1.59 * mm});
            skCircle(sketch, "E36.0.2.59", {"center": v(-23.8, -26.99) * mm, "radius": 1.59 * mm});
            skCircle(sketch, "E36.0.2.60", {"center": v(27, -26.99) * mm, "radius": 1.59 * mm});
            skCircle(sketch, "E36.0.2.61", {"center": v(77.8, -26.99) * mm, "radius": 1.59 * mm});
            skCircle(sketch, "E36.0.2.62", {"center": v(128.6, -26.99) * mm, "radius": 1.59 * mm});
            skCircle(sketch, "E36.0.2.63", {"center": v(-274.62, -23.81) * mm, "radius": 1.59 * mm});
            skCircle(sketch, "E36.0.2.64", {"center": v(-268.27, -23.81) * mm, "radius": 1.59 * mm});
            skCircle(sketch, "E36.0.2.65", {"center": v(-277.8, -26.99) * mm, "radius": 1.59 * mm});
            skCircle(sketch, "E36.0.2.66", {"center": v(173.05, -26.99) * mm, "radius": 1.59 * mm});
            skCircle(sketch, "E36.0.2.67", {"center": v(223.85, -26.99) * mm, "radius": 1.59 * mm});
            skCircle(sketch, "E36.0.2.68", {"center": v(274.65, -26.99) * mm, "radius": 1.59 * mm});
            skCircle(sketch, "E36.0.2.69", {"center": v(-30.15, -26.99) * mm, "radius": 1.59 * mm});
            skCircle(sketch, "E36.0.2.70", {"center": v(20.65, -26.99) * mm, "radius": 1.59 * mm});
            skCircle(sketch, "E36.0.2.71", {"center": v(71.45, -26.99) * mm, "radius": 1.59 * mm});
            skCircle(sketch, "E36.0.2.72", {"center": v(122.25, -26.99) * mm, "radius": 1.59 * mm});
            skCircle(sketch, "E36.0.2.73", {"center": v(-233.35, -26.99) * mm, "radius": 1.59 * mm});
            skCircle(sketch, "E36.0.2.74", {"center": v(-182.55, -26.99) * mm, "radius": 1.59 * mm});
            skCircle(sketch, "E36.0.2.75", {"center": v(-131.75, -26.99) * mm, "radius": 1.59 * mm});
            skCircle(sketch, "E36.0.2.76", {"center": v(-80.95, -26.99) * mm, "radius": 1.59 * mm});
            skCircle(sketch, "E36.0.2.77", {"center": v(-255.57, -23.81) * mm, "radius": 1.59 * mm});
            skCircle(sketch, "E36.0.2.78", {"center": v(-265.1, -26.99) * mm, "radius": 1.59 * mm});
            skCircle(sketch, "E36.0.2.79", {"center": v(-271.45, -26.99) * mm, "radius": 1.59 * mm});
            skCircle(sketch, "E36.0.2.80", {"center": v(169.88, -23.81) * mm, "radius": 1.59 * mm});
            skCircle(sketch, "E36.0.2.81", {"center": v(220.68, -23.81) * mm, "radius": 1.59 * mm});
            skCircle(sketch, "E36.0.2.82", {"center": v(271.48, -23.81) * mm, "radius": 1.59 * mm});
            skCircle(sketch, "E36.0.2.83", {"center": v(-33.32, -23.81) * mm, "radius": 1.59 * mm});
            skCircle(sketch, "E36.0.2.84", {"center": v(17.48, -23.81) * mm, "radius": 1.59 * mm});
            skCircle(sketch, "E36.0.2.85", {"center": v(68.28, -23.81) * mm, "radius": 1.59 * mm});
            skCircle(sketch, "E36.0.2.86", {"center": v(-236.52, -23.81) * mm, "radius": 1.59 * mm});
            skCircle(sketch, "E36.0.2.87", {"center": v(119.08, -23.81) * mm, "radius": 1.59 * mm});
            skCircle(sketch, "E36.0.2.88", {"center": v(-185.72, -23.81) * mm, "radius": 1.59 * mm});
            skCircle(sketch, "E36.0.2.89", {"center": v(-134.92, -23.81) * mm, "radius": 1.59 * mm});
            skCircle(sketch, "E36.0.2.90", {"center": v(-84.12, -23.81) * mm, "radius": 1.59 * mm});
            skCircle(sketch, "E36.0.2.91", {"center": v(176.23, -23.81) * mm, "radius": 1.59 * mm});
            skCircle(sketch, "E36.0.2.92", {"center": v(227.03, -23.81) * mm, "radius": 1.59 * mm});
            skCircle(sketch, "E36.0.2.93", {"center": v(277.83, -23.81) * mm, "radius": 1.59 * mm});
            skCircle(sketch, "E36.0.2.94", {"center": v(-26.97, -23.81) * mm, "radius": 1.59 * mm});
            skCircle(sketch, "E36.0.2.95", {"center": v(23.83, -23.81) * mm, "radius": 1.59 * mm});
            skCircle(sketch, "E36.0.2.96", {"center": v(74.63, -23.81) * mm, "radius": 1.59 * mm});
            skCircle(sketch, "E36.0.2.97", {"center": v(125.43, -23.81) * mm, "radius": 1.59 * mm});
            skCircle(sketch, "E36.0.2.98", {"center": v(-77.77, -23.81) * mm, "radius": 1.59 * mm});
            skCircle(sketch, "E36.0.2.99", {"center": v(268.3, -26.99) * mm, "radius": 1.59 * mm});
            skCircle(sketch, "E36.0.2.100", {"center": v(65.1, -26.99) * mm, "radius": 1.59 * mm});
            skCircle(sketch, "E36.0.2.101", {"center": v(115.9, -26.99) * mm, "radius": 1.59 * mm});
            skCircle(sketch, "E36.0.2.102", {"center": v(166.7, -26.99) * mm, "radius": 1.59 * mm});
            skCircle(sketch, "E36.0.2.103", {"center": v(217.5, -26.99) * mm, "radius": 1.59 * mm});
            skCircle(sketch, "E36.0.2.104", {"center": v(-138.1, -26.99) * mm, "radius": 1.59 * mm});
            skCircle(sketch, "E36.0.2.105", {"center": v(-87.3, -26.99) * mm, "radius": 1.59 * mm});
            skCircle(sketch, "E36.0.2.106", {"center": v(-36.5, -26.99) * mm, "radius": 1.59 * mm});
            skCircle(sketch, "E36.0.2.107", {"center": v(14.3, -26.99) * mm, "radius": 1.59 * mm});
            skCircle(sketch, "E36.0.2.108", {"center": v(-239.7, -26.99) * mm, "radius": 1.59 * mm});
            skCircle(sketch, "E36.0.2.109", {"center": v(-188.9, -26.99) * mm, "radius": 1.59 * mm});
            skCircle(sketch, "E36.0.2.110", {"center": v(261.95, -26.99) * mm, "radius": 1.59 * mm});
            skCircle(sketch, "E36.0.2.111", {"center": v(58.75, -26.99) * mm, "radius": 1.59 * mm});
            skCircle(sketch, "E36.0.2.112", {"center": v(109.55, -26.99) * mm, "radius": 1.59 * mm});
            skCircle(sketch, "E36.0.2.113", {"center": v(160.35, -26.99) * mm, "radius": 1.59 * mm});
            skCircle(sketch, "E36.0.2.114", {"center": v(211.15, -26.99) * mm, "radius": 1.59 * mm});
            skCircle(sketch, "E36.0.2.115", {"center": v(-144.45, -26.99) * mm, "radius": 1.59 * mm});
            skCircle(sketch, "E36.0.2.116", {"center": v(-93.65, -26.99) * mm, "radius": 1.59 * mm});
            skCircle(sketch, "E36.0.2.117", {"center": v(-42.85, -26.99) * mm, "radius": 1.59 * mm});
            skCircle(sketch, "E36.0.2.118", {"center": v(7.95, -26.99) * mm, "radius": 1.59 * mm});
            skCircle(sketch, "E36.0.2.119", {"center": v(-246.05, -26.99) * mm, "radius": 1.59 * mm});
            skCircle(sketch, "E36.0.2.120", {"center": v(-195.25, -26.99) * mm, "radius": 1.59 * mm});
            skCircle(sketch, "E36.0.2.121", {"center": v(258.78, -23.81) * mm, "radius": 1.59 * mm});
            skCircle(sketch, "E36.0.2.122", {"center": v(55.58, -23.81) * mm, "radius": 1.59 * mm});
            skCircle(sketch, "E36.0.2.123", {"center": v(106.38, -23.81) * mm, "radius": 1.59 * mm});
            skCircle(sketch, "E36.0.2.124", {"center": v(157.18, -23.81) * mm, "radius": 1.59 * mm});
            skCircle(sketch, "E36.0.2.125", {"center": v(207.98, -23.81) * mm, "radius": 1.59 * mm});
            skCircle(sketch, "E36.0.2.126", {"center": v(-147.62, -23.81) * mm, "radius": 1.59 * mm});
            skCircle(sketch, "E36.0.2.127", {"center": v(-96.82, -23.81) * mm, "radius": 1.59 * mm});
            skCircle(sketch, "E36.0.2.128", {"center": v(-46.02, -23.81) * mm, "radius": 1.59 * mm});
            skCircle(sketch, "E36.0.2.129", {"center": v(4.78, -23.81) * mm, "radius": 1.59 * mm});
            skCircle(sketch, "E36.0.2.130", {"center": v(-249.22, -23.81) * mm, "radius": 1.59 * mm});
            skCircle(sketch, "E36.0.2.131", {"center": v(-198.42, -23.81) * mm, "radius": 1.59 * mm});
            skCircle(sketch, "E36.0.2.132", {"center": v(265.13, -23.81) * mm, "radius": 1.59 * mm});
            skCircle(sketch, "E36.0.2.133", {"center": v(61.93, -23.81) * mm, "radius": 1.59 * mm});
            skCircle(sketch, "E36.0.2.134", {"center": v(112.73, -23.81) * mm, "radius": 1.59 * mm});
            skCircle(sketch, "E36.0.2.135", {"center": v(163.53, -23.81) * mm, "radius": 1.59 * mm});
            skCircle(sketch, "E36.0.2.136", {"center": v(214.33, -23.81) * mm, "radius": 1.59 * mm});
            skCircle(sketch, "E36.0.2.137", {"center": v(-141.27, -23.81) * mm, "radius": 1.59 * mm});
            skCircle(sketch, "E36.0.2.138", {"center": v(-90.47, -23.81) * mm, "radius": 1.59 * mm});
            skCircle(sketch, "E36.0.2.139", {"center": v(-39.67, -23.81) * mm, "radius": 1.59 * mm});
            skCircle(sketch, "E36.0.2.140", {"center": v(11.13, -23.81) * mm, "radius": 1.59 * mm});
            skCircle(sketch, "E36.0.2.141", {"center": v(-242.87, -23.81) * mm, "radius": 1.59 * mm});
            skCircle(sketch, "E36.0.2.142", {"center": v(-192.07, -23.81) * mm, "radius": 1.59 * mm});
            skCircle(sketch, "E36.0.2.143", {"center": v(255.6, -26.99) * mm, "radius": 1.59 * mm});
            skCircle(sketch, "E36.0.2.144", {"center": v(52.4, -26.99) * mm, "radius": 1.59 * mm});
            skCircle(sketch, "E36.0.2.145", {"center": v(103.2, -26.99) * mm, "radius": 1.59 * mm});
            skCircle(sketch, "E36.0.2.146", {"center": v(154, -26.99) * mm, "radius": 1.59 * mm});
            skCircle(sketch, "E36.0.2.147", {"center": v(204.8, -26.99) * mm, "radius": 1.59 * mm});
            skCircle(sketch, "E36.0.2.148", {"center": v(-150.8, -26.99) * mm, "radius": 1.59 * mm});
            skCircle(sketch, "E36.0.2.149", {"center": v(-100, -26.99) * mm, "radius": 1.59 * mm});
            skCircle(sketch, "E36.0.2.150", {"center": v(-49.2, -26.99) * mm, "radius": 1.59 * mm});
            skCircle(sketch, "E36.0.2.151", {"center": v(1.6, -26.99) * mm, "radius": 1.59 * mm});
            skCircle(sketch, "E36.0.2.152", {"center": v(-252.4, -26.99) * mm, "radius": 1.59 * mm});
            skCircle(sketch, "E36.0.2.153", {"center": v(-201.6, -26.99) * mm, "radius": 1.59 * mm});
            skCircle(sketch, "E36.0.2.154", {"center": v(198.45, -26.99) * mm, "radius": 1.59 * mm});
            skCircle(sketch, "E36.0.2.155", {"center": v(147.65, -26.99) * mm, "radius": 1.59 * mm});
            skCircle(sketch, "E36.0.2.156", {"center": v(96.85, -26.99) * mm, "radius": 1.59 * mm});
            skCircle(sketch, "E36.0.2.157", {"center": v(46.05, -26.99) * mm, "radius": 1.59 * mm});
            skCircle(sketch, "E36.0.2.158", {"center": v(300.05, -26.99) * mm, "radius": 1.59 * mm});
            skCircle(sketch, "E36.0.2.159", {"center": v(249.25, -26.99) * mm, "radius": 1.59 * mm});
            skCircle(sketch, "E36.0.2.160", {"center": v(296.88, -23.81) * mm, "radius": 1.59 * mm});
            skCircle(sketch, "E36.0.2.161", {"center": v(42.88, -23.81) * mm, "radius": 1.59 * mm});
            skCircle(sketch, "E36.0.2.162", {"center": v(93.68, -23.81) * mm, "radius": 1.59 * mm});
            skCircle(sketch, "E36.0.2.163", {"center": v(-58.72, -23.81) * mm, "radius": 1.59 * mm});
            skCircle(sketch, "E36.0.2.164", {"center": v(-7.92, -23.81) * mm, "radius": 1.59 * mm});
            skCircle(sketch, "E36.0.2.165", {"center": v(-20.62, -23.81) * mm, "radius": 1.59 * mm});
            skCircle(sketch, "E36.0.2.166", {"center": v(30.18, -23.81) * mm, "radius": 1.59 * mm});
            skCircle(sketch, "E36.0.2.167", {"center": v(80.98, -23.81) * mm, "radius": 1.59 * mm});
            skCircle(sketch, "E36.0.2.168", {"center": v(-71.42, -23.81) * mm, "radius": 1.59 * mm});
            skCircle(sketch, "E36.0.2.169", {"center": v(293.7, -26.99) * mm, "radius": 1.59 * mm});
            skCircle(sketch, "E36.0.2.170", {"center": v(39.7, -26.99) * mm, "radius": 1.59 * mm});
            skCircle(sketch, "E36.0.2.171", {"center": v(90.5, -26.99) * mm, "radius": 1.59 * mm});
            skCircle(sketch, "E36.0.2.172", {"center": v(-61.9, -26.99) * mm, "radius": 1.59 * mm});
            skCircle(sketch, "E36.0.2.173", {"center": v(-11.1, -26.99) * mm, "radius": 1.59 * mm});
            skCircle(sketch, "E36.0.2.174", {"center": v(-14.27, -23.81) * mm, "radius": 1.59 * mm});
            skCircle(sketch, "E36.0.2.175", {"center": v(36.53, -23.81) * mm, "radius": 1.59 * mm});
            skCircle(sketch, "E36.0.2.176", {"center": v(87.33, -23.81) * mm, "radius": 1.59 * mm});
            skCircle(sketch, "E36.0.2.177", {"center": v(-65.07, -23.81) * mm, "radius": 1.59 * mm});
            skCircle(sketch, "E36.0.2.178", {"center": v(287.35, -26.99) * mm, "radius": 1.59 * mm});
            skCircle(sketch, "E36.0.2.179", {"center": v(33.35, -26.99) * mm, "radius": 1.59 * mm});
            skCircle(sketch, "E36.0.2.180", {"center": v(84.15, -26.99) * mm, "radius": 1.59 * mm});
            skCircle(sketch, "E36.0.2.181", {"center": v(290.53, -23.81) * mm, "radius": 1.59 * mm});
            skCircle(sketch, "E36.0.2.182", {"center": v(-68.25, -26.99) * mm, "radius": 1.59 * mm});
            skCircle(sketch, "E36.0.2.183", {"center": v(-17.45, -26.99) * mm, "radius": 1.59 * mm});
            skCircle(sketch, "E36.0.2.184", {"center": v(-284.15, -26.99) * mm, "radius": 1.59 * mm});
            skCircle(sketch, "E36.0.2.185", {"center": v(-280.97, -23.81) * mm, "radius": 1.59 * mm});
            skLineSegment(sketch, "E36.0.2.186", {"start": v(290.53, -23.81) * mm, "end": v(296.88, -23.81) * mm, "construction": true});
            skCircle(sketch, "E36.0.2.187", {"center": v(-287.32, -23.81) * mm, "radius": 1.59 * mm});
            skLineSegment(sketch, "E36.0.2.188", {"start": v(-296.85, -26.99) * mm, "end": v(-290.5, -26.99) * mm, "construction": true});
            skCircle(sketch, "E36.0.2.189", {"center": v(-290.5, -26.99) * mm, "radius": 1.59 * mm});
            skLineSegment(sketch, "E36.0.2.190", {"start": v(-296.85, -23.81) * mm, "end": v(-296.85, -26.99) * mm, "construction": true});
            skLineSegment(sketch, "E36.0.2.191", {"start": v(-300.02, -23.81) * mm, "end": v(-293.67, -23.81) * mm, "construction": true});
            skCircle(sketch, "E36.0.2.192", {"center": v(-293.67, -23.81) * mm, "radius": 1.59 * mm});
            skCircle(sketch, "E36.0.2.193", {"center": v(-296.85, -26.99) * mm, "radius": 1.59 * mm});
            skCircle(sketch, "E36.0.2.194", {"center": v(-300.02, -23.81) * mm, "radius": 1.59 * mm});
            skCircle(sketch, "E36.0.3.0", {"center": v(-227, -33.34) * mm, "radius": 1.59 * mm});
            skCircle(sketch, "E36.0.3.1", {"center": v(-176.2, -33.34) * mm, "radius": 1.59 * mm});
            skCircle(sketch, "E36.0.3.2", {"center": v(-125.4, -33.34) * mm, "radius": 1.59 * mm});
            skCircle(sketch, "E36.0.3.3", {"center": v(-230.17, -30.16) * mm, "radius": 1.59 * mm});
            skCircle(sketch, "E36.0.3.4", {"center": v(-179.37, -30.16) * mm, "radius": 1.59 * mm});
            skCircle(sketch, "E36.0.3.5", {"center": v(-128.57, -30.16) * mm, "radius": 1.59 * mm});
            skCircle(sketch, "E36.0.3.6", {"center": v(-157.15, -33.34) * mm, "radius": 1.59 * mm});
            skCircle(sketch, "E36.0.3.7", {"center": v(-106.35, -33.34) * mm, "radius": 1.59 * mm});
            skCircle(sketch, "E36.0.3.8", {"center": v(-55.55, -33.34) * mm, "radius": 1.59 * mm});
            skCircle(sketch, "E36.0.3.9", {"center": v(-4.75, -33.34) * mm, "radius": 1.59 * mm});
            skCircle(sketch, "E36.0.3.10", {"center": v(-207.95, -33.34) * mm, "radius": 1.59 * mm});
            skCircle(sketch, "E36.0.3.11", {"center": v(-258.75, -33.34) * mm, "radius": 1.59 * mm});
            skCircle(sketch, "E36.0.3.12", {"center": v(246.08, -30.16) * mm, "radius": 1.59 * mm});
            skCircle(sketch, "E36.0.3.13", {"center": v(144.48, -30.16) * mm, "radius": 1.59 * mm});
            skCircle(sketch, "E36.0.3.14", {"center": v(195.28, -30.16) * mm, "radius": 1.59 * mm});
            skCircle(sketch, "E36.0.3.15", {"center": v(-160.32, -30.16) * mm, "radius": 1.59 * mm});
            skCircle(sketch, "E36.0.3.16", {"center": v(-109.52, -30.16) * mm, "radius": 1.59 * mm});
            skCircle(sketch, "E36.0.3.17", {"center": v(-261.92, -30.16) * mm, "radius": 1.59 * mm});
            skCircle(sketch, "E36.0.3.18", {"center": v(-211.12, -30.16) * mm, "radius": 1.59 * mm});
            skCircle(sketch, "E36.0.3.19", {"center": v(252.43, -30.16) * mm, "radius": 1.59 * mm});
            skLineSegment(sketch, "E36.0.3.20", {"start": v(-293.67, -30.16) * mm, "end": v(-280.97, -30.16) * mm, "construction": true});
            skCircle(sketch, "E36.0.3.21", {"center": v(49.23, -30.16) * mm, "radius": 1.59 * mm});
            skCircle(sketch, "E36.0.3.22", {"center": v(100.03, -30.16) * mm, "radius": 1.59 * mm});
            skCircle(sketch, "E36.0.3.23", {"center": v(150.83, -30.16) * mm, "radius": 1.59 * mm});
            skCircle(sketch, "E36.0.3.24", {"center": v(201.63, -30.16) * mm, "radius": 1.59 * mm});
            skCircle(sketch, "E36.0.3.25", {"center": v(-153.97, -30.16) * mm, "radius": 1.59 * mm});
            skCircle(sketch, "E36.0.3.26", {"center": v(-103.17, -30.16) * mm, "radius": 1.59 * mm});
            skCircle(sketch, "E36.0.3.27", {"center": v(-52.37, -30.16) * mm, "radius": 1.59 * mm});
            skCircle(sketch, "E36.0.3.28", {"center": v(-1.57, -30.16) * mm, "radius": 1.59 * mm});
            skCircle(sketch, "E36.0.3.29", {"center": v(-204.77, -30.16) * mm, "radius": 1.59 * mm});
            skCircle(sketch, "E36.0.3.30", {"center": v(182.58, -30.16) * mm, "radius": 1.59 * mm});
            skCircle(sketch, "E36.0.3.31", {"center": v(233.38, -30.16) * mm, "radius": 1.59 * mm});
            skCircle(sketch, "E36.0.3.32", {"center": v(284.18, -30.16) * mm, "radius": 1.59 * mm});
            skCircle(sketch, "E36.0.3.33", {"center": v(131.78, -30.16) * mm, "radius": 1.59 * mm});
            skCircle(sketch, "E36.0.3.34", {"center": v(-223.82, -30.16) * mm, "radius": 1.59 * mm});
            skCircle(sketch, "E36.0.3.35", {"center": v(-173.02, -30.16) * mm, "radius": 1.59 * mm});
            skCircle(sketch, "E36.0.3.36", {"center": v(-122.22, -30.16) * mm, "radius": 1.59 * mm});
            skCircle(sketch, "E36.0.3.37", {"center": v(242.9, -33.34) * mm, "radius": 1.59 * mm});
            skCircle(sketch, "E36.0.3.38", {"center": v(141.3, -33.34) * mm, "radius": 1.59 * mm});
            skCircle(sketch, "E36.0.3.39", {"center": v(192.1, -33.34) * mm, "radius": 1.59 * mm});
            skCircle(sketch, "E36.0.3.40", {"center": v(-163.5, -33.34) * mm, "radius": 1.59 * mm});
            skCircle(sketch, "E36.0.3.41", {"center": v(-112.7, -33.34) * mm, "radius": 1.59 * mm});
            skCircle(sketch, "E36.0.3.42", {"center": v(-214.3, -33.34) * mm, "radius": 1.59 * mm});
            skCircle(sketch, "E36.0.3.43", {"center": v(138.13, -30.16) * mm, "radius": 1.59 * mm});
            skCircle(sketch, "E36.0.3.44", {"center": v(-217.47, -30.16) * mm, "radius": 1.59 * mm});
            skCircle(sketch, "E36.0.3.45", {"center": v(-166.67, -30.16) * mm, "radius": 1.59 * mm});
            skCircle(sketch, "E36.0.3.46", {"center": v(-115.87, -30.16) * mm, "radius": 1.59 * mm});
            skCircle(sketch, "E36.0.3.47", {"center": v(236.55, -33.34) * mm, "radius": 1.59 * mm});
            skCircle(sketch, "E36.0.3.48", {"center": v(134.95, -33.34) * mm, "radius": 1.59 * mm});
            skCircle(sketch, "E36.0.3.49", {"center": v(185.75, -33.34) * mm, "radius": 1.59 * mm});
            skCircle(sketch, "E36.0.3.50", {"center": v(188.93, -30.16) * mm, "radius": 1.59 * mm});
            skCircle(sketch, "E36.0.3.51", {"center": v(239.73, -30.16) * mm, "radius": 1.59 * mm});
            skCircle(sketch, "E36.0.3.52", {"center": v(-169.85, -33.34) * mm, "radius": 1.59 * mm});
            skCircle(sketch, "E36.0.3.53", {"center": v(-119.05, -33.34) * mm, "radius": 1.59 * mm});
            skCircle(sketch, "E36.0.3.54", {"center": v(-220.65, -33.34) * mm, "radius": 1.59 * mm});
            skCircle(sketch, "E36.0.3.55", {"center": v(-74.6, -33.34) * mm, "radius": 1.59 * mm});
            skCircle(sketch, "E36.0.3.56", {"center": v(179.4, -33.34) * mm, "radius": 1.59 * mm});
            skCircle(sketch, "E36.0.3.57", {"center": v(230.2, -33.34) * mm, "radius": 1.59 * mm});
            skCircle(sketch, "E36.0.3.58", {"center": v(281, -33.34) * mm, "radius": 1.59 * mm});
            skCircle(sketch, "E36.0.3.59", {"center": v(-23.8, -33.34) * mm, "radius": 1.59 * mm});
            skCircle(sketch, "E36.0.3.60", {"center": v(27, -33.34) * mm, "radius": 1.59 * mm});
            skCircle(sketch, "E36.0.3.61", {"center": v(77.8, -33.34) * mm, "radius": 1.59 * mm});
            skCircle(sketch, "E36.0.3.62", {"center": v(128.6, -33.34) * mm, "radius": 1.59 * mm});
            skCircle(sketch, "E36.0.3.63", {"center": v(-274.62, -30.16) * mm, "radius": 1.59 * mm});
            skCircle(sketch, "E36.0.3.64", {"center": v(-268.27, -30.16) * mm, "radius": 1.59 * mm});
            skCircle(sketch, "E36.0.3.65", {"center": v(-277.8, -33.34) * mm, "radius": 1.59 * mm});
            skCircle(sketch, "E36.0.3.66", {"center": v(173.05, -33.34) * mm, "radius": 1.59 * mm});
            skCircle(sketch, "E36.0.3.67", {"center": v(223.85, -33.34) * mm, "radius": 1.59 * mm});
            skCircle(sketch, "E36.0.3.68", {"center": v(274.65, -33.34) * mm, "radius": 1.59 * mm});
            skCircle(sketch, "E36.0.3.69", {"center": v(-30.15, -33.34) * mm, "radius": 1.59 * mm});
            skCircle(sketch, "E36.0.3.70", {"center": v(20.65, -33.34) * mm, "radius": 1.59 * mm});
            skCircle(sketch, "E36.0.3.71", {"center": v(71.45, -33.34) * mm, "radius": 1.59 * mm});
            skCircle(sketch, "E36.0.3.72", {"center": v(122.25, -33.34) * mm, "radius": 1.59 * mm});
            skCircle(sketch, "E36.0.3.73", {"center": v(-233.35, -33.34) * mm, "radius": 1.59 * mm});
            skCircle(sketch, "E36.0.3.74", {"center": v(-182.55, -33.34) * mm, "radius": 1.59 * mm});
            skCircle(sketch, "E36.0.3.75", {"center": v(-131.75, -33.34) * mm, "radius": 1.59 * mm});
            skCircle(sketch, "E36.0.3.76", {"center": v(-80.95, -33.34) * mm, "radius": 1.59 * mm});
            skCircle(sketch, "E36.0.3.77", {"center": v(-255.57, -30.16) * mm, "radius": 1.59 * mm});
            skCircle(sketch, "E36.0.3.78", {"center": v(-265.1, -33.34) * mm, "radius": 1.59 * mm});
            skCircle(sketch, "E36.0.3.79", {"center": v(-271.45, -33.34) * mm, "radius": 1.59 * mm});
            skCircle(sketch, "E36.0.3.80", {"center": v(169.88, -30.16) * mm, "radius": 1.59 * mm});
            skCircle(sketch, "E36.0.3.81", {"center": v(220.68, -30.16) * mm, "radius": 1.59 * mm});
            skCircle(sketch, "E36.0.3.82", {"center": v(271.48, -30.16) * mm, "radius": 1.59 * mm});
            skCircle(sketch, "E36.0.3.83", {"center": v(-33.32, -30.16) * mm, "radius": 1.59 * mm});
            skCircle(sketch, "E36.0.3.84", {"center": v(17.48, -30.16) * mm, "radius": 1.59 * mm});
            skCircle(sketch, "E36.0.3.85", {"center": v(68.28, -30.16) * mm, "radius": 1.59 * mm});
            skCircle(sketch, "E36.0.3.86", {"center": v(-236.52, -30.16) * mm, "radius": 1.59 * mm});
            skCircle(sketch, "E36.0.3.87", {"center": v(119.08, -30.16) * mm, "radius": 1.59 * mm});
            skCircle(sketch, "E36.0.3.88", {"center": v(-185.72, -30.16) * mm, "radius": 1.59 * mm});
            skCircle(sketch, "E36.0.3.89", {"center": v(-134.92, -30.16) * mm, "radius": 1.59 * mm});
            skCircle(sketch, "E36.0.3.90", {"center": v(-84.12, -30.16) * mm, "radius": 1.59 * mm});
            skCircle(sketch, "E36.0.3.91", {"center": v(176.23, -30.16) * mm, "radius": 1.59 * mm});
            skCircle(sketch, "E36.0.3.92", {"center": v(227.03, -30.16) * mm, "radius": 1.59 * mm});
            skCircle(sketch, "E36.0.3.93", {"center": v(277.83, -30.16) * mm, "radius": 1.59 * mm});
            skCircle(sketch, "E36.0.3.94", {"center": v(-26.97, -30.16) * mm, "radius": 1.59 * mm});
            skCircle(sketch, "E36.0.3.95", {"center": v(23.83, -30.16) * mm, "radius": 1.59 * mm});
            skCircle(sketch, "E36.0.3.96", {"center": v(74.63, -30.16) * mm, "radius": 1.59 * mm});
            skCircle(sketch, "E36.0.3.97", {"center": v(125.43, -30.16) * mm, "radius": 1.59 * mm});
            skCircle(sketch, "E36.0.3.98", {"center": v(-77.77, -30.16) * mm, "radius": 1.59 * mm});
            skCircle(sketch, "E36.0.3.99", {"center": v(268.3, -33.34) * mm, "radius": 1.59 * mm});
            skCircle(sketch, "E36.0.3.100", {"center": v(65.1, -33.34) * mm, "radius": 1.59 * mm});
            skCircle(sketch, "E36.0.3.101", {"center": v(115.9, -33.34) * mm, "radius": 1.59 * mm});
            skCircle(sketch, "E36.0.3.102", {"center": v(166.7, -33.34) * mm, "radius": 1.59 * mm});
            skCircle(sketch, "E36.0.3.103", {"center": v(217.5, -33.34) * mm, "radius": 1.59 * mm});
            skCircle(sketch, "E36.0.3.104", {"center": v(-138.1, -33.34) * mm, "radius": 1.59 * mm});
            skCircle(sketch, "E36.0.3.105", {"center": v(-87.3, -33.34) * mm, "radius": 1.59 * mm});
            skCircle(sketch, "E36.0.3.106", {"center": v(-36.5, -33.34) * mm, "radius": 1.59 * mm});
            skCircle(sketch, "E36.0.3.107", {"center": v(14.3, -33.34) * mm, "radius": 1.59 * mm});
            skCircle(sketch, "E36.0.3.108", {"center": v(-239.7, -33.34) * mm, "radius": 1.59 * mm});
            skCircle(sketch, "E36.0.3.109", {"center": v(-188.9, -33.34) * mm, "radius": 1.59 * mm});
            skCircle(sketch, "E36.0.3.110", {"center": v(261.95, -33.34) * mm, "radius": 1.59 * mm});
            skCircle(sketch, "E36.0.3.111", {"center": v(58.75, -33.34) * mm, "radius": 1.59 * mm});
            skCircle(sketch, "E36.0.3.112", {"center": v(109.55, -33.34) * mm, "radius": 1.59 * mm});
            skCircle(sketch, "E36.0.3.113", {"center": v(160.35, -33.34) * mm, "radius": 1.59 * mm});
            skCircle(sketch, "E36.0.3.114", {"center": v(211.15, -33.34) * mm, "radius": 1.59 * mm});
            skCircle(sketch, "E36.0.3.115", {"center": v(-144.45, -33.34) * mm, "radius": 1.59 * mm});
            skCircle(sketch, "E36.0.3.116", {"center": v(-93.65, -33.34) * mm, "radius": 1.59 * mm});
            skCircle(sketch, "E36.0.3.117", {"center": v(-42.85, -33.34) * mm, "radius": 1.59 * mm});
            skCircle(sketch, "E36.0.3.118", {"center": v(7.95, -33.34) * mm, "radius": 1.59 * mm});
            skCircle(sketch, "E36.0.3.119", {"center": v(-246.05, -33.34) * mm, "radius": 1.59 * mm});
            skCircle(sketch, "E36.0.3.120", {"center": v(-195.25, -33.34) * mm, "radius": 1.59 * mm});
            skCircle(sketch, "E36.0.3.121", {"center": v(258.78, -30.16) * mm, "radius": 1.59 * mm});
            skCircle(sketch, "E36.0.3.122", {"center": v(55.58, -30.16) * mm, "radius": 1.59 * mm});
            skCircle(sketch, "E36.0.3.123", {"center": v(106.38, -30.16) * mm, "radius": 1.59 * mm});
            skCircle(sketch, "E36.0.3.124", {"center": v(157.18, -30.16) * mm, "radius": 1.59 * mm});
            skCircle(sketch, "E36.0.3.125", {"center": v(207.98, -30.16) * mm, "radius": 1.59 * mm});
            skCircle(sketch, "E36.0.3.126", {"center": v(-147.62, -30.16) * mm, "radius": 1.59 * mm});
            skCircle(sketch, "E36.0.3.127", {"center": v(-96.82, -30.16) * mm, "radius": 1.59 * mm});
            skCircle(sketch, "E36.0.3.128", {"center": v(-46.02, -30.16) * mm, "radius": 1.59 * mm});
            skCircle(sketch, "E36.0.3.129", {"center": v(4.78, -30.16) * mm, "radius": 1.59 * mm});
            skCircle(sketch, "E36.0.3.130", {"center": v(-249.22, -30.16) * mm, "radius": 1.59 * mm});
            skCircle(sketch, "E36.0.3.131", {"center": v(-198.42, -30.16) * mm, "radius": 1.59 * mm});
            skCircle(sketch, "E36.0.3.132", {"center": v(265.13, -30.16) * mm, "radius": 1.59 * mm});
            skCircle(sketch, "E36.0.3.133", {"center": v(61.93, -30.16) * mm, "radius": 1.59 * mm});
            skCircle(sketch, "E36.0.3.134", {"center": v(112.73, -30.16) * mm, "radius": 1.59 * mm});
            skCircle(sketch, "E36.0.3.135", {"center": v(163.53, -30.16) * mm, "radius": 1.59 * mm});
            skCircle(sketch, "E36.0.3.136", {"center": v(214.33, -30.16) * mm, "radius": 1.59 * mm});
            skCircle(sketch, "E36.0.3.137", {"center": v(-141.27, -30.16) * mm, "radius": 1.59 * mm});
            skCircle(sketch, "E36.0.3.138", {"center": v(-90.47, -30.16) * mm, "radius": 1.59 * mm});
            skCircle(sketch, "E36.0.3.139", {"center": v(-39.67, -30.16) * mm, "radius": 1.59 * mm});
            skCircle(sketch, "E36.0.3.140", {"center": v(11.13, -30.16) * mm, "radius": 1.59 * mm});
            skCircle(sketch, "E36.0.3.141", {"center": v(-242.87, -30.16) * mm, "radius": 1.59 * mm});
            skCircle(sketch, "E36.0.3.142", {"center": v(-192.07, -30.16) * mm, "radius": 1.59 * mm});
            skCircle(sketch, "E36.0.3.143", {"center": v(255.6, -33.34) * mm, "radius": 1.59 * mm});
            skCircle(sketch, "E36.0.3.144", {"center": v(52.4, -33.34) * mm, "radius": 1.59 * mm});
            skCircle(sketch, "E36.0.3.145", {"center": v(103.2, -33.34) * mm, "radius": 1.59 * mm});
            skCircle(sketch, "E36.0.3.146", {"center": v(154, -33.34) * mm, "radius": 1.59 * mm});
            skCircle(sketch, "E36.0.3.147", {"center": v(204.8, -33.34) * mm, "radius": 1.59 * mm});
            skCircle(sketch, "E36.0.3.148", {"center": v(-150.8, -33.34) * mm, "radius": 1.59 * mm});
            skCircle(sketch, "E36.0.3.149", {"center": v(-100, -33.34) * mm, "radius": 1.59 * mm});
            skCircle(sketch, "E36.0.3.150", {"center": v(-49.2, -33.34) * mm, "radius": 1.59 * mm});
            skCircle(sketch, "E36.0.3.151", {"center": v(1.6, -33.34) * mm, "radius": 1.59 * mm});
            skCircle(sketch, "E36.0.3.152", {"center": v(-252.4, -33.34) * mm, "radius": 1.59 * mm});
            skCircle(sketch, "E36.0.3.153", {"center": v(-201.6, -33.34) * mm, "radius": 1.59 * mm});
            skCircle(sketch, "E36.0.3.154", {"center": v(198.45, -33.34) * mm, "radius": 1.59 * mm});
            skCircle(sketch, "E36.0.3.155", {"center": v(147.65, -33.34) * mm, "radius": 1.59 * mm});
            skCircle(sketch, "E36.0.3.156", {"center": v(96.85, -33.34) * mm, "radius": 1.59 * mm});
            skCircle(sketch, "E36.0.3.157", {"center": v(46.05, -33.34) * mm, "radius": 1.59 * mm});
            skCircle(sketch, "E36.0.3.158", {"center": v(300.05, -33.34) * mm, "radius": 1.59 * mm});
            skCircle(sketch, "E36.0.3.159", {"center": v(249.25, -33.34) * mm, "radius": 1.59 * mm});
            skCircle(sketch, "E36.0.3.160", {"center": v(296.88, -30.16) * mm, "radius": 1.59 * mm});
            skCircle(sketch, "E36.0.3.161", {"center": v(42.88, -30.16) * mm, "radius": 1.59 * mm});
            skCircle(sketch, "E36.0.3.162", {"center": v(93.68, -30.16) * mm, "radius": 1.59 * mm});
            skCircle(sketch, "E36.0.3.163", {"center": v(-58.72, -30.16) * mm, "radius": 1.59 * mm});
            skCircle(sketch, "E36.0.3.164", {"center": v(-7.92, -30.16) * mm, "radius": 1.59 * mm});
            skCircle(sketch, "E36.0.3.165", {"center": v(-20.62, -30.16) * mm, "radius": 1.59 * mm});
            skCircle(sketch, "E36.0.3.166", {"center": v(30.18, -30.16) * mm, "radius": 1.59 * mm});
            skCircle(sketch, "E36.0.3.167", {"center": v(80.98, -30.16) * mm, "radius": 1.59 * mm});
            skCircle(sketch, "E36.0.3.168", {"center": v(-71.42, -30.16) * mm, "radius": 1.59 * mm});
            skCircle(sketch, "E36.0.3.169", {"center": v(293.7, -33.34) * mm, "radius": 1.59 * mm});
            skCircle(sketch, "E36.0.3.170", {"center": v(39.7, -33.34) * mm, "radius": 1.59 * mm});
            skCircle(sketch, "E36.0.3.171", {"center": v(90.5, -33.34) * mm, "radius": 1.59 * mm});
            skCircle(sketch, "E36.0.3.172", {"center": v(-61.9, -33.34) * mm, "radius": 1.59 * mm});
            skCircle(sketch, "E36.0.3.173", {"center": v(-11.1, -33.34) * mm, "radius": 1.59 * mm});
            skCircle(sketch, "E36.0.3.174", {"center": v(-14.27, -30.16) * mm, "radius": 1.59 * mm});
            skCircle(sketch, "E36.0.3.175", {"center": v(36.53, -30.16) * mm, "radius": 1.59 * mm});
            skCircle(sketch, "E36.0.3.176", {"center": v(87.33, -30.16) * mm, "radius": 1.59 * mm});
            skCircle(sketch, "E36.0.3.177", {"center": v(-65.07, -30.16) * mm, "radius": 1.59 * mm});
            skCircle(sketch, "E36.0.3.178", {"center": v(287.35, -33.34) * mm, "radius": 1.59 * mm});
            skCircle(sketch, "E36.0.3.179", {"center": v(33.35, -33.34) * mm, "radius": 1.59 * mm});
            skCircle(sketch, "E36.0.3.180", {"center": v(84.15, -33.34) * mm, "radius": 1.59 * mm});
            skCircle(sketch, "E36.0.3.181", {"center": v(290.53, -30.16) * mm, "radius": 1.59 * mm});
            skCircle(sketch, "E36.0.3.182", {"center": v(-68.25, -33.34) * mm, "radius": 1.59 * mm});
            skCircle(sketch, "E36.0.3.183", {"center": v(-17.45, -33.34) * mm, "radius": 1.59 * mm});
            skCircle(sketch, "E36.0.3.184", {"center": v(-284.15, -33.34) * mm, "radius": 1.59 * mm});
            skCircle(sketch, "E36.0.3.185", {"center": v(-280.97, -30.16) * mm, "radius": 1.59 * mm});
            skLineSegment(sketch, "E36.0.3.186", {"start": v(290.53, -30.16) * mm, "end": v(296.88, -30.16) * mm, "construction": true});
            skCircle(sketch, "E36.0.3.187", {"center": v(-287.32, -30.16) * mm, "radius": 1.59 * mm});
            skLineSegment(sketch, "E36.0.3.188", {"start": v(-296.85, -33.34) * mm, "end": v(-290.5, -33.34) * mm, "construction": true});
            skCircle(sketch, "E36.0.3.189", {"center": v(-290.5, -33.34) * mm, "radius": 1.59 * mm});
            skLineSegment(sketch, "E36.0.3.190", {"start": v(-296.85, -30.16) * mm, "end": v(-296.85, -33.34) * mm, "construction": true});
            skLineSegment(sketch, "E36.0.3.191", {"start": v(-300.02, -30.16) * mm, "end": v(-293.67, -30.16) * mm, "construction": true});
            skCircle(sketch, "E36.0.3.192", {"center": v(-293.67, -30.16) * mm, "radius": 1.59 * mm});
            skCircle(sketch, "E36.0.3.193", {"center": v(-296.85, -33.34) * mm, "radius": 1.59 * mm});
            skCircle(sketch, "E36.0.3.194", {"center": v(-300.02, -30.16) * mm, "radius": 1.59 * mm});
            skCircle(sketch, "E36.0.4.0", {"center": v(-227, -39.69) * mm, "radius": 1.59 * mm});
            skCircle(sketch, "E36.0.4.1", {"center": v(-176.2, -39.69) * mm, "radius": 1.59 * mm});
            skCircle(sketch, "E36.0.4.2", {"center": v(-125.4, -39.69) * mm, "radius": 1.59 * mm});
            skCircle(sketch, "E36.0.4.3", {"center": v(-230.17, -36.51) * mm, "radius": 1.59 * mm});
            skCircle(sketch, "E36.0.4.4", {"center": v(-179.37, -36.51) * mm, "radius": 1.59 * mm});
            skCircle(sketch, "E36.0.4.5", {"center": v(-128.57, -36.51) * mm, "radius": 1.59 * mm});
            skCircle(sketch, "E36.0.4.6", {"center": v(-157.15, -39.69) * mm, "radius": 1.59 * mm});
            skCircle(sketch, "E36.0.4.7", {"center": v(-106.35, -39.69) * mm, "radius": 1.59 * mm});
            skCircle(sketch, "E36.0.4.8", {"center": v(-55.55, -39.69) * mm, "radius": 1.59 * mm});
            skCircle(sketch, "E36.0.4.9", {"center": v(-4.75, -39.69) * mm, "radius": 1.59 * mm});
            skCircle(sketch, "E36.0.4.10", {"center": v(-207.95, -39.69) * mm, "radius": 1.59 * mm});
            skCircle(sketch, "E36.0.4.11", {"center": v(-258.75, -39.69) * mm, "radius": 1.59 * mm});
            skCircle(sketch, "E36.0.4.12", {"center": v(246.08, -36.51) * mm, "radius": 1.59 * mm});
            skCircle(sketch, "E36.0.4.13", {"center": v(144.48, -36.51) * mm, "radius": 1.59 * mm});
            skCircle(sketch, "E36.0.4.14", {"center": v(195.28, -36.51) * mm, "radius": 1.59 * mm});
            skCircle(sketch, "E36.0.4.15", {"center": v(-160.32, -36.51) * mm, "radius": 1.59 * mm});
            skCircle(sketch, "E36.0.4.16", {"center": v(-109.52, -36.51) * mm, "radius": 1.59 * mm});
            skCircle(sketch, "E36.0.4.17", {"center": v(-261.92, -36.51) * mm, "radius": 1.59 * mm});
            skCircle(sketch, "E36.0.4.18", {"center": v(-211.12, -36.51) * mm, "radius": 1.59 * mm});
            skCircle(sketch, "E36.0.4.19", {"center": v(252.43, -36.51) * mm, "radius": 1.59 * mm});
            skLineSegment(sketch, "E36.0.4.20", {"start": v(-293.67, -36.51) * mm, "end": v(-280.97, -36.51) * mm, "construction": true});
            skCircle(sketch, "E36.0.4.21", {"center": v(49.23, -36.51) * mm, "radius": 1.59 * mm});
            skCircle(sketch, "E36.0.4.22", {"center": v(100.03, -36.51) * mm, "radius": 1.59 * mm});
            skCircle(sketch, "E36.0.4.23", {"center": v(150.83, -36.51) * mm, "radius": 1.59 * mm});
            skCircle(sketch, "E36.0.4.24", {"center": v(201.63, -36.51) * mm, "radius": 1.59 * mm});
            skCircle(sketch, "E36.0.4.25", {"center": v(-153.97, -36.51) * mm, "radius": 1.59 * mm});
            skCircle(sketch, "E36.0.4.26", {"center": v(-103.17, -36.51) * mm, "radius": 1.59 * mm});
            skCircle(sketch, "E36.0.4.27", {"center": v(-52.37, -36.51) * mm, "radius": 1.59 * mm});
            skCircle(sketch, "E36.0.4.28", {"center": v(-1.57, -36.51) * mm, "radius": 1.59 * mm});
            skCircle(sketch, "E36.0.4.29", {"center": v(-204.77, -36.51) * mm, "radius": 1.59 * mm});
            skCircle(sketch, "E36.0.4.30", {"center": v(182.58, -36.51) * mm, "radius": 1.59 * mm});
            skCircle(sketch, "E36.0.4.31", {"center": v(233.38, -36.51) * mm, "radius": 1.59 * mm});
            skCircle(sketch, "E36.0.4.32", {"center": v(284.18, -36.51) * mm, "radius": 1.59 * mm});
            skCircle(sketch, "E36.0.4.33", {"center": v(131.78, -36.51) * mm, "radius": 1.59 * mm});
            skCircle(sketch, "E36.0.4.34", {"center": v(-223.82, -36.51) * mm, "radius": 1.59 * mm});
            skCircle(sketch, "E36.0.4.35", {"center": v(-173.02, -36.51) * mm, "radius": 1.59 * mm});
            skCircle(sketch, "E36.0.4.36", {"center": v(-122.22, -36.51) * mm, "radius": 1.59 * mm});
            skCircle(sketch, "E36.0.4.37", {"center": v(242.9, -39.69) * mm, "radius": 1.59 * mm});
            skCircle(sketch, "E36.0.4.38", {"center": v(141.3, -39.69) * mm, "radius": 1.59 * mm});
            skCircle(sketch, "E36.0.4.39", {"center": v(192.1, -39.69) * mm, "radius": 1.59 * mm});
            skCircle(sketch, "E36.0.4.40", {"center": v(-163.5, -39.69) * mm, "radius": 1.59 * mm});
            skCircle(sketch, "E36.0.4.41", {"center": v(-112.7, -39.69) * mm, "radius": 1.59 * mm});
            skCircle(sketch, "E36.0.4.42", {"center": v(-214.3, -39.69) * mm, "radius": 1.59 * mm});
            skCircle(sketch, "E36.0.4.43", {"center": v(138.13, -36.51) * mm, "radius": 1.59 * mm});
            skCircle(sketch, "E36.0.4.44", {"center": v(-217.47, -36.51) * mm, "radius": 1.59 * mm});
            skCircle(sketch, "E36.0.4.45", {"center": v(-166.67, -36.51) * mm, "radius": 1.59 * mm});
            skCircle(sketch, "E36.0.4.46", {"center": v(-115.87, -36.51) * mm, "radius": 1.59 * mm});
            skCircle(sketch, "E36.0.4.47", {"center": v(236.55, -39.69) * mm, "radius": 1.59 * mm});
            skCircle(sketch, "E36.0.4.48", {"center": v(134.95, -39.69) * mm, "radius": 1.59 * mm});
            skCircle(sketch, "E36.0.4.49", {"center": v(185.75, -39.69) * mm, "radius": 1.59 * mm});
            skCircle(sketch, "E36.0.4.50", {"center": v(188.93, -36.51) * mm, "radius": 1.59 * mm});
            skCircle(sketch, "E36.0.4.51", {"center": v(239.73, -36.51) * mm, "radius": 1.59 * mm});
            skCircle(sketch, "E36.0.4.52", {"center": v(-169.85, -39.69) * mm, "radius": 1.59 * mm});
            skCircle(sketch, "E36.0.4.53", {"center": v(-119.05, -39.69) * mm, "radius": 1.59 * mm});
            skCircle(sketch, "E36.0.4.54", {"center": v(-220.65, -39.69) * mm, "radius": 1.59 * mm});
            skCircle(sketch, "E36.0.4.55", {"center": v(-74.6, -39.69) * mm, "radius": 1.59 * mm});
            skCircle(sketch, "E36.0.4.56", {"center": v(179.4, -39.69) * mm, "radius": 1.59 * mm});
            skCircle(sketch, "E36.0.4.57", {"center": v(230.2, -39.69) * mm, "radius": 1.59 * mm});
            skCircle(sketch, "E36.0.4.58", {"center": v(281, -39.69) * mm, "radius": 1.59 * mm});
            skCircle(sketch, "E36.0.4.59", {"center": v(-23.8, -39.69) * mm, "radius": 1.59 * mm});
            skCircle(sketch, "E36.0.4.60", {"center": v(27, -39.69) * mm, "radius": 1.59 * mm});
            skCircle(sketch, "E36.0.4.61", {"center": v(77.8, -39.69) * mm, "radius": 1.59 * mm});
            skCircle(sketch, "E36.0.4.62", {"center": v(128.6, -39.69) * mm, "radius": 1.59 * mm});
            skCircle(sketch, "E36.0.4.63", {"center": v(-274.62, -36.51) * mm, "radius": 1.59 * mm});
            skCircle(sketch, "E36.0.4.64", {"center": v(-268.27, -36.51) * mm, "radius": 1.59 * mm});
            skCircle(sketch, "E36.0.4.65", {"center": v(-277.8, -39.69) * mm, "radius": 1.59 * mm});
            skCircle(sketch, "E36.0.4.66", {"center": v(173.05, -39.69) * mm, "radius": 1.59 * mm});
            skCircle(sketch, "E36.0.4.67", {"center": v(223.85, -39.69) * mm, "radius": 1.59 * mm});
            skCircle(sketch, "E36.0.4.68", {"center": v(274.65, -39.69) * mm, "radius": 1.59 * mm});
            skCircle(sketch, "E36.0.4.69", {"center": v(-30.15, -39.69) * mm, "radius": 1.59 * mm});
            skCircle(sketch, "E36.0.4.70", {"center": v(20.65, -39.69) * mm, "radius": 1.59 * mm});
            skCircle(sketch, "E36.0.4.71", {"center": v(71.45, -39.69) * mm, "radius": 1.59 * mm});
            skCircle(sketch, "E36.0.4.72", {"center": v(122.25, -39.69) * mm, "radius": 1.59 * mm});
            skCircle(sketch, "E36.0.4.73", {"center": v(-233.35, -39.69) * mm, "radius": 1.59 * mm});
            skCircle(sketch, "E36.0.4.74", {"center": v(-182.55, -39.69) * mm, "radius": 1.59 * mm});
            skCircle(sketch, "E36.0.4.75", {"center": v(-131.75, -39.69) * mm, "radius": 1.59 * mm});
            skCircle(sketch, "E36.0.4.76", {"center": v(-80.95, -39.69) * mm, "radius": 1.59 * mm});
            skCircle(sketch, "E36.0.4.77", {"center": v(-255.57, -36.51) * mm, "radius": 1.59 * mm});
            skCircle(sketch, "E36.0.4.78", {"center": v(-265.1, -39.69) * mm, "radius": 1.59 * mm});
            skCircle(sketch, "E36.0.4.79", {"center": v(-271.45, -39.69) * mm, "radius": 1.59 * mm});
            skCircle(sketch, "E36.0.4.80", {"center": v(169.88, -36.51) * mm, "radius": 1.59 * mm});
            skCircle(sketch, "E36.0.4.81", {"center": v(220.68, -36.51) * mm, "radius": 1.59 * mm});
            skCircle(sketch, "E36.0.4.82", {"center": v(271.48, -36.51) * mm, "radius": 1.59 * mm});
            skCircle(sketch, "E36.0.4.83", {"center": v(-33.32, -36.51) * mm, "radius": 1.59 * mm});
            skCircle(sketch, "E36.0.4.84", {"center": v(17.48, -36.51) * mm, "radius": 1.59 * mm});
            skCircle(sketch, "E36.0.4.85", {"center": v(68.28, -36.51) * mm, "radius": 1.59 * mm});
            skCircle(sketch, "E36.0.4.86", {"center": v(-236.52, -36.51) * mm, "radius": 1.59 * mm});
            skCircle(sketch, "E36.0.4.87", {"center": v(119.08, -36.51) * mm, "radius": 1.59 * mm});
            skCircle(sketch, "E36.0.4.88", {"center": v(-185.72, -36.51) * mm, "radius": 1.59 * mm});
            skCircle(sketch, "E36.0.4.89", {"center": v(-134.92, -36.51) * mm, "radius": 1.59 * mm});
            skCircle(sketch, "E36.0.4.90", {"center": v(-84.12, -36.51) * mm, "radius": 1.59 * mm});
            skCircle(sketch, "E36.0.4.91", {"center": v(176.23, -36.51) * mm, "radius": 1.59 * mm});
            skCircle(sketch, "E36.0.4.92", {"center": v(227.03, -36.51) * mm, "radius": 1.59 * mm});
            skCircle(sketch, "E36.0.4.93", {"center": v(277.83, -36.51) * mm, "radius": 1.59 * mm});
            skCircle(sketch, "E36.0.4.94", {"center": v(-26.97, -36.51) * mm, "radius": 1.59 * mm});
            skCircle(sketch, "E36.0.4.95", {"center": v(23.83, -36.51) * mm, "radius": 1.59 * mm});
            skCircle(sketch, "E36.0.4.96", {"center": v(74.63, -36.51) * mm, "radius": 1.59 * mm});
            skCircle(sketch, "E36.0.4.97", {"center": v(125.43, -36.51) * mm, "radius": 1.59 * mm});
            skCircle(sketch, "E36.0.4.98", {"center": v(-77.77, -36.51) * mm, "radius": 1.59 * mm});
            skCircle(sketch, "E36.0.4.99", {"center": v(268.3, -39.69) * mm, "radius": 1.59 * mm});
            skCircle(sketch, "E36.0.4.100", {"center": v(65.1, -39.69) * mm, "radius": 1.59 * mm});
            skCircle(sketch, "E36.0.4.101", {"center": v(115.9, -39.69) * mm, "radius": 1.59 * mm});
            skCircle(sketch, "E36.0.4.102", {"center": v(166.7, -39.69) * mm, "radius": 1.59 * mm});
            skCircle(sketch, "E36.0.4.103", {"center": v(217.5, -39.69) * mm, "radius": 1.59 * mm});
            skCircle(sketch, "E36.0.4.104", {"center": v(-138.1, -39.69) * mm, "radius": 1.59 * mm});
            skCircle(sketch, "E36.0.4.105", {"center": v(-87.3, -39.69) * mm, "radius": 1.59 * mm});
            skCircle(sketch, "E36.0.4.106", {"center": v(-36.5, -39.69) * mm, "radius": 1.59 * mm});
            skCircle(sketch, "E36.0.4.107", {"center": v(14.3, -39.69) * mm, "radius": 1.59 * mm});
            skCircle(sketch, "E36.0.4.108", {"center": v(-239.7, -39.69) * mm, "radius": 1.59 * mm});
            skCircle(sketch, "E36.0.4.109", {"center": v(-188.9, -39.69) * mm, "radius": 1.59 * mm});
            skCircle(sketch, "E36.0.4.110", {"center": v(261.95, -39.69) * mm, "radius": 1.59 * mm});
            skCircle(sketch, "E36.0.4.111", {"center": v(58.75, -39.69) * mm, "radius": 1.59 * mm});
            skCircle(sketch, "E36.0.4.112", {"center": v(109.55, -39.69) * mm, "radius": 1.59 * mm});
            skCircle(sketch, "E36.0.4.113", {"center": v(160.35, -39.69) * mm, "radius": 1.59 * mm});
            skCircle(sketch, "E36.0.4.114", {"center": v(211.15, -39.69) * mm, "radius": 1.59 * mm});
            skCircle(sketch, "E36.0.4.115", {"center": v(-144.45, -39.69) * mm, "radius": 1.59 * mm});
            skCircle(sketch, "E36.0.4.116", {"center": v(-93.65, -39.69) * mm, "radius": 1.59 * mm});
            skCircle(sketch, "E36.0.4.117", {"center": v(-42.85, -39.69) * mm, "radius": 1.59 * mm});
            skCircle(sketch, "E36.0.4.118", {"center": v(7.95, -39.69) * mm, "radius": 1.59 * mm});
            skCircle(sketch, "E36.0.4.119", {"center": v(-246.05, -39.69) * mm, "radius": 1.59 * mm});
            skCircle(sketch, "E36.0.4.120", {"center": v(-195.25, -39.69) * mm, "radius": 1.59 * mm});
            skCircle(sketch, "E36.0.4.121", {"center": v(258.78, -36.51) * mm, "radius": 1.59 * mm});
            skCircle(sketch, "E36.0.4.122", {"center": v(55.58, -36.51) * mm, "radius": 1.59 * mm});
            skCircle(sketch, "E36.0.4.123", {"center": v(106.38, -36.51) * mm, "radius": 1.59 * mm});
            skCircle(sketch, "E36.0.4.124", {"center": v(157.18, -36.51) * mm, "radius": 1.59 * mm});
            skCircle(sketch, "E36.0.4.125", {"center": v(207.98, -36.51) * mm, "radius": 1.59 * mm});
            skCircle(sketch, "E36.0.4.126", {"center": v(-147.62, -36.51) * mm, "radius": 1.59 * mm});
            skCircle(sketch, "E36.0.4.127", {"center": v(-96.82, -36.51) * mm, "radius": 1.59 * mm});
            skCircle(sketch, "E36.0.4.128", {"center": v(-46.02, -36.51) * mm, "radius": 1.59 * mm});
            skCircle(sketch, "E36.0.4.129", {"center": v(4.78, -36.51) * mm, "radius": 1.59 * mm});
            skCircle(sketch, "E36.0.4.130", {"center": v(-249.22, -36.51) * mm, "radius": 1.59 * mm});
            skCircle(sketch, "E36.0.4.131", {"center": v(-198.42, -36.51) * mm, "radius": 1.59 * mm});
            skCircle(sketch, "E36.0.4.132", {"center": v(265.13, -36.51) * mm, "radius": 1.59 * mm});
            skCircle(sketch, "E36.0.4.133", {"center": v(61.93, -36.51) * mm, "radius": 1.59 * mm});
            skCircle(sketch, "E36.0.4.134", {"center": v(112.73, -36.51) * mm, "radius": 1.59 * mm});
            skCircle(sketch, "E36.0.4.135", {"center": v(163.53, -36.51) * mm, "radius": 1.59 * mm});
            skCircle(sketch, "E36.0.4.136", {"center": v(214.33, -36.51) * mm, "radius": 1.59 * mm});
            skCircle(sketch, "E36.0.4.137", {"center": v(-141.27, -36.51) * mm, "radius": 1.59 * mm});
            skCircle(sketch, "E36.0.4.138", {"center": v(-90.47, -36.51) * mm, "radius": 1.59 * mm});
            skCircle(sketch, "E36.0.4.139", {"center": v(-39.67, -36.51) * mm, "radius": 1.59 * mm});
            skCircle(sketch, "E36.0.4.140", {"center": v(11.13, -36.51) * mm, "radius": 1.59 * mm});
            skCircle(sketch, "E36.0.4.141", {"center": v(-242.87, -36.51) * mm, "radius": 1.59 * mm});
            skCircle(sketch, "E36.0.4.142", {"center": v(-192.07, -36.51) * mm, "radius": 1.59 * mm});
            skCircle(sketch, "E36.0.4.143", {"center": v(255.6, -39.69) * mm, "radius": 1.59 * mm});
            skCircle(sketch, "E36.0.4.144", {"center": v(52.4, -39.69) * mm, "radius": 1.59 * mm});
            skCircle(sketch, "E36.0.4.145", {"center": v(103.2, -39.69) * mm, "radius": 1.59 * mm});
            skCircle(sketch, "E36.0.4.146", {"center": v(154, -39.69) * mm, "radius": 1.59 * mm});
            skCircle(sketch, "E36.0.4.147", {"center": v(204.8, -39.69) * mm, "radius": 1.59 * mm});
            skCircle(sketch, "E36.0.4.148", {"center": v(-150.8, -39.69) * mm, "radius": 1.59 * mm});
            skCircle(sketch, "E36.0.4.149", {"center": v(-100, -39.69) * mm, "radius": 1.59 * mm});
            skCircle(sketch, "E36.0.4.150", {"center": v(-49.2, -39.69) * mm, "radius": 1.59 * mm});
            skCircle(sketch, "E36.0.4.151", {"center": v(1.6, -39.69) * mm, "radius": 1.59 * mm});
            skCircle(sketch, "E36.0.4.152", {"center": v(-252.4, -39.69) * mm, "radius": 1.59 * mm});
            skCircle(sketch, "E36.0.4.153", {"center": v(-201.6, -39.69) * mm, "radius": 1.59 * mm});
            skCircle(sketch, "E36.0.4.154", {"center": v(198.45, -39.69) * mm, "radius": 1.59 * mm});
            skCircle(sketch, "E36.0.4.155", {"center": v(147.65, -39.69) * mm, "radius": 1.59 * mm});
            skCircle(sketch, "E36.0.4.156", {"center": v(96.85, -39.69) * mm, "radius": 1.59 * mm});
            skCircle(sketch, "E36.0.4.157", {"center": v(46.05, -39.69) * mm, "radius": 1.59 * mm});
            skCircle(sketch, "E36.0.4.158", {"center": v(300.05, -39.69) * mm, "radius": 1.59 * mm});
            skCircle(sketch, "E36.0.4.159", {"center": v(249.25, -39.69) * mm, "radius": 1.59 * mm});
            skCircle(sketch, "E36.0.4.160", {"center": v(296.88, -36.51) * mm, "radius": 1.59 * mm});
            skCircle(sketch, "E36.0.4.161", {"center": v(42.88, -36.51) * mm, "radius": 1.59 * mm});
            skCircle(sketch, "E36.0.4.162", {"center": v(93.68, -36.51) * mm, "radius": 1.59 * mm});
            skCircle(sketch, "E36.0.4.163", {"center": v(-58.72, -36.51) * mm, "radius": 1.59 * mm});
            skCircle(sketch, "E36.0.4.164", {"center": v(-7.92, -36.51) * mm, "radius": 1.59 * mm});
            skCircle(sketch, "E36.0.4.165", {"center": v(-20.62, -36.51) * mm, "radius": 1.59 * mm});
            skCircle(sketch, "E36.0.4.166", {"center": v(30.18, -36.51) * mm, "radius": 1.59 * mm});
            skCircle(sketch, "E36.0.4.167", {"center": v(80.98, -36.51) * mm, "radius": 1.59 * mm});
            skCircle(sketch, "E36.0.4.168", {"center": v(-71.42, -36.51) * mm, "radius": 1.59 * mm});
            skCircle(sketch, "E36.0.4.169", {"center": v(293.7, -39.69) * mm, "radius": 1.59 * mm});
            skCircle(sketch, "E36.0.4.170", {"center": v(39.7, -39.69) * mm, "radius": 1.59 * mm});
            skCircle(sketch, "E36.0.4.171", {"center": v(90.5, -39.69) * mm, "radius": 1.59 * mm});
            skCircle(sketch, "E36.0.4.172", {"center": v(-61.9, -39.69) * mm, "radius": 1.59 * mm});
            skCircle(sketch, "E36.0.4.173", {"center": v(-11.1, -39.69) * mm, "radius": 1.59 * mm});
            skCircle(sketch, "E36.0.4.174", {"center": v(-14.27, -36.51) * mm, "radius": 1.59 * mm});
            skCircle(sketch, "E36.0.4.175", {"center": v(36.53, -36.51) * mm, "radius": 1.59 * mm});
            skCircle(sketch, "E36.0.4.176", {"center": v(87.33, -36.51) * mm, "radius": 1.59 * mm});
            skCircle(sketch, "E36.0.4.177", {"center": v(-65.07, -36.51) * mm, "radius": 1.59 * mm});
            skCircle(sketch, "E36.0.4.178", {"center": v(287.35, -39.69) * mm, "radius": 1.59 * mm});
            skCircle(sketch, "E36.0.4.179", {"center": v(33.35, -39.69) * mm, "radius": 1.59 * mm});
            skCircle(sketch, "E36.0.4.180", {"center": v(84.15, -39.69) * mm, "radius": 1.59 * mm});
            skCircle(sketch, "E36.0.4.181", {"center": v(290.53, -36.51) * mm, "radius": 1.59 * mm});
            skCircle(sketch, "E36.0.4.182", {"center": v(-68.25, -39.69) * mm, "radius": 1.59 * mm});
            skCircle(sketch, "E36.0.4.183", {"center": v(-17.45, -39.69) * mm, "radius": 1.59 * mm});
            skCircle(sketch, "E36.0.4.184", {"center": v(-284.15, -39.69) * mm, "radius": 1.59 * mm});
            skCircle(sketch, "E36.0.4.185", {"center": v(-280.97, -36.51) * mm, "radius": 1.59 * mm});
            skLineSegment(sketch, "E36.0.4.186", {"start": v(290.53, -36.51) * mm, "end": v(296.88, -36.51) * mm, "construction": true});
            skCircle(sketch, "E36.0.4.187", {"center": v(-287.32, -36.51) * mm, "radius": 1.59 * mm});
            skLineSegment(sketch, "E36.0.4.188", {"start": v(-296.85, -39.69) * mm, "end": v(-290.5, -39.69) * mm, "construction": true});
            skCircle(sketch, "E36.0.4.189", {"center": v(-290.5, -39.69) * mm, "radius": 1.59 * mm});
            skLineSegment(sketch, "E36.0.4.190", {"start": v(-296.85, -36.51) * mm, "end": v(-296.85, -39.69) * mm, "construction": true});
            skLineSegment(sketch, "E36.0.4.191", {"start": v(-300.02, -36.51) * mm, "end": v(-293.67, -36.51) * mm, "construction": true});
            skCircle(sketch, "E36.0.4.192", {"center": v(-293.67, -36.51) * mm, "radius": 1.59 * mm});
            skCircle(sketch, "E36.0.4.193", {"center": v(-296.85, -39.69) * mm, "radius": 1.59 * mm});
            skCircle(sketch, "E36.0.4.194", {"center": v(-300.02, -36.51) * mm, "radius": 1.59 * mm});
            skCircle(sketch, "E36.0.5.0", {"center": v(-227, -46.04) * mm, "radius": 1.59 * mm});
            skCircle(sketch, "E36.0.5.1", {"center": v(-176.2, -46.04) * mm, "radius": 1.59 * mm});
            skCircle(sketch, "E36.0.5.2", {"center": v(-125.4, -46.04) * mm, "radius": 1.59 * mm});
            skCircle(sketch, "E36.0.5.3", {"center": v(-230.17, -42.86) * mm, "radius": 1.59 * mm});
            skCircle(sketch, "E36.0.5.4", {"center": v(-179.37, -42.86) * mm, "radius": 1.59 * mm});
            skCircle(sketch, "E36.0.5.5", {"center": v(-128.57, -42.86) * mm, "radius": 1.59 * mm});
            skCircle(sketch, "E36.0.5.6", {"center": v(-157.15, -46.04) * mm, "radius": 1.59 * mm});
            skCircle(sketch, "E36.0.5.7", {"center": v(-106.35, -46.04) * mm, "radius": 1.59 * mm});
            skCircle(sketch, "E36.0.5.8", {"center": v(-55.55, -46.04) * mm, "radius": 1.59 * mm});
            skCircle(sketch, "E36.0.5.9", {"center": v(-4.75, -46.04) * mm, "radius": 1.59 * mm});
            skCircle(sketch, "E36.0.5.10", {"center": v(-207.95, -46.04) * mm, "radius": 1.59 * mm});
            skCircle(sketch, "E36.0.5.11", {"center": v(-258.75, -46.04) * mm, "radius": 1.59 * mm});
            skCircle(sketch, "E36.0.5.12", {"center": v(246.08, -42.86) * mm, "radius": 1.59 * mm});
            skCircle(sketch, "E36.0.5.13", {"center": v(144.48, -42.86) * mm, "radius": 1.59 * mm});
            skCircle(sketch, "E36.0.5.14", {"center": v(195.28, -42.86) * mm, "radius": 1.59 * mm});
            skCircle(sketch, "E36.0.5.15", {"center": v(-160.32, -42.86) * mm, "radius": 1.59 * mm});
            skCircle(sketch, "E36.0.5.16", {"center": v(-109.52, -42.86) * mm, "radius": 1.59 * mm});
            skCircle(sketch, "E36.0.5.17", {"center": v(-261.92, -42.86) * mm, "radius": 1.59 * mm});
            skCircle(sketch, "E36.0.5.18", {"center": v(-211.12, -42.86) * mm, "radius": 1.59 * mm});
            skCircle(sketch, "E36.0.5.19", {"center": v(252.43, -42.86) * mm, "radius": 1.59 * mm});
            skLineSegment(sketch, "E36.0.5.20", {"start": v(-293.67, -42.86) * mm, "end": v(-280.97, -42.86) * mm, "construction": true});
            skCircle(sketch, "E36.0.5.21", {"center": v(49.23, -42.86) * mm, "radius": 1.59 * mm});
            skCircle(sketch, "E36.0.5.22", {"center": v(100.03, -42.86) * mm, "radius": 1.59 * mm});
            skCircle(sketch, "E36.0.5.23", {"center": v(150.83, -42.86) * mm, "radius": 1.59 * mm});
            skCircle(sketch, "E36.0.5.24", {"center": v(201.63, -42.86) * mm, "radius": 1.59 * mm});
            skCircle(sketch, "E36.0.5.25", {"center": v(-153.97, -42.86) * mm, "radius": 1.59 * mm});
            skCircle(sketch, "E36.0.5.26", {"center": v(-103.17, -42.86) * mm, "radius": 1.59 * mm});
            skCircle(sketch, "E36.0.5.27", {"center": v(-52.37, -42.86) * mm, "radius": 1.59 * mm});
            skCircle(sketch, "E36.0.5.28", {"center": v(-1.57, -42.86) * mm, "radius": 1.59 * mm});
            skCircle(sketch, "E36.0.5.29", {"center": v(-204.77, -42.86) * mm, "radius": 1.59 * mm});
            skCircle(sketch, "E36.0.5.30", {"center": v(182.58, -42.86) * mm, "radius": 1.59 * mm});
            skCircle(sketch, "E36.0.5.31", {"center": v(233.38, -42.86) * mm, "radius": 1.59 * mm});
            skCircle(sketch, "E36.0.5.32", {"center": v(284.18, -42.86) * mm, "radius": 1.59 * mm});
            skCircle(sketch, "E36.0.5.33", {"center": v(131.78, -42.86) * mm, "radius": 1.59 * mm});
            skCircle(sketch, "E36.0.5.34", {"center": v(-223.82, -42.86) * mm, "radius": 1.59 * mm});
            skCircle(sketch, "E36.0.5.35", {"center": v(-173.02, -42.86) * mm, "radius": 1.59 * mm});
            skCircle(sketch, "E36.0.5.36", {"center": v(-122.22, -42.86) * mm, "radius": 1.59 * mm});
            skCircle(sketch, "E36.0.5.37", {"center": v(242.9, -46.04) * mm, "radius": 1.59 * mm});
            skCircle(sketch, "E36.0.5.38", {"center": v(141.3, -46.04) * mm, "radius": 1.59 * mm});
            skCircle(sketch, "E36.0.5.39", {"center": v(192.1, -46.04) * mm, "radius": 1.59 * mm});
            skCircle(sketch, "E36.0.5.40", {"center": v(-163.5, -46.04) * mm, "radius": 1.59 * mm});
            skCircle(sketch, "E36.0.5.41", {"center": v(-112.7, -46.04) * mm, "radius": 1.59 * mm});
            skCircle(sketch, "E36.0.5.42", {"center": v(-214.3, -46.04) * mm, "radius": 1.59 * mm});
            skCircle(sketch, "E36.0.5.43", {"center": v(138.13, -42.86) * mm, "radius": 1.59 * mm});
            skCircle(sketch, "E36.0.5.44", {"center": v(-217.47, -42.86) * mm, "radius": 1.59 * mm});
            skCircle(sketch, "E36.0.5.45", {"center": v(-166.67, -42.86) * mm, "radius": 1.59 * mm});
            skCircle(sketch, "E36.0.5.46", {"center": v(-115.87, -42.86) * mm, "radius": 1.59 * mm});
            skCircle(sketch, "E36.0.5.47", {"center": v(236.55, -46.04) * mm, "radius": 1.59 * mm});
            skCircle(sketch, "E36.0.5.48", {"center": v(134.95, -46.04) * mm, "radius": 1.59 * mm});
            skCircle(sketch, "E36.0.5.49", {"center": v(185.75, -46.04) * mm, "radius": 1.59 * mm});
            skCircle(sketch, "E36.0.5.50", {"center": v(188.93, -42.86) * mm, "radius": 1.59 * mm});
            skCircle(sketch, "E36.0.5.51", {"center": v(239.73, -42.86) * mm, "radius": 1.59 * mm});
            skCircle(sketch, "E36.0.5.52", {"center": v(-169.85, -46.04) * mm, "radius": 1.59 * mm});
            skCircle(sketch, "E36.0.5.53", {"center": v(-119.05, -46.04) * mm, "radius": 1.59 * mm});
            skCircle(sketch, "E36.0.5.54", {"center": v(-220.65, -46.04) * mm, "radius": 1.59 * mm});
            skCircle(sketch, "E36.0.5.55", {"center": v(-74.6, -46.04) * mm, "radius": 1.59 * mm});
            skCircle(sketch, "E36.0.5.56", {"center": v(179.4, -46.04) * mm, "radius": 1.59 * mm});
            skCircle(sketch, "E36.0.5.57", {"center": v(230.2, -46.04) * mm, "radius": 1.59 * mm});
            skCircle(sketch, "E36.0.5.58", {"center": v(281, -46.04) * mm, "radius": 1.59 * mm});
            skCircle(sketch, "E36.0.5.59", {"center": v(-23.8, -46.04) * mm, "radius": 1.59 * mm});
            skCircle(sketch, "E36.0.5.60", {"center": v(27, -46.04) * mm, "radius": 1.59 * mm});
            skCircle(sketch, "E36.0.5.61", {"center": v(77.8, -46.04) * mm, "radius": 1.59 * mm});
            skCircle(sketch, "E36.0.5.62", {"center": v(128.6, -46.04) * mm, "radius": 1.59 * mm});
            skCircle(sketch, "E36.0.5.63", {"center": v(-274.62, -42.86) * mm, "radius": 1.59 * mm});
            skCircle(sketch, "E36.0.5.64", {"center": v(-268.27, -42.86) * mm, "radius": 1.59 * mm});
            skCircle(sketch, "E36.0.5.65", {"center": v(-277.8, -46.04) * mm, "radius": 1.59 * mm});
            skCircle(sketch, "E36.0.5.66", {"center": v(173.05, -46.04) * mm, "radius": 1.59 * mm});
            skCircle(sketch, "E36.0.5.67", {"center": v(223.85, -46.04) * mm, "radius": 1.59 * mm});
            skCircle(sketch, "E36.0.5.68", {"center": v(274.65, -46.04) * mm, "radius": 1.59 * mm});
            skCircle(sketch, "E36.0.5.69", {"center": v(-30.15, -46.04) * mm, "radius": 1.59 * mm});
            skCircle(sketch, "E36.0.5.70", {"center": v(20.65, -46.04) * mm, "radius": 1.59 * mm});
            skCircle(sketch, "E36.0.5.71", {"center": v(71.45, -46.04) * mm, "radius": 1.59 * mm});
            skCircle(sketch, "E36.0.5.72", {"center": v(122.25, -46.04) * mm, "radius": 1.59 * mm});
            skCircle(sketch, "E36.0.5.73", {"center": v(-233.35, -46.04) * mm, "radius": 1.59 * mm});
            skCircle(sketch, "E36.0.5.74", {"center": v(-182.55, -46.04) * mm, "radius": 1.59 * mm});
            skCircle(sketch, "E36.0.5.75", {"center": v(-131.75, -46.04) * mm, "radius": 1.59 * mm});
            skCircle(sketch, "E36.0.5.76", {"center": v(-80.95, -46.04) * mm, "radius": 1.59 * mm});
            skCircle(sketch, "E36.0.5.77", {"center": v(-255.57, -42.86) * mm, "radius": 1.59 * mm});
            skCircle(sketch, "E36.0.5.78", {"center": v(-265.1, -46.04) * mm, "radius": 1.59 * mm});
            skCircle(sketch, "E36.0.5.79", {"center": v(-271.45, -46.04) * mm, "radius": 1.59 * mm});
            skCircle(sketch, "E36.0.5.80", {"center": v(169.88, -42.86) * mm, "radius": 1.59 * mm});
            skCircle(sketch, "E36.0.5.81", {"center": v(220.68, -42.86) * mm, "radius": 1.59 * mm});
            skCircle(sketch, "E36.0.5.82", {"center": v(271.48, -42.86) * mm, "radius": 1.59 * mm});
            skCircle(sketch, "E36.0.5.83", {"center": v(-33.32, -42.86) * mm, "radius": 1.59 * mm});
            skCircle(sketch, "E36.0.5.84", {"center": v(17.48, -42.86) * mm, "radius": 1.59 * mm});
            skCircle(sketch, "E36.0.5.85", {"center": v(68.28, -42.86) * mm, "radius": 1.59 * mm});
            skCircle(sketch, "E36.0.5.86", {"center": v(-236.52, -42.86) * mm, "radius": 1.59 * mm});
            skCircle(sketch, "E36.0.5.87", {"center": v(119.08, -42.86) * mm, "radius": 1.59 * mm});
            skCircle(sketch, "E36.0.5.88", {"center": v(-185.72, -42.86) * mm, "radius": 1.59 * mm});
            skCircle(sketch, "E36.0.5.89", {"center": v(-134.92, -42.86) * mm, "radius": 1.59 * mm});
            skCircle(sketch, "E36.0.5.90", {"center": v(-84.12, -42.86) * mm, "radius": 1.59 * mm});
            skCircle(sketch, "E36.0.5.91", {"center": v(176.23, -42.86) * mm, "radius": 1.59 * mm});
            skCircle(sketch, "E36.0.5.92", {"center": v(227.03, -42.86) * mm, "radius": 1.59 * mm});
            skCircle(sketch, "E36.0.5.93", {"center": v(277.83, -42.86) * mm, "radius": 1.59 * mm});
            skCircle(sketch, "E36.0.5.94", {"center": v(-26.97, -42.86) * mm, "radius": 1.59 * mm});
            skCircle(sketch, "E36.0.5.95", {"center": v(23.83, -42.86) * mm, "radius": 1.59 * mm});
            skCircle(sketch, "E36.0.5.96", {"center": v(74.63, -42.86) * mm, "radius": 1.59 * mm});
            skCircle(sketch, "E36.0.5.97", {"center": v(125.43, -42.86) * mm, "radius": 1.59 * mm});
            skCircle(sketch, "E36.0.5.98", {"center": v(-77.77, -42.86) * mm, "radius": 1.59 * mm});
            skCircle(sketch, "E36.0.5.99", {"center": v(268.3, -46.04) * mm, "radius": 1.59 * mm});
            skCircle(sketch, "E36.0.5.100", {"center": v(65.1, -46.04) * mm, "radius": 1.59 * mm});
            skCircle(sketch, "E36.0.5.101", {"center": v(115.9, -46.04) * mm, "radius": 1.59 * mm});
            skCircle(sketch, "E36.0.5.102", {"center": v(166.7, -46.04) * mm, "radius": 1.59 * mm});
            skCircle(sketch, "E36.0.5.103", {"center": v(217.5, -46.04) * mm, "radius": 1.59 * mm});
            skCircle(sketch, "E36.0.5.104", {"center": v(-138.1, -46.04) * mm, "radius": 1.59 * mm});
            skCircle(sketch, "E36.0.5.105", {"center": v(-87.3, -46.04) * mm, "radius": 1.59 * mm});
            skCircle(sketch, "E36.0.5.106", {"center": v(-36.5, -46.04) * mm, "radius": 1.59 * mm});
            skCircle(sketch, "E36.0.5.107", {"center": v(14.3, -46.04) * mm, "radius": 1.59 * mm});
            skCircle(sketch, "E36.0.5.108", {"center": v(-239.7, -46.04) * mm, "radius": 1.59 * mm});
            skCircle(sketch, "E36.0.5.109", {"center": v(-188.9, -46.04) * mm, "radius": 1.59 * mm});
            skCircle(sketch, "E36.0.5.110", {"center": v(261.95, -46.04) * mm, "radius": 1.59 * mm});
            skCircle(sketch, "E36.0.5.111", {"center": v(58.75, -46.04) * mm, "radius": 1.59 * mm});
            skCircle(sketch, "E36.0.5.112", {"center": v(109.55, -46.04) * mm, "radius": 1.59 * mm});
            skCircle(sketch, "E36.0.5.113", {"center": v(160.35, -46.04) * mm, "radius": 1.59 * mm});
            skCircle(sketch, "E36.0.5.114", {"center": v(211.15, -46.04) * mm, "radius": 1.59 * mm});
            skCircle(sketch, "E36.0.5.115", {"center": v(-144.45, -46.04) * mm, "radius": 1.59 * mm});
            skCircle(sketch, "E36.0.5.116", {"center": v(-93.65, -46.04) * mm, "radius": 1.59 * mm});
            skCircle(sketch, "E36.0.5.117", {"center": v(-42.85, -46.04) * mm, "radius": 1.59 * mm});
            skCircle(sketch, "E36.0.5.118", {"center": v(7.95, -46.04) * mm, "radius": 1.59 * mm});
            skCircle(sketch, "E36.0.5.119", {"center": v(-246.05, -46.04) * mm, "radius": 1.59 * mm});
            skCircle(sketch, "E36.0.5.120", {"center": v(-195.25, -46.04) * mm, "radius": 1.59 * mm});
            skCircle(sketch, "E36.0.5.121", {"center": v(258.78, -42.86) * mm, "radius": 1.59 * mm});
            skCircle(sketch, "E36.0.5.122", {"center": v(55.58, -42.86) * mm, "radius": 1.59 * mm});
            skCircle(sketch, "E36.0.5.123", {"center": v(106.38, -42.86) * mm, "radius": 1.59 * mm});
            skCircle(sketch, "E36.0.5.124", {"center": v(157.18, -42.86) * mm, "radius": 1.59 * mm});
            skCircle(sketch, "E36.0.5.125", {"center": v(207.98, -42.86) * mm, "radius": 1.59 * mm});
            skCircle(sketch, "E36.0.5.126", {"center": v(-147.62, -42.86) * mm, "radius": 1.59 * mm});
            skCircle(sketch, "E36.0.5.127", {"center": v(-96.82, -42.86) * mm, "radius": 1.59 * mm});
            skCircle(sketch, "E36.0.5.128", {"center": v(-46.02, -42.86) * mm, "radius": 1.59 * mm});
            skCircle(sketch, "E36.0.5.129", {"center": v(4.78, -42.86) * mm, "radius": 1.59 * mm});
            skCircle(sketch, "E36.0.5.130", {"center": v(-249.22, -42.86) * mm, "radius": 1.59 * mm});
            skCircle(sketch, "E36.0.5.131", {"center": v(-198.42, -42.86) * mm, "radius": 1.59 * mm});
            skCircle(sketch, "E36.0.5.132", {"center": v(265.13, -42.86) * mm, "radius": 1.59 * mm});
            skCircle(sketch, "E36.0.5.133", {"center": v(61.93, -42.86) * mm, "radius": 1.59 * mm});
            skCircle(sketch, "E36.0.5.134", {"center": v(112.73, -42.86) * mm, "radius": 1.59 * mm});
            skCircle(sketch, "E36.0.5.135", {"center": v(163.53, -42.86) * mm, "radius": 1.59 * mm});
            skCircle(sketch, "E36.0.5.136", {"center": v(214.33, -42.86) * mm, "radius": 1.59 * mm});
            skCircle(sketch, "E36.0.5.137", {"center": v(-141.27, -42.86) * mm, "radius": 1.59 * mm});
            skCircle(sketch, "E36.0.5.138", {"center": v(-90.47, -42.86) * mm, "radius": 1.59 * mm});
            skCircle(sketch, "E36.0.5.139", {"center": v(-39.67, -42.86) * mm, "radius": 1.59 * mm});
            skCircle(sketch, "E36.0.5.140", {"center": v(11.13, -42.86) * mm, "radius": 1.59 * mm});
            skCircle(sketch, "E36.0.5.141", {"center": v(-242.87, -42.86) * mm, "radius": 1.59 * mm});
            skCircle(sketch, "E36.0.5.142", {"center": v(-192.07, -42.86) * mm, "radius": 1.59 * mm});
            skCircle(sketch, "E36.0.5.143", {"center": v(255.6, -46.04) * mm, "radius": 1.59 * mm});
            skCircle(sketch, "E36.0.5.144", {"center": v(52.4, -46.04) * mm, "radius": 1.59 * mm});
            skCircle(sketch, "E36.0.5.145", {"center": v(103.2, -46.04) * mm, "radius": 1.59 * mm});
            skCircle(sketch, "E36.0.5.146", {"center": v(154, -46.04) * mm, "radius": 1.59 * mm});
            skCircle(sketch, "E36.0.5.147", {"center": v(204.8, -46.04) * mm, "radius": 1.59 * mm});
            skCircle(sketch, "E36.0.5.148", {"center": v(-150.8, -46.04) * mm, "radius": 1.59 * mm});
            skCircle(sketch, "E36.0.5.149", {"center": v(-100, -46.04) * mm, "radius": 1.59 * mm});
            skCircle(sketch, "E36.0.5.150", {"center": v(-49.2, -46.04) * mm, "radius": 1.59 * mm});
            skCircle(sketch, "E36.0.5.151", {"center": v(1.6, -46.04) * mm, "radius": 1.59 * mm});
            skCircle(sketch, "E36.0.5.152", {"center": v(-252.4, -46.04) * mm, "radius": 1.59 * mm});
            skCircle(sketch, "E36.0.5.153", {"center": v(-201.6, -46.04) * mm, "radius": 1.59 * mm});
            skCircle(sketch, "E36.0.5.154", {"center": v(198.45, -46.04) * mm, "radius": 1.59 * mm});
            skCircle(sketch, "E36.0.5.155", {"center": v(147.65, -46.04) * mm, "radius": 1.59 * mm});
            skCircle(sketch, "E36.0.5.156", {"center": v(96.85, -46.04) * mm, "radius": 1.59 * mm});
            skCircle(sketch, "E36.0.5.157", {"center": v(46.05, -46.04) * mm, "radius": 1.59 * mm});
            skCircle(sketch, "E36.0.5.158", {"center": v(300.05, -46.04) * mm, "radius": 1.59 * mm});
            skCircle(sketch, "E36.0.5.159", {"center": v(249.25, -46.04) * mm, "radius": 1.59 * mm});
            skCircle(sketch, "E36.0.5.160", {"center": v(296.88, -42.86) * mm, "radius": 1.59 * mm});
            skCircle(sketch, "E36.0.5.161", {"center": v(42.88, -42.86) * mm, "radius": 1.59 * mm});
            skCircle(sketch, "E36.0.5.162", {"center": v(93.68, -42.86) * mm, "radius": 1.59 * mm});
            skCircle(sketch, "E36.0.5.163", {"center": v(-58.72, -42.86) * mm, "radius": 1.59 * mm});
            skCircle(sketch, "E36.0.5.164", {"center": v(-7.92, -42.86) * mm, "radius": 1.59 * mm});
            skCircle(sketch, "E36.0.5.165", {"center": v(-20.62, -42.86) * mm, "radius": 1.59 * mm});
            skCircle(sketch, "E36.0.5.166", {"center": v(30.18, -42.86) * mm, "radius": 1.59 * mm});
            skCircle(sketch, "E36.0.5.167", {"center": v(80.98, -42.86) * mm, "radius": 1.59 * mm});
            skCircle(sketch, "E36.0.5.168", {"center": v(-71.42, -42.86) * mm, "radius": 1.59 * mm});
            skCircle(sketch, "E36.0.5.169", {"center": v(293.7, -46.04) * mm, "radius": 1.59 * mm});
            skCircle(sketch, "E36.0.5.170", {"center": v(39.7, -46.04) * mm, "radius": 1.59 * mm});
            skCircle(sketch, "E36.0.5.171", {"center": v(90.5, -46.04) * mm, "radius": 1.59 * mm});
            skCircle(sketch, "E36.0.5.172", {"center": v(-61.9, -46.04) * mm, "radius": 1.59 * mm});
            skCircle(sketch, "E36.0.5.173", {"center": v(-11.1, -46.04) * mm, "radius": 1.59 * mm});
            skCircle(sketch, "E36.0.5.174", {"center": v(-14.27, -42.86) * mm, "radius": 1.59 * mm});
            skCircle(sketch, "E36.0.5.175", {"center": v(36.53, -42.86) * mm, "radius": 1.59 * mm});
            skCircle(sketch, "E36.0.5.176", {"center": v(87.33, -42.86) * mm, "radius": 1.59 * mm});
            skCircle(sketch, "E36.0.5.177", {"center": v(-65.07, -42.86) * mm, "radius": 1.59 * mm});
            skCircle(sketch, "E36.0.5.178", {"center": v(287.35, -46.04) * mm, "radius": 1.59 * mm});
            skCircle(sketch, "E36.0.5.179", {"center": v(33.35, -46.04) * mm, "radius": 1.59 * mm});
            skCircle(sketch, "E36.0.5.180", {"center": v(84.15, -46.04) * mm, "radius": 1.59 * mm});
            skCircle(sketch, "E36.0.5.181", {"center": v(290.53, -42.86) * mm, "radius": 1.59 * mm});
            skCircle(sketch, "E36.0.5.182", {"center": v(-68.25, -46.04) * mm, "radius": 1.59 * mm});
            skCircle(sketch, "E36.0.5.183", {"center": v(-17.45, -46.04) * mm, "radius": 1.59 * mm});
            skCircle(sketch, "E36.0.5.184", {"center": v(-284.15, -46.04) * mm, "radius": 1.59 * mm});
            skCircle(sketch, "E36.0.5.185", {"center": v(-280.97, -42.86) * mm, "radius": 1.59 * mm});
            skLineSegment(sketch, "E36.0.5.186", {"start": v(290.53, -42.86) * mm, "end": v(296.88, -42.86) * mm, "construction": true});
            skCircle(sketch, "E36.0.5.187", {"center": v(-287.32, -42.86) * mm, "radius": 1.59 * mm});
            skLineSegment(sketch, "E36.0.5.188", {"start": v(-296.85, -46.04) * mm, "end": v(-290.5, -46.04) * mm, "construction": true});
            skCircle(sketch, "E36.0.5.189", {"center": v(-290.5, -46.04) * mm, "radius": 1.59 * mm});
            skLineSegment(sketch, "E36.0.5.190", {"start": v(-296.85, -42.86) * mm, "end": v(-296.85, -46.04) * mm, "construction": true});
            skLineSegment(sketch, "E36.0.5.191", {"start": v(-300.02, -42.86) * mm, "end": v(-293.67, -42.86) * mm, "construction": true});
            skCircle(sketch, "E36.0.5.192", {"center": v(-293.67, -42.86) * mm, "radius": 1.59 * mm});
            skCircle(sketch, "E36.0.5.193", {"center": v(-296.85, -46.04) * mm, "radius": 1.59 * mm});
            skCircle(sketch, "E36.0.5.194", {"center": v(-300.02, -42.86) * mm, "radius": 1.59 * mm});
            skLineSegment(sketch, "E36.direction1", {"start": v(-296.85, -14.29) * mm, "end": v(-271.45, -14.29) * mm, "construction": true});
            skLineSegment(sketch, "E36.direction2", {"start": v(-296.85, -14.29) * mm, "end": v(-296.85, -20.64) * mm, "construction": true});
            skCircle(sketch, "E37.0.0.6", {"center": v(-227, -52.39) * mm, "radius": 1.59 * mm});
            skCircle(sketch, "E37.2.0.6", {"center": v(-176.2, -52.39) * mm, "radius": 1.59 * mm});
            skCircle(sketch, "E37.4.0.6", {"center": v(-125.4, -52.39) * mm, "radius": 1.59 * mm});
            skCircle(sketch, "E37.6.0.6", {"center": v(-230.17, -49.21) * mm, "radius": 1.59 * mm});
            skCircle(sketch, "E37.8.0.6", {"center": v(-179.37, -49.21) * mm, "radius": 1.59 * mm});
            skCircle(sketch, "E37.10.0.6", {"center": v(-128.57, -49.21) * mm, "radius": 1.59 * mm});
            skCircle(sketch, "E37.12.0.6", {"center": v(-157.15, -52.39) * mm, "radius": 1.59 * mm});
            skCircle(sketch, "E37.14.0.6", {"center": v(-106.35, -52.39) * mm, "radius": 1.59 * mm});
            skCircle(sketch, "E37.16.0.6", {"center": v(-55.55, -52.39) * mm, "radius": 1.59 * mm});
            skCircle(sketch, "E37.18.0.6", {"center": v(-4.75, -52.39) * mm, "radius": 1.59 * mm});
            skCircle(sketch, "E37.20.0.6", {"center": v(-207.95, -52.39) * mm, "radius": 1.59 * mm});
            skCircle(sketch, "E37.22.0.6", {"center": v(-258.75, -52.39) * mm, "radius": 1.59 * mm});
            skCircle(sketch, "E37.24.0.6", {"center": v(246.08, -49.21) * mm, "radius": 1.59 * mm});
            skCircle(sketch, "E37.26.0.6", {"center": v(144.48, -49.21) * mm, "radius": 1.59 * mm});
            skCircle(sketch, "E37.28.0.6", {"center": v(195.28, -49.21) * mm, "radius": 1.59 * mm});
            skCircle(sketch, "E37.30.0.6", {"center": v(-160.32, -49.21) * mm, "radius": 1.59 * mm});
            skCircle(sketch, "E37.32.0.6", {"center": v(-109.52, -49.21) * mm, "radius": 1.59 * mm});
            skCircle(sketch, "E37.34.0.6", {"center": v(-261.92, -49.21) * mm, "radius": 1.59 * mm});
            skCircle(sketch, "E37.36.0.6", {"center": v(-211.12, -49.21) * mm, "radius": 1.59 * mm});
            skCircle(sketch, "E37.38.0.6", {"center": v(252.43, -49.21) * mm, "radius": 1.59 * mm});
            skLineSegment(sketch, "E37.40.0.6", {"start": v(-293.67, -49.21) * mm, "end": v(-280.97, -49.21) * mm, "construction": true});
            skCircle(sketch, "E37.43.0.6", {"center": v(49.23, -49.21) * mm, "radius": 1.59 * mm});
            skCircle(sketch, "E37.45.0.6", {"center": v(100.03, -49.21) * mm, "radius": 1.59 * mm});
            skCircle(sketch, "E37.47.0.6", {"center": v(150.83, -49.21) * mm, "radius": 1.59 * mm});
            skCircle(sketch, "E37.49.0.6", {"center": v(201.63, -49.21) * mm, "radius": 1.59 * mm});
            skCircle(sketch, "E37.51.0.6", {"center": v(-153.97, -49.21) * mm, "radius": 1.59 * mm});
            skCircle(sketch, "E37.53.0.6", {"center": v(-103.17, -49.21) * mm, "radius": 1.59 * mm});
            skCircle(sketch, "E37.55.0.6", {"center": v(-52.37, -49.21) * mm, "radius": 1.59 * mm});
            skCircle(sketch, "E37.57.0.6", {"center": v(-1.57, -49.21) * mm, "radius": 1.59 * mm});
            skCircle(sketch, "E37.59.0.6", {"center": v(-204.77, -49.21) * mm, "radius": 1.59 * mm});
            skCircle(sketch, "E37.61.0.6", {"center": v(182.58, -49.21) * mm, "radius": 1.59 * mm});
            skCircle(sketch, "E37.63.0.6", {"center": v(233.38, -49.21) * mm, "radius": 1.59 * mm});
            skCircle(sketch, "E37.65.0.6", {"center": v(284.18, -49.21) * mm, "radius": 1.59 * mm});
            skCircle(sketch, "E37.67.0.6", {"center": v(131.78, -49.21) * mm, "radius": 1.59 * mm});
            skCircle(sketch, "E37.69.0.6", {"center": v(-223.82, -49.21) * mm, "radius": 1.59 * mm});
            skCircle(sketch, "E37.71.0.6", {"center": v(-173.02, -49.21) * mm, "radius": 1.59 * mm});
            skCircle(sketch, "E37.73.0.6", {"center": v(-122.22, -49.21) * mm, "radius": 1.59 * mm});
            skCircle(sketch, "E37.75.0.6", {"center": v(242.9, -52.39) * mm, "radius": 1.59 * mm});
            skCircle(sketch, "E37.77.0.6", {"center": v(141.3, -52.39) * mm, "radius": 1.59 * mm});
            skCircle(sketch, "E37.79.0.6", {"center": v(192.1, -52.39) * mm, "radius": 1.59 * mm});
            skCircle(sketch, "E37.81.0.6", {"center": v(-163.5, -52.39) * mm, "radius": 1.59 * mm});
            skCircle(sketch, "E37.83.0.6", {"center": v(-112.7, -52.39) * mm, "radius": 1.59 * mm});
            skCircle(sketch, "E37.85.0.6", {"center": v(-214.3, -52.39) * mm, "radius": 1.59 * mm});
            skCircle(sketch, "E37.87.0.6", {"center": v(138.13, -49.21) * mm, "radius": 1.59 * mm});
            skCircle(sketch, "E37.89.0.6", {"center": v(-217.47, -49.21) * mm, "radius": 1.59 * mm});
            skCircle(sketch, "E37.91.0.6", {"center": v(-166.67, -49.21) * mm, "radius": 1.59 * mm});
            skCircle(sketch, "E37.93.0.6", {"center": v(-115.87, -49.21) * mm, "radius": 1.59 * mm});
            skCircle(sketch, "E37.95.0.6", {"center": v(236.55, -52.39) * mm, "radius": 1.59 * mm});
            skCircle(sketch, "E37.97.0.6", {"center": v(134.95, -52.39) * mm, "radius": 1.59 * mm});
            skCircle(sketch, "E37.99.0.6", {"center": v(185.75, -52.39) * mm, "radius": 1.59 * mm});
            skCircle(sketch, "E37.101.0.6", {"center": v(188.93, -49.21) * mm, "radius": 1.59 * mm});
            skCircle(sketch, "E37.103.0.6", {"center": v(239.73, -49.21) * mm, "radius": 1.59 * mm});
            skCircle(sketch, "E37.105.0.6", {"center": v(-169.85, -52.39) * mm, "radius": 1.59 * mm});
            skCircle(sketch, "E37.107.0.6", {"center": v(-119.05, -52.39) * mm, "radius": 1.59 * mm});
            skCircle(sketch, "E37.109.0.6", {"center": v(-220.65, -52.39) * mm, "radius": 1.59 * mm});
            skCircle(sketch, "E37.111.0.6", {"center": v(-74.6, -52.39) * mm, "radius": 1.59 * mm});
            skCircle(sketch, "E37.113.0.6", {"center": v(179.4, -52.39) * mm, "radius": 1.59 * mm});
            skCircle(sketch, "E37.115.0.6", {"center": v(230.2, -52.39) * mm, "radius": 1.59 * mm});
            skCircle(sketch, "E37.117.0.6", {"center": v(281, -52.39) * mm, "radius": 1.59 * mm});
            skCircle(sketch, "E37.119.0.6", {"center": v(-23.8, -52.39) * mm, "radius": 1.59 * mm});
            skCircle(sketch, "E37.121.0.6", {"center": v(27, -52.39) * mm, "radius": 1.59 * mm});
            skCircle(sketch, "E37.123.0.6", {"center": v(77.8, -52.39) * mm, "radius": 1.59 * mm});
            skCircle(sketch, "E37.125.0.6", {"center": v(128.6, -52.39) * mm, "radius": 1.59 * mm});
            skCircle(sketch, "E37.127.0.6", {"center": v(-274.62, -49.21) * mm, "radius": 1.59 * mm});
            skCircle(sketch, "E37.129.0.6", {"center": v(-268.27, -49.21) * mm, "radius": 1.59 * mm});
            skCircle(sketch, "E37.131.0.6", {"center": v(-277.8, -52.39) * mm, "radius": 1.59 * mm});
            skCircle(sketch, "E37.133.0.6", {"center": v(173.05, -52.39) * mm, "radius": 1.59 * mm});
            skCircle(sketch, "E37.135.0.6", {"center": v(223.85, -52.39) * mm, "radius": 1.59 * mm});
            skCircle(sketch, "E37.137.0.6", {"center": v(274.65, -52.39) * mm, "radius": 1.59 * mm});
            skCircle(sketch, "E37.139.0.6", {"center": v(-30.15, -52.39) * mm, "radius": 1.59 * mm});
            skCircle(sketch, "E37.141.0.6", {"center": v(20.65, -52.39) * mm, "radius": 1.59 * mm});
            skCircle(sketch, "E37.143.0.6", {"center": v(71.45, -52.39) * mm, "radius": 1.59 * mm});
            skCircle(sketch, "E37.145.0.6", {"center": v(122.25, -52.39) * mm, "radius": 1.59 * mm});
            skCircle(sketch, "E37.147.0.6", {"center": v(-233.35, -52.39) * mm, "radius": 1.59 * mm});
            skCircle(sketch, "E37.149.0.6", {"center": v(-182.55, -52.39) * mm, "radius": 1.59 * mm});
            skCircle(sketch, "E37.151.0.6", {"center": v(-131.75, -52.39) * mm, "radius": 1.59 * mm});
            skCircle(sketch, "E37.153.0.6", {"center": v(-80.95, -52.39) * mm, "radius": 1.59 * mm});
            skCircle(sketch, "E37.155.0.6", {"center": v(-255.57, -49.21) * mm, "radius": 1.59 * mm});
            skCircle(sketch, "E37.157.0.6", {"center": v(-265.1, -52.39) * mm, "radius": 1.59 * mm});
            skCircle(sketch, "E37.159.0.6", {"center": v(-271.45, -52.39) * mm, "radius": 1.59 * mm});
            skCircle(sketch, "E37.161.0.6", {"center": v(169.88, -49.21) * mm, "radius": 1.59 * mm});
            skCircle(sketch, "E37.163.0.6", {"center": v(220.68, -49.21) * mm, "radius": 1.59 * mm});
            skCircle(sketch, "E37.165.0.6", {"center": v(271.48, -49.21) * mm, "radius": 1.59 * mm});
            skCircle(sketch, "E37.167.0.6", {"center": v(-33.32, -49.21) * mm, "radius": 1.59 * mm});
            skCircle(sketch, "E37.169.0.6", {"center": v(17.48, -49.21) * mm, "radius": 1.59 * mm});
            skCircle(sketch, "E37.171.0.6", {"center": v(68.28, -49.21) * mm, "radius": 1.59 * mm});
            skCircle(sketch, "E37.173.0.6", {"center": v(-236.52, -49.21) * mm, "radius": 1.59 * mm});
            skCircle(sketch, "E37.175.0.6", {"center": v(119.08, -49.21) * mm, "radius": 1.59 * mm});
            skCircle(sketch, "E37.177.0.6", {"center": v(-185.72, -49.21) * mm, "radius": 1.59 * mm});
            skCircle(sketch, "E37.179.0.6", {"center": v(-134.92, -49.21) * mm, "radius": 1.59 * mm});
            skCircle(sketch, "E37.181.0.6", {"center": v(-84.12, -49.21) * mm, "radius": 1.59 * mm});
            skCircle(sketch, "E37.183.0.6", {"center": v(176.23, -49.21) * mm, "radius": 1.59 * mm});
            skCircle(sketch, "E37.185.0.6", {"center": v(227.03, -49.21) * mm, "radius": 1.59 * mm});
            skCircle(sketch, "E37.187.0.6", {"center": v(277.83, -49.21) * mm, "radius": 1.59 * mm});
            skCircle(sketch, "E37.189.0.6", {"center": v(-26.97, -49.21) * mm, "radius": 1.59 * mm});
            skCircle(sketch, "E37.191.0.6", {"center": v(23.83, -49.21) * mm, "radius": 1.59 * mm});
            skCircle(sketch, "E37.193.0.6", {"center": v(74.63, -49.21) * mm, "radius": 1.59 * mm});
            skCircle(sketch, "E37.195.0.6", {"center": v(125.43, -49.21) * mm, "radius": 1.59 * mm});
            skCircle(sketch, "E37.197.0.6", {"center": v(-77.77, -49.21) * mm, "radius": 1.59 * mm});
            skCircle(sketch, "E37.199.0.6", {"center": v(268.3, -52.39) * mm, "radius": 1.59 * mm});
            skCircle(sketch, "E37.201.0.6", {"center": v(65.1, -52.39) * mm, "radius": 1.59 * mm});
            skCircle(sketch, "E37.203.0.6", {"center": v(115.9, -52.39) * mm, "radius": 1.59 * mm});
            skCircle(sketch, "E37.205.0.6", {"center": v(166.7, -52.39) * mm, "radius": 1.59 * mm});
            skCircle(sketch, "E37.207.0.6", {"center": v(217.5, -52.39) * mm, "radius": 1.59 * mm});
            skCircle(sketch, "E37.209.0.6", {"center": v(-138.1, -52.39) * mm, "radius": 1.59 * mm});
            skCircle(sketch, "E37.211.0.6", {"center": v(-87.3, -52.39) * mm, "radius": 1.59 * mm});
            skCircle(sketch, "E37.213.0.6", {"center": v(-36.5, -52.39) * mm, "radius": 1.59 * mm});
            skCircle(sketch, "E37.215.0.6", {"center": v(14.3, -52.39) * mm, "radius": 1.59 * mm});
            skCircle(sketch, "E37.217.0.6", {"center": v(-239.7, -52.39) * mm, "radius": 1.59 * mm});
            skCircle(sketch, "E37.219.0.6", {"center": v(-188.9, -52.39) * mm, "radius": 1.59 * mm});
            skCircle(sketch, "E37.221.0.6", {"center": v(261.95, -52.39) * mm, "radius": 1.59 * mm});
            skCircle(sketch, "E37.223.0.6", {"center": v(58.75, -52.39) * mm, "radius": 1.59 * mm});
            skCircle(sketch, "E37.225.0.6", {"center": v(109.55, -52.39) * mm, "radius": 1.59 * mm});
            skCircle(sketch, "E37.227.0.6", {"center": v(160.35, -52.39) * mm, "radius": 1.59 * mm});
            skCircle(sketch, "E37.229.0.6", {"center": v(211.15, -52.39) * mm, "radius": 1.59 * mm});
            skCircle(sketch, "E37.231.0.6", {"center": v(-144.45, -52.39) * mm, "radius": 1.59 * mm});
            skCircle(sketch, "E37.233.0.6", {"center": v(-93.65, -52.39) * mm, "radius": 1.59 * mm});
            skCircle(sketch, "E37.235.0.6", {"center": v(-42.85, -52.39) * mm, "radius": 1.59 * mm});
            skCircle(sketch, "E37.237.0.6", {"center": v(7.95, -52.39) * mm, "radius": 1.59 * mm});
            skCircle(sketch, "E37.239.0.6", {"center": v(-246.05, -52.39) * mm, "radius": 1.59 * mm});
            skCircle(sketch, "E37.241.0.6", {"center": v(-195.25, -52.39) * mm, "radius": 1.59 * mm});
            skCircle(sketch, "E37.243.0.6", {"center": v(258.78, -49.21) * mm, "radius": 1.59 * mm});
            skCircle(sketch, "E37.245.0.6", {"center": v(55.58, -49.21) * mm, "radius": 1.59 * mm});
            skCircle(sketch, "E37.247.0.6", {"center": v(106.38, -49.21) * mm, "radius": 1.59 * mm});
            skCircle(sketch, "E37.249.0.6", {"center": v(157.18, -49.21) * mm, "radius": 1.59 * mm});
            skCircle(sketch, "E37.251.0.6", {"center": v(207.98, -49.21) * mm, "radius": 1.59 * mm});
            skCircle(sketch, "E37.253.0.6", {"center": v(-147.62, -49.21) * mm, "radius": 1.59 * mm});
            skCircle(sketch, "E37.255.0.6", {"center": v(-96.82, -49.21) * mm, "radius": 1.59 * mm});
            skCircle(sketch, "E37.257.0.6", {"center": v(-46.02, -49.21) * mm, "radius": 1.59 * mm});
            skCircle(sketch, "E37.259.0.6", {"center": v(4.78, -49.21) * mm, "radius": 1.59 * mm});
            skCircle(sketch, "E37.261.0.6", {"center": v(-249.22, -49.21) * mm, "radius": 1.59 * mm});
            skCircle(sketch, "E37.263.0.6", {"center": v(-198.42, -49.21) * mm, "radius": 1.59 * mm});
            skCircle(sketch, "E37.265.0.6", {"center": v(265.13, -49.21) * mm, "radius": 1.59 * mm});
            skCircle(sketch, "E37.267.0.6", {"center": v(61.93, -49.21) * mm, "radius": 1.59 * mm});
            skCircle(sketch, "E37.269.0.6", {"center": v(112.73, -49.21) * mm, "radius": 1.59 * mm});
            skCircle(sketch, "E37.271.0.6", {"center": v(163.53, -49.21) * mm, "radius": 1.59 * mm});
            skCircle(sketch, "E37.273.0.6", {"center": v(214.33, -49.21) * mm, "radius": 1.59 * mm});
            skCircle(sketch, "E37.275.0.6", {"center": v(-141.27, -49.21) * mm, "radius": 1.59 * mm});
            skCircle(sketch, "E37.277.0.6", {"center": v(-90.47, -49.21) * mm, "radius": 1.59 * mm});
            skCircle(sketch, "E37.279.0.6", {"center": v(-39.67, -49.21) * mm, "radius": 1.59 * mm});
            skCircle(sketch, "E37.281.0.6", {"center": v(11.13, -49.21) * mm, "radius": 1.59 * mm});
            skCircle(sketch, "E37.283.0.6", {"center": v(-242.87, -49.21) * mm, "radius": 1.59 * mm});
            skCircle(sketch, "E37.285.0.6", {"center": v(-192.07, -49.21) * mm, "radius": 1.59 * mm});
            skCircle(sketch, "E37.287.0.6", {"center": v(255.6, -52.39) * mm, "radius": 1.59 * mm});
            skCircle(sketch, "E37.289.0.6", {"center": v(52.4, -52.39) * mm, "radius": 1.59 * mm});
            skCircle(sketch, "E37.291.0.6", {"center": v(103.2, -52.39) * mm, "radius": 1.59 * mm});
            skCircle(sketch, "E37.293.0.6", {"center": v(154, -52.39) * mm, "radius": 1.59 * mm});
            skCircle(sketch, "E37.295.0.6", {"center": v(204.8, -52.39) * mm, "radius": 1.59 * mm});
            skCircle(sketch, "E37.297.0.6", {"center": v(-150.8, -52.39) * mm, "radius": 1.59 * mm});
            skCircle(sketch, "E37.299.0.6", {"center": v(-100, -52.39) * mm, "radius": 1.59 * mm});
            skCircle(sketch, "E37.301.0.6", {"center": v(-49.2, -52.39) * mm, "radius": 1.59 * mm});
            skCircle(sketch, "E37.303.0.6", {"center": v(1.6, -52.39) * mm, "radius": 1.59 * mm});
            skCircle(sketch, "E37.305.0.6", {"center": v(-252.4, -52.39) * mm, "radius": 1.59 * mm});
            skCircle(sketch, "E37.307.0.6", {"center": v(-201.6, -52.39) * mm, "radius": 1.59 * mm});
            skCircle(sketch, "E37.309.0.6", {"center": v(198.45, -52.39) * mm, "radius": 1.59 * mm});
            skCircle(sketch, "E37.311.0.6", {"center": v(147.65, -52.39) * mm, "radius": 1.59 * mm});
            skCircle(sketch, "E37.313.0.6", {"center": v(96.85, -52.39) * mm, "radius": 1.59 * mm});
            skCircle(sketch, "E37.315.0.6", {"center": v(46.05, -52.39) * mm, "radius": 1.59 * mm});
            skCircle(sketch, "E37.319.0.6", {"center": v(249.25, -52.39) * mm, "radius": 1.59 * mm});
            skCircle(sketch, "E37.321.0.6", {"center": v(296.88, -49.21) * mm, "radius": 1.59 * mm});
            skCircle(sketch, "E37.323.0.6", {"center": v(42.88, -49.21) * mm, "radius": 1.59 * mm});
            skCircle(sketch, "E37.325.0.6", {"center": v(93.68, -49.21) * mm, "radius": 1.59 * mm});
            skCircle(sketch, "E37.327.0.6", {"center": v(-58.72, -49.21) * mm, "radius": 1.59 * mm});
            skCircle(sketch, "E37.329.0.6", {"center": v(-7.92, -49.21) * mm, "radius": 1.59 * mm});
            skCircle(sketch, "E37.331.0.6", {"center": v(-20.62, -49.21) * mm, "radius": 1.59 * mm});
            skCircle(sketch, "E37.333.0.6", {"center": v(30.18, -49.21) * mm, "radius": 1.59 * mm});
            skCircle(sketch, "E37.335.0.6", {"center": v(80.98, -49.21) * mm, "radius": 1.59 * mm});
            skCircle(sketch, "E37.337.0.6", {"center": v(-71.42, -49.21) * mm, "radius": 1.59 * mm});
            skCircle(sketch, "E37.339.0.6", {"center": v(293.7, -52.39) * mm, "radius": 1.59 * mm});
            skCircle(sketch, "E37.341.0.6", {"center": v(39.7, -52.39) * mm, "radius": 1.59 * mm});
            skCircle(sketch, "E37.343.0.6", {"center": v(90.5, -52.39) * mm, "radius": 1.59 * mm});
            skCircle(sketch, "E37.345.0.6", {"center": v(-61.9, -52.39) * mm, "radius": 1.59 * mm});
            skCircle(sketch, "E37.347.0.6", {"center": v(-11.1, -52.39) * mm, "radius": 1.59 * mm});
            skCircle(sketch, "E37.349.0.6", {"center": v(-14.27, -49.21) * mm, "radius": 1.59 * mm});
            skCircle(sketch, "E37.351.0.6", {"center": v(36.53, -49.21) * mm, "radius": 1.59 * mm});
            skCircle(sketch, "E37.353.0.6", {"center": v(87.33, -49.21) * mm, "radius": 1.59 * mm});
            skCircle(sketch, "E37.355.0.6", {"center": v(-65.07, -49.21) * mm, "radius": 1.59 * mm});
            skCircle(sketch, "E37.357.0.6", {"center": v(287.35, -52.39) * mm, "radius": 1.59 * mm});
            skCircle(sketch, "E37.359.0.6", {"center": v(33.35, -52.39) * mm, "radius": 1.59 * mm});
            skCircle(sketch, "E37.361.0.6", {"center": v(84.15, -52.39) * mm, "radius": 1.59 * mm});
            skCircle(sketch, "E37.363.0.6", {"center": v(290.53, -49.21) * mm, "radius": 1.59 * mm});
            skCircle(sketch, "E37.365.0.6", {"center": v(-68.25, -52.39) * mm, "radius": 1.59 * mm});
            skCircle(sketch, "E37.367.0.6", {"center": v(-17.45, -52.39) * mm, "radius": 1.59 * mm});
            skCircle(sketch, "E37.369.0.6", {"center": v(-284.15, -52.39) * mm, "radius": 1.59 * mm});
            skCircle(sketch, "E37.371.0.6", {"center": v(-280.97, -49.21) * mm, "radius": 1.59 * mm});
            skLineSegment(sketch, "E37.373.0.6", {"start": v(290.53, -49.21) * mm, "end": v(296.88, -49.21) * mm, "construction": true});
            skCircle(sketch, "E37.376.0.6", {"center": v(-287.32, -49.21) * mm, "radius": 1.59 * mm});
            skLineSegment(sketch, "E37.378.0.6", {"start": v(-296.85, -52.39) * mm, "end": v(-290.5, -52.39) * mm, "construction": true});
            skCircle(sketch, "E37.381.0.6", {"center": v(-290.5, -52.39) * mm, "radius": 1.59 * mm});
            skLineSegment(sketch, "E37.383.0.6", {"start": v(-296.85, -49.21) * mm, "end": v(-296.85, -52.39) * mm, "construction": true});
            skLineSegment(sketch, "E37.386.0.6", {"start": v(-300.02, -49.21) * mm, "end": v(-293.67, -49.21) * mm, "construction": true});
            skCircle(sketch, "E37.389.0.6", {"center": v(-293.67, -49.21) * mm, "radius": 1.59 * mm});
            skCircle(sketch, "E37.0.0.7", {"center": v(-227, -58.74) * mm, "radius": 1.59 * mm});
            skCircle(sketch, "E37.2.0.7", {"center": v(-176.2, -58.74) * mm, "radius": 1.59 * mm});
            skCircle(sketch, "E37.4.0.7", {"center": v(-125.4, -58.74) * mm, "radius": 1.59 * mm});
            skCircle(sketch, "E37.6.0.7", {"center": v(-230.17, -55.56) * mm, "radius": 1.59 * mm});
            skCircle(sketch, "E37.8.0.7", {"center": v(-179.37, -55.56) * mm, "radius": 1.59 * mm});
            skCircle(sketch, "E37.10.0.7", {"center": v(-128.57, -55.56) * mm, "radius": 1.59 * mm});
            skCircle(sketch, "E37.12.0.7", {"center": v(-157.15, -58.74) * mm, "radius": 1.59 * mm});
            skCircle(sketch, "E37.14.0.7", {"center": v(-106.35, -58.74) * mm, "radius": 1.59 * mm});
            skCircle(sketch, "E37.16.0.7", {"center": v(-55.55, -58.74) * mm, "radius": 1.59 * mm});
            skCircle(sketch, "E37.18.0.7", {"center": v(-4.75, -58.74) * mm, "radius": 1.59 * mm});
            skCircle(sketch, "E37.20.0.7", {"center": v(-207.95, -58.74) * mm, "radius": 1.59 * mm});
            skCircle(sketch, "E37.22.0.7", {"center": v(-258.75, -58.74) * mm, "radius": 1.59 * mm});
            skCircle(sketch, "E37.24.0.7", {"center": v(246.08, -55.56) * mm, "radius": 1.59 * mm});
            skCircle(sketch, "E37.26.0.7", {"center": v(144.48, -55.56) * mm, "radius": 1.59 * mm});
            skCircle(sketch, "E37.28.0.7", {"center": v(195.28, -55.56) * mm, "radius": 1.59 * mm});
            skCircle(sketch, "E37.30.0.7", {"center": v(-160.32, -55.56) * mm, "radius": 1.59 * mm});
            skCircle(sketch, "E37.32.0.7", {"center": v(-109.52, -55.56) * mm, "radius": 1.59 * mm});
            skCircle(sketch, "E37.34.0.7", {"center": v(-261.92, -55.56) * mm, "radius": 1.59 * mm});
            skCircle(sketch, "E37.36.0.7", {"center": v(-211.12, -55.56) * mm, "radius": 1.59 * mm});
            skCircle(sketch, "E37.38.0.7", {"center": v(252.43, -55.56) * mm, "radius": 1.59 * mm});
            skLineSegment(sketch, "E37.40.0.7", {"start": v(-293.67, -55.56) * mm, "end": v(-280.97, -55.56) * mm, "construction": true});
            skCircle(sketch, "E37.43.0.7", {"center": v(49.23, -55.56) * mm, "radius": 1.59 * mm});
            skCircle(sketch, "E37.45.0.7", {"center": v(100.03, -55.56) * mm, "radius": 1.59 * mm});
            skCircle(sketch, "E37.47.0.7", {"center": v(150.83, -55.56) * mm, "radius": 1.59 * mm});
            skCircle(sketch, "E37.49.0.7", {"center": v(201.63, -55.56) * mm, "radius": 1.59 * mm});
            skCircle(sketch, "E37.51.0.7", {"center": v(-153.97, -55.56) * mm, "radius": 1.59 * mm});
            skCircle(sketch, "E37.53.0.7", {"center": v(-103.17, -55.56) * mm, "radius": 1.59 * mm});
            skCircle(sketch, "E37.55.0.7", {"center": v(-52.37, -55.56) * mm, "radius": 1.59 * mm});
            skCircle(sketch, "E37.57.0.7", {"center": v(-1.57, -55.56) * mm, "radius": 1.59 * mm});
            skCircle(sketch, "E37.59.0.7", {"center": v(-204.77, -55.56) * mm, "radius": 1.59 * mm});
            skCircle(sketch, "E37.61.0.7", {"center": v(182.58, -55.56) * mm, "radius": 1.59 * mm});
            skCircle(sketch, "E37.63.0.7", {"center": v(233.38, -55.56) * mm, "radius": 1.59 * mm});
            skCircle(sketch, "E37.65.0.7", {"center": v(284.18, -55.56) * mm, "radius": 1.59 * mm});
            skCircle(sketch, "E37.67.0.7", {"center": v(131.78, -55.56) * mm, "radius": 1.59 * mm});
            skCircle(sketch, "E37.69.0.7", {"center": v(-223.82, -55.56) * mm, "radius": 1.59 * mm});
            skCircle(sketch, "E37.71.0.7", {"center": v(-173.02, -55.56) * mm, "radius": 1.59 * mm});
            skCircle(sketch, "E37.73.0.7", {"center": v(-122.22, -55.56) * mm, "radius": 1.59 * mm});
            skCircle(sketch, "E37.75.0.7", {"center": v(242.9, -58.74) * mm, "radius": 1.59 * mm});
            skCircle(sketch, "E37.77.0.7", {"center": v(141.3, -58.74) * mm, "radius": 1.59 * mm});
            skCircle(sketch, "E37.79.0.7", {"center": v(192.1, -58.74) * mm, "radius": 1.59 * mm});
            skCircle(sketch, "E37.81.0.7", {"center": v(-163.5, -58.74) * mm, "radius": 1.59 * mm});
            skCircle(sketch, "E37.83.0.7", {"center": v(-112.7, -58.74) * mm, "radius": 1.59 * mm});
            skCircle(sketch, "E37.85.0.7", {"center": v(-214.3, -58.74) * mm, "radius": 1.59 * mm});
            skCircle(sketch, "E37.87.0.7", {"center": v(138.13, -55.56) * mm, "radius": 1.59 * mm});
            skCircle(sketch, "E37.89.0.7", {"center": v(-217.47, -55.56) * mm, "radius": 1.59 * mm});
            skCircle(sketch, "E37.91.0.7", {"center": v(-166.67, -55.56) * mm, "radius": 1.59 * mm});
            skCircle(sketch, "E37.93.0.7", {"center": v(-115.87, -55.56) * mm, "radius": 1.59 * mm});
            skCircle(sketch, "E37.95.0.7", {"center": v(236.55, -58.74) * mm, "radius": 1.59 * mm});
            skCircle(sketch, "E37.97.0.7", {"center": v(134.95, -58.74) * mm, "radius": 1.59 * mm});
            skCircle(sketch, "E37.99.0.7", {"center": v(185.75, -58.74) * mm, "radius": 1.59 * mm});
            skCircle(sketch, "E37.101.0.7", {"center": v(188.93, -55.56) * mm, "radius": 1.59 * mm});
            skCircle(sketch, "E37.103.0.7", {"center": v(239.73, -55.56) * mm, "radius": 1.59 * mm});
            skCircle(sketch, "E37.105.0.7", {"center": v(-169.85, -58.74) * mm, "radius": 1.59 * mm});
            skCircle(sketch, "E37.107.0.7", {"center": v(-119.05, -58.74) * mm, "radius": 1.59 * mm});
            skCircle(sketch, "E37.109.0.7", {"center": v(-220.65, -58.74) * mm, "radius": 1.59 * mm});
            skCircle(sketch, "E37.111.0.7", {"center": v(-74.6, -58.74) * mm, "radius": 1.59 * mm});
            skCircle(sketch, "E37.113.0.7", {"center": v(179.4, -58.74) * mm, "radius": 1.59 * mm});
            skCircle(sketch, "E37.115.0.7", {"center": v(230.2, -58.74) * mm, "radius": 1.59 * mm});
            skCircle(sketch, "E37.117.0.7", {"center": v(281, -58.74) * mm, "radius": 1.59 * mm});
            skCircle(sketch, "E37.119.0.7", {"center": v(-23.8, -58.74) * mm, "radius": 1.59 * mm});
            skCircle(sketch, "E37.121.0.7", {"center": v(27, -58.74) * mm, "radius": 1.59 * mm});
            skCircle(sketch, "E37.123.0.7", {"center": v(77.8, -58.74) * mm, "radius": 1.59 * mm});
            skCircle(sketch, "E37.125.0.7", {"center": v(128.6, -58.74) * mm, "radius": 1.59 * mm});
            skCircle(sketch, "E37.127.0.7", {"center": v(-274.62, -55.56) * mm, "radius": 1.59 * mm});
            skCircle(sketch, "E37.129.0.7", {"center": v(-268.27, -55.56) * mm, "radius": 1.59 * mm});
            skCircle(sketch, "E37.131.0.7", {"center": v(-277.8, -58.74) * mm, "radius": 1.59 * mm});
            skCircle(sketch, "E37.133.0.7", {"center": v(173.05, -58.74) * mm, "radius": 1.59 * mm});
            skCircle(sketch, "E37.135.0.7", {"center": v(223.85, -58.74) * mm, "radius": 1.59 * mm});
            skCircle(sketch, "E37.137.0.7", {"center": v(274.65, -58.74) * mm, "radius": 1.59 * mm});
            skCircle(sketch, "E37.139.0.7", {"center": v(-30.15, -58.74) * mm, "radius": 1.59 * mm});
            skCircle(sketch, "E37.141.0.7", {"center": v(20.65, -58.74) * mm, "radius": 1.59 * mm});
            skCircle(sketch, "E37.143.0.7", {"center": v(71.45, -58.74) * mm, "radius": 1.59 * mm});
            skCircle(sketch, "E37.145.0.7", {"center": v(122.25, -58.74) * mm, "radius": 1.59 * mm});
            skCircle(sketch, "E37.147.0.7", {"center": v(-233.35, -58.74) * mm, "radius": 1.59 * mm});
            skCircle(sketch, "E37.149.0.7", {"center": v(-182.55, -58.74) * mm, "radius": 1.59 * mm});
            skCircle(sketch, "E37.151.0.7", {"center": v(-131.75, -58.74) * mm, "radius": 1.59 * mm});
            skCircle(sketch, "E37.153.0.7", {"center": v(-80.95, -58.74) * mm, "radius": 1.59 * mm});
            skCircle(sketch, "E37.155.0.7", {"center": v(-255.57, -55.56) * mm, "radius": 1.59 * mm});
            skCircle(sketch, "E37.157.0.7", {"center": v(-265.1, -58.74) * mm, "radius": 1.59 * mm});
            skCircle(sketch, "E37.159.0.7", {"center": v(-271.45, -58.74) * mm, "radius": 1.59 * mm});
            skCircle(sketch, "E37.161.0.7", {"center": v(169.88, -55.56) * mm, "radius": 1.59 * mm});
            skCircle(sketch, "E37.163.0.7", {"center": v(220.68, -55.56) * mm, "radius": 1.59 * mm});
            skCircle(sketch, "E37.165.0.7", {"center": v(271.48, -55.56) * mm, "radius": 1.59 * mm});
            skCircle(sketch, "E37.167.0.7", {"center": v(-33.32, -55.56) * mm, "radius": 1.59 * mm});
            skCircle(sketch, "E37.169.0.7", {"center": v(17.48, -55.56) * mm, "radius": 1.59 * mm});
            skCircle(sketch, "E37.171.0.7", {"center": v(68.28, -55.56) * mm, "radius": 1.59 * mm});
            skCircle(sketch, "E37.173.0.7", {"center": v(-236.52, -55.56) * mm, "radius": 1.59 * mm});
            skCircle(sketch, "E37.175.0.7", {"center": v(119.08, -55.56) * mm, "radius": 1.59 * mm});
            skCircle(sketch, "E37.177.0.7", {"center": v(-185.72, -55.56) * mm, "radius": 1.59 * mm});
            skCircle(sketch, "E37.179.0.7", {"center": v(-134.92, -55.56) * mm, "radius": 1.59 * mm});
            skCircle(sketch, "E37.181.0.7", {"center": v(-84.12, -55.56) * mm, "radius": 1.59 * mm});
            skCircle(sketch, "E37.183.0.7", {"center": v(176.23, -55.56) * mm, "radius": 1.59 * mm});
            skCircle(sketch, "E37.185.0.7", {"center": v(227.03, -55.56) * mm, "radius": 1.59 * mm});
            skCircle(sketch, "E37.187.0.7", {"center": v(277.83, -55.56) * mm, "radius": 1.59 * mm});
            skCircle(sketch, "E37.189.0.7", {"center": v(-26.97, -55.56) * mm, "radius": 1.59 * mm});
            skCircle(sketch, "E37.191.0.7", {"center": v(23.83, -55.56) * mm, "radius": 1.59 * mm});
            skCircle(sketch, "E37.193.0.7", {"center": v(74.63, -55.56) * mm, "radius": 1.59 * mm});
            skCircle(sketch, "E37.195.0.7", {"center": v(125.43, -55.56) * mm, "radius": 1.59 * mm});
            skCircle(sketch, "E37.197.0.7", {"center": v(-77.77, -55.56) * mm, "radius": 1.59 * mm});
            skCircle(sketch, "E37.199.0.7", {"center": v(268.3, -58.74) * mm, "radius": 1.59 * mm});
            skCircle(sketch, "E37.201.0.7", {"center": v(65.1, -58.74) * mm, "radius": 1.59 * mm});
            skCircle(sketch, "E37.203.0.7", {"center": v(115.9, -58.74) * mm, "radius": 1.59 * mm});
            skCircle(sketch, "E37.205.0.7", {"center": v(166.7, -58.74) * mm, "radius": 1.59 * mm});
            skCircle(sketch, "E37.207.0.7", {"center": v(217.5, -58.74) * mm, "radius": 1.59 * mm});
            skCircle(sketch, "E37.209.0.7", {"center": v(-138.1, -58.74) * mm, "radius": 1.59 * mm});
            skCircle(sketch, "E37.211.0.7", {"center": v(-87.3, -58.74) * mm, "radius": 1.59 * mm});
            skCircle(sketch, "E37.213.0.7", {"center": v(-36.5, -58.74) * mm, "radius": 1.59 * mm});
            skCircle(sketch, "E37.215.0.7", {"center": v(14.3, -58.74) * mm, "radius": 1.59 * mm});
            skCircle(sketch, "E37.217.0.7", {"center": v(-239.7, -58.74) * mm, "radius": 1.59 * mm});
            skCircle(sketch, "E37.219.0.7", {"center": v(-188.9, -58.74) * mm, "radius": 1.59 * mm});
            skCircle(sketch, "E37.221.0.7", {"center": v(261.95, -58.74) * mm, "radius": 1.59 * mm});
            skCircle(sketch, "E37.223.0.7", {"center": v(58.75, -58.74) * mm, "radius": 1.59 * mm});
            skCircle(sketch, "E37.225.0.7", {"center": v(109.55, -58.74) * mm, "radius": 1.59 * mm});
            skCircle(sketch, "E37.227.0.7", {"center": v(160.35, -58.74) * mm, "radius": 1.59 * mm});
            skCircle(sketch, "E37.229.0.7", {"center": v(211.15, -58.74) * mm, "radius": 1.59 * mm});
            skCircle(sketch, "E37.231.0.7", {"center": v(-144.45, -58.74) * mm, "radius": 1.59 * mm});
            skCircle(sketch, "E37.233.0.7", {"center": v(-93.65, -58.74) * mm, "radius": 1.59 * mm});
            skCircle(sketch, "E37.235.0.7", {"center": v(-42.85, -58.74) * mm, "radius": 1.59 * mm});
            skCircle(sketch, "E37.237.0.7", {"center": v(7.95, -58.74) * mm, "radius": 1.59 * mm});
            skCircle(sketch, "E37.239.0.7", {"center": v(-246.05, -58.74) * mm, "radius": 1.59 * mm});
            skCircle(sketch, "E37.241.0.7", {"center": v(-195.25, -58.74) * mm, "radius": 1.59 * mm});
            skCircle(sketch, "E37.243.0.7", {"center": v(258.78, -55.56) * mm, "radius": 1.59 * mm});
            skCircle(sketch, "E37.245.0.7", {"center": v(55.58, -55.56) * mm, "radius": 1.59 * mm});
            skCircle(sketch, "E37.247.0.7", {"center": v(106.38, -55.56) * mm, "radius": 1.59 * mm});
            skCircle(sketch, "E37.249.0.7", {"center": v(157.18, -55.56) * mm, "radius": 1.59 * mm});
            skCircle(sketch, "E37.251.0.7", {"center": v(207.98, -55.56) * mm, "radius": 1.59 * mm});
            skCircle(sketch, "E37.253.0.7", {"center": v(-147.62, -55.56) * mm, "radius": 1.59 * mm});
            skCircle(sketch, "E37.255.0.7", {"center": v(-96.82, -55.56) * mm, "radius": 1.59 * mm});
            skCircle(sketch, "E37.257.0.7", {"center": v(-46.02, -55.56) * mm, "radius": 1.59 * mm});
            skCircle(sketch, "E37.259.0.7", {"center": v(4.78, -55.56) * mm, "radius": 1.59 * mm});
            skCircle(sketch, "E37.261.0.7", {"center": v(-249.22, -55.56) * mm, "radius": 1.59 * mm});
            skCircle(sketch, "E37.263.0.7", {"center": v(-198.42, -55.56) * mm, "radius": 1.59 * mm});
            skCircle(sketch, "E37.265.0.7", {"center": v(265.13, -55.56) * mm, "radius": 1.59 * mm});
            skCircle(sketch, "E37.267.0.7", {"center": v(61.93, -55.56) * mm, "radius": 1.59 * mm});
            skCircle(sketch, "E37.269.0.7", {"center": v(112.73, -55.56) * mm, "radius": 1.59 * mm});
            skCircle(sketch, "E37.271.0.7", {"center": v(163.53, -55.56) * mm, "radius": 1.59 * mm});
            skCircle(sketch, "E37.273.0.7", {"center": v(214.33, -55.56) * mm, "radius": 1.59 * mm});
            skCircle(sketch, "E37.275.0.7", {"center": v(-141.27, -55.56) * mm, "radius": 1.59 * mm});
            skCircle(sketch, "E37.277.0.7", {"center": v(-90.47, -55.56) * mm, "radius": 1.59 * mm});
            skCircle(sketch, "E37.279.0.7", {"center": v(-39.67, -55.56) * mm, "radius": 1.59 * mm});
            skCircle(sketch, "E37.281.0.7", {"center": v(11.13, -55.56) * mm, "radius": 1.59 * mm});
            skCircle(sketch, "E37.283.0.7", {"center": v(-242.87, -55.56) * mm, "radius": 1.59 * mm});
            skCircle(sketch, "E37.285.0.7", {"center": v(-192.07, -55.56) * mm, "radius": 1.59 * mm});
            skCircle(sketch, "E37.287.0.7", {"center": v(255.6, -58.74) * mm, "radius": 1.59 * mm});
            skCircle(sketch, "E37.289.0.7", {"center": v(52.4, -58.74) * mm, "radius": 1.59 * mm});
            skCircle(sketch, "E37.291.0.7", {"center": v(103.2, -58.74) * mm, "radius": 1.59 * mm});
            skCircle(sketch, "E37.293.0.7", {"center": v(154, -58.74) * mm, "radius": 1.59 * mm});
            skCircle(sketch, "E37.295.0.7", {"center": v(204.8, -58.74) * mm, "radius": 1.59 * mm});
            skCircle(sketch, "E37.297.0.7", {"center": v(-150.8, -58.74) * mm, "radius": 1.59 * mm});
            skCircle(sketch, "E37.299.0.7", {"center": v(-100, -58.74) * mm, "radius": 1.59 * mm});
            skCircle(sketch, "E37.301.0.7", {"center": v(-49.2, -58.74) * mm, "radius": 1.59 * mm});
            skCircle(sketch, "E37.303.0.7", {"center": v(1.6, -58.74) * mm, "radius": 1.59 * mm});
            skCircle(sketch, "E37.305.0.7", {"center": v(-252.4, -58.74) * mm, "radius": 1.59 * mm});
            skCircle(sketch, "E37.307.0.7", {"center": v(-201.6, -58.74) * mm, "radius": 1.59 * mm});
            skCircle(sketch, "E37.309.0.7", {"center": v(198.45, -58.74) * mm, "radius": 1.59 * mm});
            skCircle(sketch, "E37.311.0.7", {"center": v(147.65, -58.74) * mm, "radius": 1.59 * mm});
            skCircle(sketch, "E37.313.0.7", {"center": v(96.85, -58.74) * mm, "radius": 1.59 * mm});
            skCircle(sketch, "E37.315.0.7", {"center": v(46.05, -58.74) * mm, "radius": 1.59 * mm});
            skCircle(sketch, "E37.319.0.7", {"center": v(249.25, -58.74) * mm, "radius": 1.59 * mm});
            skCircle(sketch, "E37.323.0.7", {"center": v(42.88, -55.56) * mm, "radius": 1.59 * mm});
            skCircle(sketch, "E37.325.0.7", {"center": v(93.68, -55.56) * mm, "radius": 1.59 * mm});
            skCircle(sketch, "E37.327.0.7", {"center": v(-58.72, -55.56) * mm, "radius": 1.59 * mm});
            skCircle(sketch, "E37.329.0.7", {"center": v(-7.92, -55.56) * mm, "radius": 1.59 * mm});
            skCircle(sketch, "E37.331.0.7", {"center": v(-20.62, -55.56) * mm, "radius": 1.59 * mm});
            skCircle(sketch, "E37.333.0.7", {"center": v(30.18, -55.56) * mm, "radius": 1.59 * mm});
            skCircle(sketch, "E37.335.0.7", {"center": v(80.98, -55.56) * mm, "radius": 1.59 * mm});
            skCircle(sketch, "E37.337.0.7", {"center": v(-71.42, -55.56) * mm, "radius": 1.59 * mm});
            skCircle(sketch, "E37.341.0.7", {"center": v(39.7, -58.74) * mm, "radius": 1.59 * mm});
            skCircle(sketch, "E37.343.0.7", {"center": v(90.5, -58.74) * mm, "radius": 1.59 * mm});
            skCircle(sketch, "E37.345.0.7", {"center": v(-61.9, -58.74) * mm, "radius": 1.59 * mm});
            skCircle(sketch, "E37.347.0.7", {"center": v(-11.1, -58.74) * mm, "radius": 1.59 * mm});
            skCircle(sketch, "E37.349.0.7", {"center": v(-14.27, -55.56) * mm, "radius": 1.59 * mm});
            skCircle(sketch, "E37.351.0.7", {"center": v(36.53, -55.56) * mm, "radius": 1.59 * mm});
            skCircle(sketch, "E37.353.0.7", {"center": v(87.33, -55.56) * mm, "radius": 1.59 * mm});
            skCircle(sketch, "E37.355.0.7", {"center": v(-65.07, -55.56) * mm, "radius": 1.59 * mm});
            skCircle(sketch, "E37.357.0.7", {"center": v(287.35, -58.74) * mm, "radius": 1.59 * mm});
            skCircle(sketch, "E37.359.0.7", {"center": v(33.35, -58.74) * mm, "radius": 1.59 * mm});
            skCircle(sketch, "E37.361.0.7", {"center": v(84.15, -58.74) * mm, "radius": 1.59 * mm});
            skCircle(sketch, "E37.363.0.7", {"center": v(290.53, -55.56) * mm, "radius": 1.59 * mm});
            skCircle(sketch, "E37.365.0.7", {"center": v(-68.25, -58.74) * mm, "radius": 1.59 * mm});
            skCircle(sketch, "E37.367.0.7", {"center": v(-17.45, -58.74) * mm, "radius": 1.59 * mm});
            skCircle(sketch, "E37.369.0.7", {"center": v(-284.15, -58.74) * mm, "radius": 1.59 * mm});
            skCircle(sketch, "E37.371.0.7", {"center": v(-280.97, -55.56) * mm, "radius": 1.59 * mm});
            skLineSegment(sketch, "E37.373.0.7", {"start": v(290.53, -55.56) * mm, "end": v(296.88, -55.56) * mm, "construction": true});
            skCircle(sketch, "E37.376.0.7", {"center": v(-287.32, -55.56) * mm, "radius": 1.59 * mm});
            skLineSegment(sketch, "E37.378.0.7", {"start": v(-296.85, -58.74) * mm, "end": v(-290.5, -58.74) * mm, "construction": true});
            skCircle(sketch, "E37.381.0.7", {"center": v(-290.5, -58.74) * mm, "radius": 1.59 * mm});
            skLineSegment(sketch, "E37.383.0.7", {"start": v(-296.85, -55.56) * mm, "end": v(-296.85, -58.74) * mm, "construction": true});
            skLineSegment(sketch, "E37.386.0.7", {"start": v(-300.02, -55.56) * mm, "end": v(-293.67, -55.56) * mm, "construction": true});
            skCircle(sketch, "E37.389.0.7", {"center": v(-293.67, -55.56) * mm, "radius": 1.59 * mm});
            skCircle(sketch, "E37.0.0.8", {"center": v(-227, -65.09) * mm, "radius": 1.59 * mm});
            skCircle(sketch, "E37.2.0.8", {"center": v(-176.2, -65.09) * mm, "radius": 1.59 * mm});
            skCircle(sketch, "E37.4.0.8", {"center": v(-125.4, -65.09) * mm, "radius": 1.59 * mm});
            skCircle(sketch, "E37.6.0.8", {"center": v(-230.17, -61.91) * mm, "radius": 1.59 * mm});
            skCircle(sketch, "E37.8.0.8", {"center": v(-179.37, -61.91) * mm, "radius": 1.59 * mm});
            skCircle(sketch, "E37.10.0.8", {"center": v(-128.57, -61.91) * mm, "radius": 1.59 * mm});
            skCircle(sketch, "E37.12.0.8", {"center": v(-157.15, -65.09) * mm, "radius": 1.59 * mm});
            skCircle(sketch, "E37.14.0.8", {"center": v(-106.35, -65.09) * mm, "radius": 1.59 * mm});
            skCircle(sketch, "E37.16.0.8", {"center": v(-55.55, -65.09) * mm, "radius": 1.59 * mm});
            skCircle(sketch, "E37.18.0.8", {"center": v(-4.75, -65.09) * mm, "radius": 1.59 * mm});
            skCircle(sketch, "E37.20.0.8", {"center": v(-207.95, -65.09) * mm, "radius": 1.59 * mm});
            skCircle(sketch, "E37.22.0.8", {"center": v(-258.75, -65.09) * mm, "radius": 1.59 * mm});
            skCircle(sketch, "E37.24.0.8", {"center": v(246.08, -61.91) * mm, "radius": 1.59 * mm});
            skCircle(sketch, "E37.26.0.8", {"center": v(144.48, -61.91) * mm, "radius": 1.59 * mm});
            skCircle(sketch, "E37.28.0.8", {"center": v(195.28, -61.91) * mm, "radius": 1.59 * mm});
            skCircle(sketch, "E37.30.0.8", {"center": v(-160.32, -61.91) * mm, "radius": 1.59 * mm});
            skCircle(sketch, "E37.32.0.8", {"center": v(-109.52, -61.91) * mm, "radius": 1.59 * mm});
            skCircle(sketch, "E37.34.0.8", {"center": v(-261.92, -61.91) * mm, "radius": 1.59 * mm});
            skCircle(sketch, "E37.36.0.8", {"center": v(-211.12, -61.91) * mm, "radius": 1.59 * mm});
            skCircle(sketch, "E37.38.0.8", {"center": v(252.43, -61.91) * mm, "radius": 1.59 * mm});
            skLineSegment(sketch, "E37.40.0.8", {"start": v(-293.67, -61.91) * mm, "end": v(-280.97, -61.91) * mm, "construction": true});
            skCircle(sketch, "E37.43.0.8", {"center": v(49.23, -61.91) * mm, "radius": 1.59 * mm});
            skCircle(sketch, "E37.45.0.8", {"center": v(100.03, -61.91) * mm, "radius": 1.59 * mm});
            skCircle(sketch, "E37.47.0.8", {"center": v(150.83, -61.91) * mm, "radius": 1.59 * mm});
            skCircle(sketch, "E37.49.0.8", {"center": v(201.63, -61.91) * mm, "radius": 1.59 * mm});
            skCircle(sketch, "E37.51.0.8", {"center": v(-153.97, -61.91) * mm, "radius": 1.59 * mm});
            skCircle(sketch, "E37.53.0.8", {"center": v(-103.17, -61.91) * mm, "radius": 1.59 * mm});
            skCircle(sketch, "E37.55.0.8", {"center": v(-52.37, -61.91) * mm, "radius": 1.59 * mm});
            skCircle(sketch, "E37.57.0.8", {"center": v(-1.57, -61.91) * mm, "radius": 1.59 * mm});
            skCircle(sketch, "E37.59.0.8", {"center": v(-204.77, -61.91) * mm, "radius": 1.59 * mm});
            skCircle(sketch, "E37.61.0.8", {"center": v(182.58, -61.91) * mm, "radius": 1.59 * mm});
            skCircle(sketch, "E37.63.0.8", {"center": v(233.38, -61.91) * mm, "radius": 1.59 * mm});
            skCircle(sketch, "E37.65.0.8", {"center": v(284.18, -61.91) * mm, "radius": 1.59 * mm});
            skCircle(sketch, "E37.67.0.8", {"center": v(131.78, -61.91) * mm, "radius": 1.59 * mm});
            skCircle(sketch, "E37.69.0.8", {"center": v(-223.82, -61.91) * mm, "radius": 1.59 * mm});
            skCircle(sketch, "E37.71.0.8", {"center": v(-173.02, -61.91) * mm, "radius": 1.59 * mm});
            skCircle(sketch, "E37.73.0.8", {"center": v(-122.22, -61.91) * mm, "radius": 1.59 * mm});
            skCircle(sketch, "E37.75.0.8", {"center": v(242.9, -65.09) * mm, "radius": 1.59 * mm});
            skCircle(sketch, "E37.77.0.8", {"center": v(141.3, -65.09) * mm, "radius": 1.59 * mm});
            skCircle(sketch, "E37.79.0.8", {"center": v(192.1, -65.09) * mm, "radius": 1.59 * mm});
            skCircle(sketch, "E37.81.0.8", {"center": v(-163.5, -65.09) * mm, "radius": 1.59 * mm});
            skCircle(sketch, "E37.83.0.8", {"center": v(-112.7, -65.09) * mm, "radius": 1.59 * mm});
            skCircle(sketch, "E37.85.0.8", {"center": v(-214.3, -65.09) * mm, "radius": 1.59 * mm});
            skCircle(sketch, "E37.87.0.8", {"center": v(138.13, -61.91) * mm, "radius": 1.59 * mm});
            skCircle(sketch, "E37.89.0.8", {"center": v(-217.47, -61.91) * mm, "radius": 1.59 * mm});
            skCircle(sketch, "E37.91.0.8", {"center": v(-166.67, -61.91) * mm, "radius": 1.59 * mm});
            skCircle(sketch, "E37.93.0.8", {"center": v(-115.87, -61.91) * mm, "radius": 1.59 * mm});
            skCircle(sketch, "E37.95.0.8", {"center": v(236.55, -65.09) * mm, "radius": 1.59 * mm});
            skCircle(sketch, "E37.97.0.8", {"center": v(134.95, -65.09) * mm, "radius": 1.59 * mm});
            skCircle(sketch, "E37.99.0.8", {"center": v(185.75, -65.09) * mm, "radius": 1.59 * mm});
            skCircle(sketch, "E37.101.0.8", {"center": v(188.93, -61.91) * mm, "radius": 1.59 * mm});
            skCircle(sketch, "E37.103.0.8", {"center": v(239.73, -61.91) * mm, "radius": 1.59 * mm});
            skCircle(sketch, "E37.105.0.8", {"center": v(-169.85, -65.09) * mm, "radius": 1.59 * mm});
            skCircle(sketch, "E37.107.0.8", {"center": v(-119.05, -65.09) * mm, "radius": 1.59 * mm});
            skCircle(sketch, "E37.109.0.8", {"center": v(-220.65, -65.09) * mm, "radius": 1.59 * mm});
            skCircle(sketch, "E37.111.0.8", {"center": v(-74.6, -65.09) * mm, "radius": 1.59 * mm});
            skCircle(sketch, "E37.113.0.8", {"center": v(179.4, -65.09) * mm, "radius": 1.59 * mm});
            skCircle(sketch, "E37.115.0.8", {"center": v(230.2, -65.09) * mm, "radius": 1.59 * mm});
            skCircle(sketch, "E37.117.0.8", {"center": v(281, -65.09) * mm, "radius": 1.59 * mm});
            skCircle(sketch, "E37.119.0.8", {"center": v(-23.8, -65.09) * mm, "radius": 1.59 * mm});
            skCircle(sketch, "E37.121.0.8", {"center": v(27, -65.09) * mm, "radius": 1.59 * mm});
            skCircle(sketch, "E37.123.0.8", {"center": v(77.8, -65.09) * mm, "radius": 1.59 * mm});
            skCircle(sketch, "E37.125.0.8", {"center": v(128.6, -65.09) * mm, "radius": 1.59 * mm});
            skCircle(sketch, "E37.127.0.8", {"center": v(-274.62, -61.91) * mm, "radius": 1.59 * mm});
            skCircle(sketch, "E37.129.0.8", {"center": v(-268.27, -61.91) * mm, "radius": 1.59 * mm});
            skCircle(sketch, "E37.131.0.8", {"center": v(-277.8, -65.09) * mm, "radius": 1.59 * mm});
            skCircle(sketch, "E37.133.0.8", {"center": v(173.05, -65.09) * mm, "radius": 1.59 * mm});
            skCircle(sketch, "E37.135.0.8", {"center": v(223.85, -65.09) * mm, "radius": 1.59 * mm});
            skCircle(sketch, "E37.137.0.8", {"center": v(274.65, -65.09) * mm, "radius": 1.59 * mm});
            skCircle(sketch, "E37.139.0.8", {"center": v(-30.15, -65.09) * mm, "radius": 1.59 * mm});
            skCircle(sketch, "E37.141.0.8", {"center": v(20.65, -65.09) * mm, "radius": 1.59 * mm});
            skCircle(sketch, "E37.143.0.8", {"center": v(71.45, -65.09) * mm, "radius": 1.59 * mm});
            skCircle(sketch, "E37.145.0.8", {"center": v(122.25, -65.09) * mm, "radius": 1.59 * mm});
            skCircle(sketch, "E37.147.0.8", {"center": v(-233.35, -65.09) * mm, "radius": 1.59 * mm});
            skCircle(sketch, "E37.149.0.8", {"center": v(-182.55, -65.09) * mm, "radius": 1.59 * mm});
            skCircle(sketch, "E37.151.0.8", {"center": v(-131.75, -65.09) * mm, "radius": 1.59 * mm});
            skCircle(sketch, "E37.153.0.8", {"center": v(-80.95, -65.09) * mm, "radius": 1.59 * mm});
            skCircle(sketch, "E37.155.0.8", {"center": v(-255.57, -61.91) * mm, "radius": 1.59 * mm});
            skCircle(sketch, "E37.157.0.8", {"center": v(-265.1, -65.09) * mm, "radius": 1.59 * mm});
            skCircle(sketch, "E37.159.0.8", {"center": v(-271.45, -65.09) * mm, "radius": 1.59 * mm});
            skCircle(sketch, "E37.161.0.8", {"center": v(169.88, -61.91) * mm, "radius": 1.59 * mm});
            skCircle(sketch, "E37.163.0.8", {"center": v(220.68, -61.91) * mm, "radius": 1.59 * mm});
            skCircle(sketch, "E37.165.0.8", {"center": v(271.48, -61.91) * mm, "radius": 1.59 * mm});
            skCircle(sketch, "E37.167.0.8", {"center": v(-33.32, -61.91) * mm, "radius": 1.59 * mm});
            skCircle(sketch, "E37.169.0.8", {"center": v(17.48, -61.91) * mm, "radius": 1.59 * mm});
            skCircle(sketch, "E37.171.0.8", {"center": v(68.28, -61.91) * mm, "radius": 1.59 * mm});
            skCircle(sketch, "E37.173.0.8", {"center": v(-236.52, -61.91) * mm, "radius": 1.59 * mm});
            skCircle(sketch, "E37.175.0.8", {"center": v(119.08, -61.91) * mm, "radius": 1.59 * mm});
            skCircle(sketch, "E37.177.0.8", {"center": v(-185.72, -61.91) * mm, "radius": 1.59 * mm});
            skCircle(sketch, "E37.179.0.8", {"center": v(-134.92, -61.91) * mm, "radius": 1.59 * mm});
            skCircle(sketch, "E37.181.0.8", {"center": v(-84.12, -61.91) * mm, "radius": 1.59 * mm});
            skCircle(sketch, "E37.183.0.8", {"center": v(176.23, -61.91) * mm, "radius": 1.59 * mm});
            skCircle(sketch, "E37.185.0.8", {"center": v(227.03, -61.91) * mm, "radius": 1.59 * mm});
            skCircle(sketch, "E37.187.0.8", {"center": v(277.83, -61.91) * mm, "radius": 1.59 * mm});
            skCircle(sketch, "E37.189.0.8", {"center": v(-26.97, -61.91) * mm, "radius": 1.59 * mm});
            skCircle(sketch, "E37.191.0.8", {"center": v(23.83, -61.91) * mm, "radius": 1.59 * mm});
            skCircle(sketch, "E37.193.0.8", {"center": v(74.63, -61.91) * mm, "radius": 1.59 * mm});
            skCircle(sketch, "E37.195.0.8", {"center": v(125.43, -61.91) * mm, "radius": 1.59 * mm});
            skCircle(sketch, "E37.197.0.8", {"center": v(-77.77, -61.91) * mm, "radius": 1.59 * mm});
            skCircle(sketch, "E37.199.0.8", {"center": v(268.3, -65.09) * mm, "radius": 1.59 * mm});
            skCircle(sketch, "E37.201.0.8", {"center": v(65.1, -65.09) * mm, "radius": 1.59 * mm});
            skCircle(sketch, "E37.203.0.8", {"center": v(115.9, -65.09) * mm, "radius": 1.59 * mm});
            skCircle(sketch, "E37.205.0.8", {"center": v(166.7, -65.09) * mm, "radius": 1.59 * mm});
            skCircle(sketch, "E37.207.0.8", {"center": v(217.5, -65.09) * mm, "radius": 1.59 * mm});
            skCircle(sketch, "E37.209.0.8", {"center": v(-138.1, -65.09) * mm, "radius": 1.59 * mm});
            skCircle(sketch, "E37.211.0.8", {"center": v(-87.3, -65.09) * mm, "radius": 1.59 * mm});
            skCircle(sketch, "E37.213.0.8", {"center": v(-36.5, -65.09) * mm, "radius": 1.59 * mm});
            skCircle(sketch, "E37.215.0.8", {"center": v(14.3, -65.09) * mm, "radius": 1.59 * mm});
            skCircle(sketch, "E37.217.0.8", {"center": v(-239.7, -65.09) * mm, "radius": 1.59 * mm});
            skCircle(sketch, "E37.219.0.8", {"center": v(-188.9, -65.09) * mm, "radius": 1.59 * mm});
            skCircle(sketch, "E37.221.0.8", {"center": v(261.95, -65.09) * mm, "radius": 1.59 * mm});
            skCircle(sketch, "E37.223.0.8", {"center": v(58.75, -65.09) * mm, "radius": 1.59 * mm});
            skCircle(sketch, "E37.225.0.8", {"center": v(109.55, -65.09) * mm, "radius": 1.59 * mm});
            skCircle(sketch, "E37.227.0.8", {"center": v(160.35, -65.09) * mm, "radius": 1.59 * mm});
            skCircle(sketch, "E37.229.0.8", {"center": v(211.15, -65.09) * mm, "radius": 1.59 * mm});
            skCircle(sketch, "E37.231.0.8", {"center": v(-144.45, -65.09) * mm, "radius": 1.59 * mm});
            skCircle(sketch, "E37.233.0.8", {"center": v(-93.65, -65.09) * mm, "radius": 1.59 * mm});
            skCircle(sketch, "E37.235.0.8", {"center": v(-42.85, -65.09) * mm, "radius": 1.59 * mm});
            skCircle(sketch, "E37.237.0.8", {"center": v(7.95, -65.09) * mm, "radius": 1.59 * mm});
            skCircle(sketch, "E37.239.0.8", {"center": v(-246.05, -65.09) * mm, "radius": 1.59 * mm});
            skCircle(sketch, "E37.241.0.8", {"center": v(-195.25, -65.09) * mm, "radius": 1.59 * mm});
            skCircle(sketch, "E37.243.0.8", {"center": v(258.78, -61.91) * mm, "radius": 1.59 * mm});
            skCircle(sketch, "E37.245.0.8", {"center": v(55.58, -61.91) * mm, "radius": 1.59 * mm});
            skCircle(sketch, "E37.247.0.8", {"center": v(106.38, -61.91) * mm, "radius": 1.59 * mm});
            skCircle(sketch, "E37.249.0.8", {"center": v(157.18, -61.91) * mm, "radius": 1.59 * mm});
            skCircle(sketch, "E37.251.0.8", {"center": v(207.98, -61.91) * mm, "radius": 1.59 * mm});
            skCircle(sketch, "E37.253.0.8", {"center": v(-147.62, -61.91) * mm, "radius": 1.59 * mm});
            skCircle(sketch, "E37.255.0.8", {"center": v(-96.82, -61.91) * mm, "radius": 1.59 * mm});
            skCircle(sketch, "E37.257.0.8", {"center": v(-46.02, -61.91) * mm, "radius": 1.59 * mm});
            skCircle(sketch, "E37.259.0.8", {"center": v(4.78, -61.91) * mm, "radius": 1.59 * mm});
            skCircle(sketch, "E37.261.0.8", {"center": v(-249.22, -61.91) * mm, "radius": 1.59 * mm});
            skCircle(sketch, "E37.263.0.8", {"center": v(-198.42, -61.91) * mm, "radius": 1.59 * mm});
            skCircle(sketch, "E37.265.0.8", {"center": v(265.13, -61.91) * mm, "radius": 1.59 * mm});
            skCircle(sketch, "E37.267.0.8", {"center": v(61.93, -61.91) * mm, "radius": 1.59 * mm});
            skCircle(sketch, "E37.269.0.8", {"center": v(112.73, -61.91) * mm, "radius": 1.59 * mm});
            skCircle(sketch, "E37.271.0.8", {"center": v(163.53, -61.91) * mm, "radius": 1.59 * mm});
            skCircle(sketch, "E37.273.0.8", {"center": v(214.33, -61.91) * mm, "radius": 1.59 * mm});
            skCircle(sketch, "E37.275.0.8", {"center": v(-141.27, -61.91) * mm, "radius": 1.59 * mm});
            skCircle(sketch, "E37.277.0.8", {"center": v(-90.47, -61.91) * mm, "radius": 1.59 * mm});
            skCircle(sketch, "E37.279.0.8", {"center": v(-39.67, -61.91) * mm, "radius": 1.59 * mm});
            skCircle(sketch, "E37.281.0.8", {"center": v(11.13, -61.91) * mm, "radius": 1.59 * mm});
            skCircle(sketch, "E37.283.0.8", {"center": v(-242.87, -61.91) * mm, "radius": 1.59 * mm});
            skCircle(sketch, "E37.285.0.8", {"center": v(-192.07, -61.91) * mm, "radius": 1.59 * mm});
            skCircle(sketch, "E37.287.0.8", {"center": v(255.6, -65.09) * mm, "radius": 1.59 * mm});
            skCircle(sketch, "E37.289.0.8", {"center": v(52.4, -65.09) * mm, "radius": 1.59 * mm});
            skCircle(sketch, "E37.291.0.8", {"center": v(103.2, -65.09) * mm, "radius": 1.59 * mm});
            skCircle(sketch, "E37.293.0.8", {"center": v(154, -65.09) * mm, "radius": 1.59 * mm});
            skCircle(sketch, "E37.295.0.8", {"center": v(204.8, -65.09) * mm, "radius": 1.59 * mm});
            skCircle(sketch, "E37.297.0.8", {"center": v(-150.8, -65.09) * mm, "radius": 1.59 * mm});
            skCircle(sketch, "E37.299.0.8", {"center": v(-100, -65.09) * mm, "radius": 1.59 * mm});
            skCircle(sketch, "E37.301.0.8", {"center": v(-49.2, -65.09) * mm, "radius": 1.59 * mm});
            skCircle(sketch, "E37.303.0.8", {"center": v(1.6, -65.09) * mm, "radius": 1.59 * mm});
            skCircle(sketch, "E37.305.0.8", {"center": v(-252.4, -65.09) * mm, "radius": 1.59 * mm});
            skCircle(sketch, "E37.307.0.8", {"center": v(-201.6, -65.09) * mm, "radius": 1.59 * mm});
            skCircle(sketch, "E37.309.0.8", {"center": v(198.45, -65.09) * mm, "radius": 1.59 * mm});
            skCircle(sketch, "E37.311.0.8", {"center": v(147.65, -65.09) * mm, "radius": 1.59 * mm});
            skCircle(sketch, "E37.313.0.8", {"center": v(96.85, -65.09) * mm, "radius": 1.59 * mm});
            skCircle(sketch, "E37.315.0.8", {"center": v(46.05, -65.09) * mm, "radius": 1.59 * mm});
            skCircle(sketch, "E37.319.0.8", {"center": v(249.25, -65.09) * mm, "radius": 1.59 * mm});
            skCircle(sketch, "E37.323.0.8", {"center": v(42.88, -61.91) * mm, "radius": 1.59 * mm});
            skCircle(sketch, "E37.325.0.8", {"center": v(93.68, -61.91) * mm, "radius": 1.59 * mm});
            skCircle(sketch, "E37.327.0.8", {"center": v(-58.72, -61.91) * mm, "radius": 1.59 * mm});
            skCircle(sketch, "E37.329.0.8", {"center": v(-7.92, -61.91) * mm, "radius": 1.59 * mm});
            skCircle(sketch, "E37.331.0.8", {"center": v(-20.62, -61.91) * mm, "radius": 1.59 * mm});
            skCircle(sketch, "E37.333.0.8", {"center": v(30.18, -61.91) * mm, "radius": 1.59 * mm});
            skCircle(sketch, "E37.335.0.8", {"center": v(80.98, -61.91) * mm, "radius": 1.59 * mm});
            skCircle(sketch, "E37.337.0.8", {"center": v(-71.42, -61.91) * mm, "radius": 1.59 * mm});
            skCircle(sketch, "E37.341.0.8", {"center": v(39.7, -65.09) * mm, "radius": 1.59 * mm});
            skCircle(sketch, "E37.343.0.8", {"center": v(90.5, -65.09) * mm, "radius": 1.59 * mm});
            skCircle(sketch, "E37.345.0.8", {"center": v(-61.9, -65.09) * mm, "radius": 1.59 * mm});
            skCircle(sketch, "E37.347.0.8", {"center": v(-11.1, -65.09) * mm, "radius": 1.59 * mm});
            skCircle(sketch, "E37.349.0.8", {"center": v(-14.27, -61.91) * mm, "radius": 1.59 * mm});
            skCircle(sketch, "E37.351.0.8", {"center": v(36.53, -61.91) * mm, "radius": 1.59 * mm});
            skCircle(sketch, "E37.353.0.8", {"center": v(87.33, -61.91) * mm, "radius": 1.59 * mm});
            skCircle(sketch, "E37.355.0.8", {"center": v(-65.07, -61.91) * mm, "radius": 1.59 * mm});
            skCircle(sketch, "E37.359.0.8", {"center": v(33.35, -65.09) * mm, "radius": 1.59 * mm});
            skCircle(sketch, "E37.361.0.8", {"center": v(84.15, -65.09) * mm, "radius": 1.59 * mm});
            skCircle(sketch, "E37.365.0.8", {"center": v(-68.25, -65.09) * mm, "radius": 1.59 * mm});
            skCircle(sketch, "E37.367.0.8", {"center": v(-17.45, -65.09) * mm, "radius": 1.59 * mm});
            skCircle(sketch, "E37.371.0.8", {"center": v(-280.97, -61.91) * mm, "radius": 1.59 * mm});
            skLineSegment(sketch, "E37.373.0.8", {"start": v(290.53, -61.91) * mm, "end": v(296.88, -61.91) * mm, "construction": true});
            skLineSegment(sketch, "E37.378.0.8", {"start": v(-296.85, -65.09) * mm, "end": v(-290.5, -65.09) * mm, "construction": true});
            skLineSegment(sketch, "E37.383.0.8", {"start": v(-296.85, -61.91) * mm, "end": v(-296.85, -65.09) * mm, "construction": true});
            skLineSegment(sketch, "E37.386.0.8", {"start": v(-300.02, -61.91) * mm, "end": v(-293.67, -61.91) * mm, "construction": true});
            skSolve(sketch);
        }
        {
            var Q0;
            Q0 = qSketchRegion(id + "F24", true);
            extrude(context, id + "F25", {"entities" : qUnion([Q0]), "operationType" : NewBodyOperationType.REMOVE, "oppositeDirection" : true, "depth" : 3.17 * mm, "offsetDistance" : 25.4 * mm});
        }
    });
